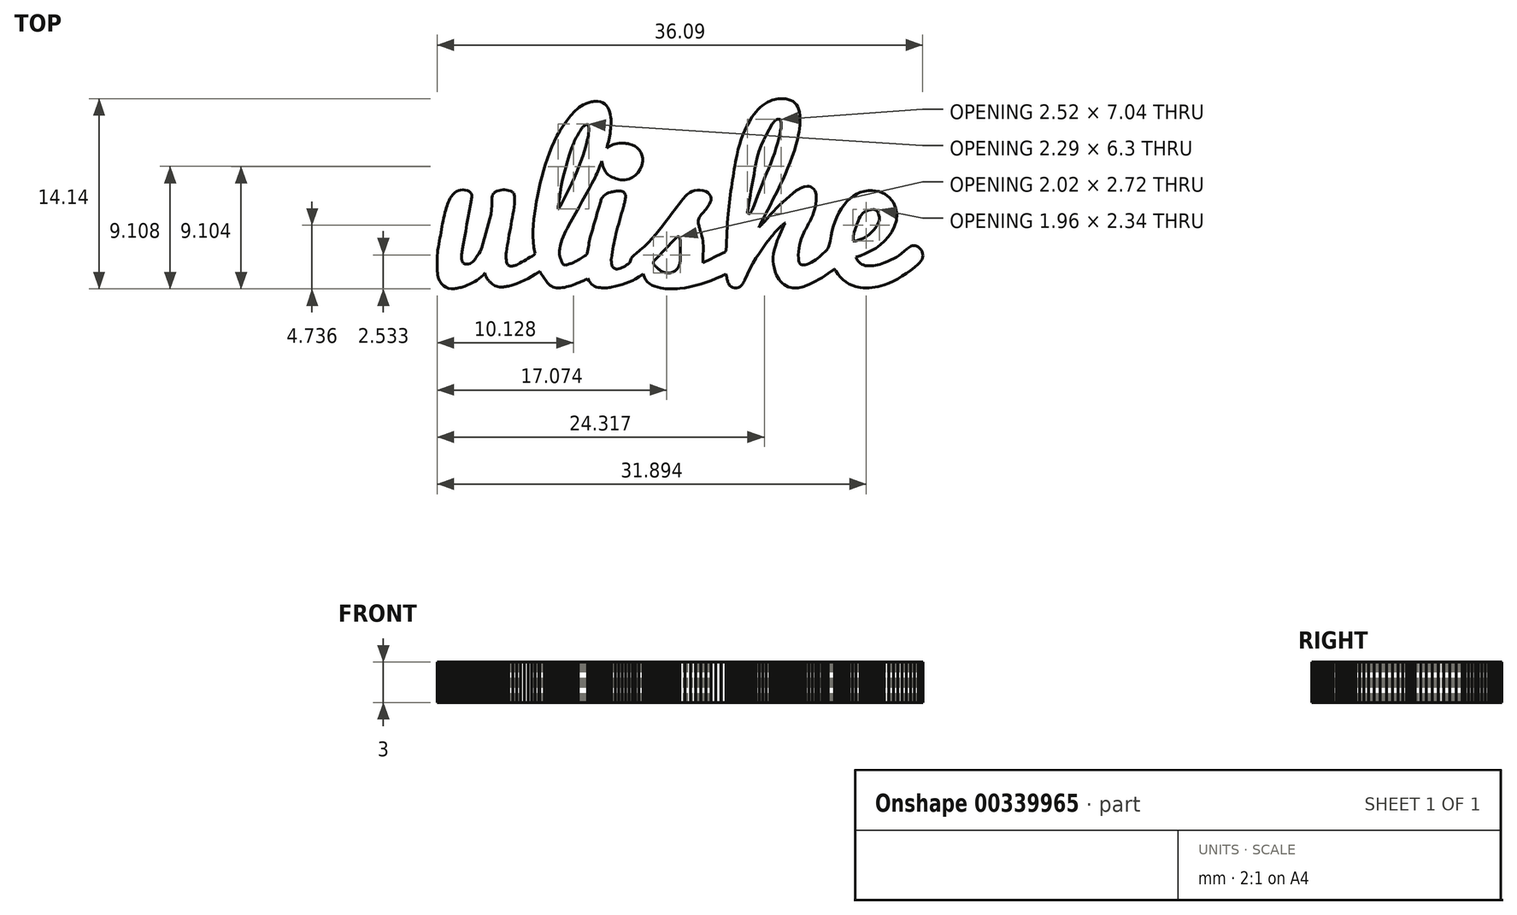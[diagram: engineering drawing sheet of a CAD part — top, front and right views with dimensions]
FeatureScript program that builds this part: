
annotation { "Feature Type Name" : "Feature", "Feature Type Description" : "" }
export const myFeature = defineFeature(function(context is Context, id is Id, definition is map)
    precondition{}
    {
        {
            var Q0;
            Q0=qCreatedBy(makeId("Top.planeOp"),FACE);
            var sketch = newSketch(context, id + "F0", { "sketchPlane" : qUnion([Q0])});
            skLineSegment(sketch, "E0", {"start": v(141.45, -110.72) * mm, "end": v(140.71, -110.13) * mm});
            skLineSegment(sketch, "E1", {"start": v(140.71, -110.13) * mm, "end": v(139.9, -109.7) * mm});
            skLineSegment(sketch, "E2", {"start": v(139.9, -109.7) * mm, "end": v(139.04, -109.45) * mm});
            skLineSegment(sketch, "E3", {"start": v(139.04, -109.45) * mm, "end": v(138.15, -109.35) * mm});
            skLineSegment(sketch, "E4", {"start": v(138.15, -109.35) * mm, "end": v(137.25, -109.42) * mm});
            skLineSegment(sketch, "E5", {"start": v(137.25, -109.42) * mm, "end": v(136.38, -109.65) * mm});
            skLineSegment(sketch, "E6", {"start": v(136.38, -109.65) * mm, "end": v(135.56, -110.05) * mm});
            skLineSegment(sketch, "E7", {"start": v(135.56, -110.05) * mm, "end": v(134.8, -110.61) * mm});
            skLineSegment(sketch, "E8", {"start": v(134.8, -110.61) * mm, "end": v(134.66, -110.74) * mm});
            skLineSegment(sketch, "E9", {"start": v(134.66, -110.74) * mm, "end": v(134.53, -110.85) * mm});
            skLineSegment(sketch, "E10", {"start": v(134.53, -110.85) * mm, "end": v(134.42, -110.95) * mm});
            skLineSegment(sketch, "E11", {"start": v(134.42, -110.95) * mm, "end": v(134.32, -111.05) * mm});
            skLineSegment(sketch, "E12", {"start": v(134.32, -111.05) * mm, "end": v(134.23, -111.12) * mm});
            skLineSegment(sketch, "E13", {"start": v(134.23, -111.12) * mm, "end": v(134.16, -111.19) * mm});
            skLineSegment(sketch, "E14", {"start": v(134.16, -111.19) * mm, "end": v(134.1, -111.23) * mm});
            skLineSegment(sketch, "E15", {"start": v(134.1, -111.23) * mm, "end": v(134.07, -111.26) * mm});
            skLineSegment(sketch, "E16", {"start": v(134.07, -111.26) * mm, "end": v(132.19, -112.88) * mm});
            skLineSegment(sketch, "E17", {"start": v(132.19, -112.88) * mm, "end": v(130.49, -114.23) * mm});
            skLineSegment(sketch, "E18", {"start": v(130.49, -114.23) * mm, "end": v(128.9, -115.38) * mm});
            skLineSegment(sketch, "E19", {"start": v(128.9, -115.38) * mm, "end": v(127.31, -116.38) * mm});
            skLineSegment(sketch, "E20", {"start": v(127.31, -116.38) * mm, "end": v(125.68, -117.3) * mm});
            skLineSegment(sketch, "E21", {"start": v(125.68, -117.3) * mm, "end": v(123.9, -118.17) * mm});
            skLineSegment(sketch, "E22", {"start": v(123.9, -118.17) * mm, "end": v(121.91, -119.06) * mm});
            skLineSegment(sketch, "E23", {"start": v(121.91, -119.06) * mm, "end": v(119.62, -120.04) * mm});
            skLineSegment(sketch, "E24", {"start": v(119.62, -120.04) * mm, "end": v(118.34, -120.53) * mm});
            skLineSegment(sketch, "E25", {"start": v(118.34, -120.53) * mm, "end": v(117.06, -120.94) * mm});
            skLineSegment(sketch, "E26", {"start": v(117.06, -120.94) * mm, "end": v(115.77, -121.28) * mm});
            skLineSegment(sketch, "E27", {"start": v(115.77, -121.28) * mm, "end": v(114.47, -121.53) * mm});
            skLineSegment(sketch, "E28", {"start": v(114.47, -121.53) * mm, "end": v(113.16, -121.72) * mm});
            skLineSegment(sketch, "E29", {"start": v(113.16, -121.72) * mm, "end": v(111.82, -121.83) * mm});
            skLineSegment(sketch, "E30", {"start": v(111.82, -121.83) * mm, "end": v(110.46, -121.86) * mm});
            skLineSegment(sketch, "E31", {"start": v(110.46, -121.86) * mm, "end": v(109.06, -121.83) * mm});
            skLineSegment(sketch, "E32", {"start": v(109.06, -121.83) * mm, "end": v(107.93, -121.69) * mm});
            skLineSegment(sketch, "E33", {"start": v(107.93, -121.69) * mm, "end": v(106.84, -121.37) * mm});
            skLineSegment(sketch, "E34", {"start": v(106.84, -121.37) * mm, "end": v(105.82, -120.88) * mm});
            skLineSegment(sketch, "E35", {"start": v(105.82, -120.88) * mm, "end": v(104.87, -120.26) * mm});
            skLineSegment(sketch, "E36", {"start": v(104.87, -120.26) * mm, "end": v(104.02, -119.5) * mm});
            skLineSegment(sketch, "E37", {"start": v(104.02, -119.5) * mm, "end": v(103.29, -118.62) * mm});
            skLineSegment(sketch, "E38", {"start": v(103.29, -118.62) * mm, "end": v(102.69, -117.64) * mm});
            skLineSegment(sketch, "E39", {"start": v(102.69, -117.64) * mm, "end": v(102.24, -116.57) * mm});
            skLineSegment(sketch, "E40", {"start": v(102.24, -116.57) * mm, "end": v(102.25, -116.55) * mm});
            skLineSegment(sketch, "E41", {"start": v(102.25, -116.55) * mm, "end": v(102.25, -116.54) * mm});
            skLineSegment(sketch, "E42", {"start": v(102.25, -116.54) * mm, "end": v(102.26, -116.52) * mm});
            skLineSegment(sketch, "E43", {"start": v(102.26, -116.52) * mm, "end": v(102.27, -116.5) * mm});
            skLineSegment(sketch, "E44", {"start": v(102.27, -116.5) * mm, "end": v(102.28, -116.5) * mm});
            skLineSegment(sketch, "E45", {"start": v(102.28, -116.5) * mm, "end": v(102.28, -116.48) * mm});
            skLineSegment(sketch, "E46", {"start": v(102.28, -116.48) * mm, "end": v(102.3, -116.46) * mm});
            skLineSegment(sketch, "E47", {"start": v(102.3, -116.46) * mm, "end": v(102.3, -116.45) * mm});
            skLineSegment(sketch, "E48", {"start": v(102.3, -116.45) * mm, "end": v(102.63, -116.34) * mm});
            skLineSegment(sketch, "E49", {"start": v(102.63, -116.34) * mm, "end": v(102.95, -116.23) * mm});
            skLineSegment(sketch, "E50", {"start": v(102.95, -116.23) * mm, "end": v(103.28, -116.13) * mm});
            skLineSegment(sketch, "E51", {"start": v(103.28, -116.13) * mm, "end": v(103.6, -116.02) * mm});
            skLineSegment(sketch, "E52", {"start": v(103.6, -116.02) * mm, "end": v(103.94, -115.92) * mm});
            skLineSegment(sketch, "E53", {"start": v(103.94, -115.92) * mm, "end": v(104.26, -115.8) * mm});
            skLineSegment(sketch, "E54", {"start": v(104.26, -115.8) * mm, "end": v(104.59, -115.7) * mm});
            skLineSegment(sketch, "E55", {"start": v(104.59, -115.7) * mm, "end": v(104.91, -115.59) * mm});
            skLineSegment(sketch, "E56", {"start": v(104.91, -115.59) * mm, "end": v(108.34, -114.23) * mm});
            skLineSegment(sketch, "E57", {"start": v(108.34, -114.23) * mm, "end": v(111.57, -112.65) * mm});
            skLineSegment(sketch, "E58", {"start": v(111.57, -112.65) * mm, "end": v(114.59, -110.83) * mm});
            skLineSegment(sketch, "E59", {"start": v(114.59, -110.83) * mm, "end": v(117.39, -108.74) * mm});
            skLineSegment(sketch, "E60", {"start": v(117.39, -108.74) * mm, "end": v(119.95, -106.38) * mm});
            skLineSegment(sketch, "E61", {"start": v(119.95, -106.38) * mm, "end": v(122.27, -103.74) * mm});
            skLineSegment(sketch, "E62", {"start": v(122.27, -103.74) * mm, "end": v(124.33, -100.8) * mm});
            skLineSegment(sketch, "E63", {"start": v(124.33, -100.8) * mm, "end": v(126.12, -97.53) * mm});
            skLineSegment(sketch, "E64", {"start": v(126.12, -97.53) * mm, "end": v(127.39, -93.69) * mm});
            skLineSegment(sketch, "E65", {"start": v(127.39, -93.69) * mm, "end": v(127.62, -89.82) * mm});
            skLineSegment(sketch, "E66", {"start": v(127.62, -89.82) * mm, "end": v(126.91, -86.1) * mm});
            skLineSegment(sketch, "E67", {"start": v(126.91, -86.1) * mm, "end": v(125.36, -82.67) * mm});
            skLineSegment(sketch, "E68", {"start": v(125.36, -82.67) * mm, "end": v(123.05, -79.71) * mm});
            skLineSegment(sketch, "E69", {"start": v(123.05, -79.71) * mm, "end": v(120.09, -77.37) * mm});
            skLineSegment(sketch, "E70", {"start": v(120.09, -77.37) * mm, "end": v(116.56, -75.81) * mm});
            skLineSegment(sketch, "E71", {"start": v(116.56, -75.81) * mm, "end": v(112.57, -75.2) * mm});
            skLineSegment(sketch, "E72", {"start": v(112.57, -75.2) * mm, "end": v(109.87, -75.3) * mm});
            skLineSegment(sketch, "E73", {"start": v(109.87, -75.3) * mm, "end": v(107.32, -75.7) * mm});
            skLineSegment(sketch, "E74", {"start": v(107.32, -75.7) * mm, "end": v(104.93, -76.4) * mm});
            skLineSegment(sketch, "E75", {"start": v(104.93, -76.4) * mm, "end": v(102.68, -77.37) * mm});
            skLineSegment(sketch, "E76", {"start": v(102.68, -77.37) * mm, "end": v(100.57, -78.61) * mm});
            skLineSegment(sketch, "E77", {"start": v(100.57, -78.61) * mm, "end": v(98.6, -80.12) * mm});
            skLineSegment(sketch, "E78", {"start": v(98.6, -80.12) * mm, "end": v(96.76, -81.88) * mm});
            skLineSegment(sketch, "E79", {"start": v(96.76, -81.88) * mm, "end": v(95.04, -83.87) * mm});
            skLineSegment(sketch, "E80", {"start": v(95.04, -83.87) * mm, "end": v(93.23, -86.4) * mm});
            skLineSegment(sketch, "E81", {"start": v(93.23, -86.4) * mm, "end": v(91.66, -89.03) * mm});
            skLineSegment(sketch, "E82", {"start": v(91.66, -89.03) * mm, "end": v(90.32, -91.76) * mm});
            skLineSegment(sketch, "E83", {"start": v(90.32, -91.76) * mm, "end": v(89.18, -94.57) * mm});
            skLineSegment(sketch, "E84", {"start": v(89.18, -94.57) * mm, "end": v(88.22, -97.45) * mm});
            skLineSegment(sketch, "E85", {"start": v(88.22, -97.45) * mm, "end": v(87.43, -100.39) * mm});
            skLineSegment(sketch, "E86", {"start": v(87.43, -100.39) * mm, "end": v(86.77, -103.37) * mm});
            skLineSegment(sketch, "E87", {"start": v(86.77, -103.37) * mm, "end": v(86.22, -106.4) * mm});
            skLineSegment(sketch, "E88", {"start": v(86.22, -106.4) * mm, "end": v(86.04, -107.43) * mm});
            skLineSegment(sketch, "E89", {"start": v(86.04, -107.43) * mm, "end": v(85.82, -108.43) * mm});
            skLineSegment(sketch, "E90", {"start": v(85.82, -108.43) * mm, "end": v(85.54, -109.37) * mm});
            skLineSegment(sketch, "E91", {"start": v(85.54, -109.37) * mm, "end": v(85.2, -110.26) * mm});
            skLineSegment(sketch, "E92", {"start": v(85.2, -110.26) * mm, "end": v(84.77, -111.1) * mm});
            skLineSegment(sketch, "E93", {"start": v(84.77, -111.1) * mm, "end": v(84.23, -111.9) * mm});
            skLineSegment(sketch, "E94", {"start": v(84.23, -111.9) * mm, "end": v(83.57, -112.62) * mm});
            skLineSegment(sketch, "E95", {"start": v(83.57, -112.62) * mm, "end": v(82.78, -113.3) * mm});
            skLineSegment(sketch, "E96", {"start": v(82.78, -113.3) * mm, "end": v(82.66, -113.4) * mm});
            skLineSegment(sketch, "E97", {"start": v(82.66, -113.4) * mm, "end": v(82.55, -113.5) * mm});
            skLineSegment(sketch, "E98", {"start": v(82.55, -113.5) * mm, "end": v(82.45, -113.6) * mm});
            skLineSegment(sketch, "E99", {"start": v(82.45, -113.6) * mm, "end": v(82.34, -113.7) * mm});
            skLineSegment(sketch, "E100", {"start": v(82.34, -113.7) * mm, "end": v(82.24, -113.82) * mm});
            skLineSegment(sketch, "E101", {"start": v(82.24, -113.82) * mm, "end": v(82.14, -113.93) * mm});
            skLineSegment(sketch, "E102", {"start": v(82.14, -113.93) * mm, "end": v(82.03, -114.04) * mm});
            skLineSegment(sketch, "E103", {"start": v(82.03, -114.04) * mm, "end": v(81.92, -114.14) * mm});
            skLineSegment(sketch, "E104", {"start": v(81.92, -114.14) * mm, "end": v(80.79, -115.2) * mm});
            skLineSegment(sketch, "E105", {"start": v(80.79, -115.2) * mm, "end": v(79.63, -116.22) * mm});
            skLineSegment(sketch, "E106", {"start": v(79.63, -116.22) * mm, "end": v(78.43, -117.2) * mm});
            skLineSegment(sketch, "E107", {"start": v(78.43, -117.2) * mm, "end": v(77.2, -118.1) * mm});
            skLineSegment(sketch, "E108", {"start": v(77.2, -118.1) * mm, "end": v(75.92, -118.95) * mm});
            skLineSegment(sketch, "E109", {"start": v(75.92, -118.95) * mm, "end": v(74.6, -119.7) * mm});
            skLineSegment(sketch, "E110", {"start": v(74.6, -119.7) * mm, "end": v(73.2, -120.37) * mm});
            skLineSegment(sketch, "E111", {"start": v(73.2, -120.37) * mm, "end": v(71.73, -120.93) * mm});
            skLineSegment(sketch, "E112", {"start": v(71.73, -120.93) * mm, "end": v(70.6, -121.24) * mm});
            skLineSegment(sketch, "E113", {"start": v(70.6, -121.24) * mm, "end": v(69.61, -121.35) * mm});
            skLineSegment(sketch, "E114", {"start": v(69.61, -121.35) * mm, "end": v(68.78, -121.26) * mm});
            skLineSegment(sketch, "E115", {"start": v(68.78, -121.26) * mm, "end": v(68.1, -120.95) * mm});
            skLineSegment(sketch, "E116", {"start": v(68.1, -120.95) * mm, "end": v(67.55, -120.43) * mm});
            skLineSegment(sketch, "E117", {"start": v(67.55, -120.43) * mm, "end": v(67.13, -119.7) * mm});
            skLineSegment(sketch, "E118", {"start": v(67.13, -119.7) * mm, "end": v(66.84, -118.75) * mm});
            skLineSegment(sketch, "E119", {"start": v(66.84, -118.75) * mm, "end": v(66.66, -117.57) * mm});
            skLineSegment(sketch, "E120", {"start": v(66.66, -117.57) * mm, "end": v(66.66, -117.52) * mm});
            skLineSegment(sketch, "E121", {"start": v(66.66, -117.52) * mm, "end": v(66.66, -117.48) * mm});
            skLineSegment(sketch, "E122", {"start": v(66.66, -117.48) * mm, "end": v(66.65, -117.43) * mm});
            skLineSegment(sketch, "E123", {"start": v(66.65, -117.43) * mm, "end": v(66.65, -117.39) * mm});
            skLineSegment(sketch, "E124", {"start": v(66.65, -117.39) * mm, "end": v(66.65, -117.34) * mm});
            skLineSegment(sketch, "E125", {"start": v(66.65, -117.34) * mm, "end": v(66.64, -117.3) * mm});
            skLineSegment(sketch, "E126", {"start": v(66.64, -117.3) * mm, "end": v(66.64, -117.26) * mm});
            skLineSegment(sketch, "E127", {"start": v(66.64, -117.26) * mm, "end": v(66.64, -117.21) * mm});
            skLineSegment(sketch, "E128", {"start": v(66.64, -117.21) * mm, "end": v(66.6, -115.13) * mm});
            skLineSegment(sketch, "E129", {"start": v(66.6, -115.13) * mm, "end": v(66.68, -113.07) * mm});
            skLineSegment(sketch, "E130", {"start": v(66.68, -113.07) * mm, "end": v(66.9, -111.05) * mm});
            skLineSegment(sketch, "E131", {"start": v(66.9, -111.05) * mm, "end": v(67.25, -109.05) * mm});
            skLineSegment(sketch, "E132", {"start": v(67.25, -109.05) * mm, "end": v(67.74, -107.08) * mm});
            skLineSegment(sketch, "E133", {"start": v(67.74, -107.08) * mm, "end": v(68.36, -105.14) * mm});
            skLineSegment(sketch, "E134", {"start": v(68.36, -105.14) * mm, "end": v(69.11, -103.22) * mm});
            skLineSegment(sketch, "E135", {"start": v(69.11, -103.22) * mm, "end": v(69.99, -101.34) * mm});
            skLineSegment(sketch, "E136", {"start": v(69.99, -101.34) * mm, "end": v(70.57, -100.2) * mm});
            skLineSegment(sketch, "E137", {"start": v(70.57, -100.2) * mm, "end": v(71.15, -99.07) * mm});
            skLineSegment(sketch, "E138", {"start": v(71.15, -99.07) * mm, "end": v(71.75, -97.95) * mm});
            skLineSegment(sketch, "E139", {"start": v(71.75, -97.95) * mm, "end": v(72.34, -96.82) * mm});
            skLineSegment(sketch, "E140", {"start": v(72.34, -96.82) * mm, "end": v(72.93, -95.7) * mm});
            skLineSegment(sketch, "E141", {"start": v(72.93, -95.7) * mm, "end": v(73.52, -94.56) * mm});
            skLineSegment(sketch, "E142", {"start": v(73.52, -94.56) * mm, "end": v(74.09, -93.43) * mm});
            skLineSegment(sketch, "E143", {"start": v(74.09, -93.43) * mm, "end": v(74.65, -92.29) * mm});
            skLineSegment(sketch, "E144", {"start": v(74.65, -92.29) * mm, "end": v(75.43, -90.56) * mm});
            skLineSegment(sketch, "E145", {"start": v(75.43, -90.56) * mm, "end": v(76.09, -88.8) * mm});
            skLineSegment(sketch, "E146", {"start": v(76.09, -88.8) * mm, "end": v(76.64, -87.02) * mm});
            skLineSegment(sketch, "E147", {"start": v(76.64, -87.02) * mm, "end": v(77.06, -85.22) * mm});
            skLineSegment(sketch, "E148", {"start": v(77.06, -85.22) * mm, "end": v(77.37, -83.4) * mm});
            skLineSegment(sketch, "E149", {"start": v(77.37, -83.4) * mm, "end": v(77.54, -81.54) * mm});
            skLineSegment(sketch, "E150", {"start": v(77.54, -81.54) * mm, "end": v(77.57, -79.66) * mm});
            skLineSegment(sketch, "E151", {"start": v(77.57, -79.66) * mm, "end": v(77.47, -77.76) * mm});
            skLineSegment(sketch, "E152", {"start": v(77.47, -77.76) * mm, "end": v(77.23, -76.42) * mm});
            skLineSegment(sketch, "E153", {"start": v(77.23, -76.42) * mm, "end": v(76.77, -75.26) * mm});
            skLineSegment(sketch, "E154", {"start": v(76.77, -75.26) * mm, "end": v(76.11, -74.28) * mm});
            skLineSegment(sketch, "E155", {"start": v(76.11, -74.28) * mm, "end": v(75.28, -73.5) * mm});
            skLineSegment(sketch, "E156", {"start": v(75.28, -73.5) * mm, "end": v(74.3, -72.95) * mm});
            skLineSegment(sketch, "E157", {"start": v(74.3, -72.95) * mm, "end": v(73.17, -72.63) * mm});
            skLineSegment(sketch, "E158", {"start": v(73.17, -72.63) * mm, "end": v(71.92, -72.55) * mm});
            skLineSegment(sketch, "E159", {"start": v(71.92, -72.55) * mm, "end": v(70.58, -72.74) * mm});
            skLineSegment(sketch, "E160", {"start": v(70.58, -72.74) * mm, "end": v(70.15, -72.84) * mm});
            skLineSegment(sketch, "E161", {"start": v(70.15, -72.84) * mm, "end": v(69.72, -72.97) * mm});
            skLineSegment(sketch, "E162", {"start": v(69.72, -72.97) * mm, "end": v(69.29, -73.1) * mm});
            skLineSegment(sketch, "E163", {"start": v(69.29, -73.1) * mm, "end": v(68.87, -73.26) * mm});
            skLineSegment(sketch, "E164", {"start": v(68.87, -73.26) * mm, "end": v(68.45, -73.44) * mm});
            skLineSegment(sketch, "E165", {"start": v(68.45, -73.44) * mm, "end": v(68.04, -73.62) * mm});
            skLineSegment(sketch, "E166", {"start": v(68.04, -73.62) * mm, "end": v(67.64, -73.82) * mm});
            skLineSegment(sketch, "E167", {"start": v(67.64, -73.82) * mm, "end": v(67.25, -74.04) * mm});
            skLineSegment(sketch, "E168", {"start": v(67.25, -74.04) * mm, "end": v(66.74, -74.34) * mm});
            skLineSegment(sketch, "E169", {"start": v(66.74, -74.34) * mm, "end": v(66.23, -74.66) * mm});
            skLineSegment(sketch, "E170", {"start": v(66.23, -74.66) * mm, "end": v(65.73, -74.98) * mm});
            skLineSegment(sketch, "E171", {"start": v(65.73, -74.98) * mm, "end": v(65.23, -75.32) * mm});
            skLineSegment(sketch, "E172", {"start": v(65.23, -75.32) * mm, "end": v(64.74, -75.67) * mm});
            skLineSegment(sketch, "E173", {"start": v(64.74, -75.67) * mm, "end": v(64.26, -76.03) * mm});
            skLineSegment(sketch, "E174", {"start": v(64.26, -76.03) * mm, "end": v(63.8, -76.4) * mm});
            skLineSegment(sketch, "E175", {"start": v(63.8, -76.4) * mm, "end": v(63.33, -76.78) * mm});
            skLineSegment(sketch, "E176", {"start": v(63.33, -76.78) * mm, "end": v(61.19, -78.58) * mm});
            skLineSegment(sketch, "E177", {"start": v(61.19, -78.58) * mm, "end": v(59.07, -80.4) * mm});
            skLineSegment(sketch, "E178", {"start": v(59.07, -80.4) * mm, "end": v(56.99, -82.25) * mm});
            skLineSegment(sketch, "E179", {"start": v(56.99, -82.25) * mm, "end": v(54.95, -84.14) * mm});
            skLineSegment(sketch, "E180", {"start": v(54.95, -84.14) * mm, "end": v(52.96, -86.08) * mm});
            skLineSegment(sketch, "E181", {"start": v(52.96, -86.08) * mm, "end": v(51.03, -88.09) * mm});
            skLineSegment(sketch, "E182", {"start": v(51.03, -88.09) * mm, "end": v(49.18, -90.17) * mm});
            skLineSegment(sketch, "E183", {"start": v(49.18, -90.17) * mm, "end": v(47.4, -92.33) * mm});
            skLineSegment(sketch, "E184", {"start": v(47.4, -92.33) * mm, "end": v(46.95, -92.91) * mm});
            skLineSegment(sketch, "E185", {"start": v(46.95, -92.91) * mm, "end": v(46.62, -93.35) * mm});
            skLineSegment(sketch, "E186", {"start": v(46.62, -93.35) * mm, "end": v(46.36, -93.67) * mm});
            skLineSegment(sketch, "E187", {"start": v(46.36, -93.67) * mm, "end": v(46.13, -93.95) * mm});
            skLineSegment(sketch, "E188", {"start": v(46.13, -93.95) * mm, "end": v(45.89, -94.23) * mm});
            skLineSegment(sketch, "E189", {"start": v(45.89, -94.23) * mm, "end": v(45.58, -94.55) * mm});
            skLineSegment(sketch, "E190", {"start": v(45.58, -94.55) * mm, "end": v(45.17, -94.98) * mm});
            skLineSegment(sketch, "E191", {"start": v(45.17, -94.98) * mm, "end": v(44.6, -95.56) * mm});
            skLineSegment(sketch, "E192", {"start": v(44.6, -95.56) * mm, "end": v(44.4, -95.77) * mm});
            skLineSegment(sketch, "E193", {"start": v(44.4, -95.77) * mm, "end": v(44.12, -96.05) * mm});
            skLineSegment(sketch, "E194", {"start": v(44.12, -96.05) * mm, "end": v(43.8, -96.36) * mm});
            skLineSegment(sketch, "E195", {"start": v(43.8, -96.36) * mm, "end": v(43.44, -96.7) * mm});
            skLineSegment(sketch, "E196", {"start": v(43.44, -96.7) * mm, "end": v(43.07, -97.05) * mm});
            skLineSegment(sketch, "E197", {"start": v(43.07, -97.05) * mm, "end": v(42.7, -97.38) * mm});
            skLineSegment(sketch, "E198", {"start": v(42.7, -97.38) * mm, "end": v(42.38, -97.69) * mm});
            skLineSegment(sketch, "E199", {"start": v(42.38, -97.69) * mm, "end": v(42.1, -97.95) * mm});
            skLineSegment(sketch, "E200", {"start": v(42.1, -97.95) * mm, "end": v(42.2, -97.76) * mm});
            skLineSegment(sketch, "E201", {"start": v(42.2, -97.76) * mm, "end": v(42.32, -97.53) * mm});
            skLineSegment(sketch, "E202", {"start": v(42.32, -97.53) * mm, "end": v(42.45, -97.28) * mm});
            skLineSegment(sketch, "E203", {"start": v(42.45, -97.28) * mm, "end": v(42.58, -97.02) * mm});
            skLineSegment(sketch, "E204", {"start": v(42.58, -97.02) * mm, "end": v(42.72, -96.76) * mm});
            skLineSegment(sketch, "E205", {"start": v(42.72, -96.76) * mm, "end": v(42.84, -96.53) * mm});
            skLineSegment(sketch, "E206", {"start": v(42.84, -96.53) * mm, "end": v(42.95, -96.32) * mm});
            skLineSegment(sketch, "E207", {"start": v(42.95, -96.32) * mm, "end": v(43.04, -96.15) * mm});
            skLineSegment(sketch, "E208", {"start": v(43.04, -96.15) * mm, "end": v(44.57, -93.14) * mm});
            skLineSegment(sketch, "E209", {"start": v(44.57, -93.14) * mm, "end": v(46.1, -90.15) * mm});
            skLineSegment(sketch, "E210", {"start": v(46.1, -90.15) * mm, "end": v(47.65, -87.15) * mm});
            skLineSegment(sketch, "E211", {"start": v(47.65, -87.15) * mm, "end": v(49.18, -84.15) * mm});
            skLineSegment(sketch, "E212", {"start": v(49.18, -84.15) * mm, "end": v(50.71, -81.15) * mm});
            skLineSegment(sketch, "E213", {"start": v(50.71, -81.15) * mm, "end": v(52.23, -78.14) * mm});
            skLineSegment(sketch, "E214", {"start": v(52.23, -78.14) * mm, "end": v(53.73, -75.12) * mm});
            skLineSegment(sketch, "E215", {"start": v(53.73, -75.12) * mm, "end": v(55.2, -72.1) * mm});
            skLineSegment(sketch, "E216", {"start": v(55.2, -72.1) * mm, "end": v(56.87, -68.57) * mm});
            skLineSegment(sketch, "E217", {"start": v(56.87, -68.57) * mm, "end": v(58.46, -65.02) * mm});
            skLineSegment(sketch, "E218", {"start": v(58.46, -65.02) * mm, "end": v(59.98, -61.44) * mm});
            skLineSegment(sketch, "E219", {"start": v(59.98, -61.44) * mm, "end": v(61.42, -57.83) * mm});
            skLineSegment(sketch, "E220", {"start": v(61.42, -57.83) * mm, "end": v(62.75, -54.18) * mm});
            skLineSegment(sketch, "E221", {"start": v(62.75, -54.18) * mm, "end": v(63.98, -50.49) * mm});
            skLineSegment(sketch, "E222", {"start": v(63.98, -50.49) * mm, "end": v(65.1, -46.75) * mm});
            skLineSegment(sketch, "E223", {"start": v(65.1, -46.75) * mm, "end": v(66.09, -42.98) * mm});
            skLineSegment(sketch, "E224", {"start": v(66.09, -42.98) * mm, "end": v(66.55, -40.95) * mm});
            skLineSegment(sketch, "E225", {"start": v(66.55, -40.95) * mm, "end": v(66.94, -38.92) * mm});
            skLineSegment(sketch, "E226", {"start": v(66.94, -38.92) * mm, "end": v(67.25, -36.88) * mm});
            skLineSegment(sketch, "E227", {"start": v(67.25, -36.88) * mm, "end": v(67.47, -34.84) * mm});
            skLineSegment(sketch, "E228", {"start": v(67.47, -34.84) * mm, "end": v(67.58, -32.79) * mm});
            skLineSegment(sketch, "E229", {"start": v(67.58, -32.79) * mm, "end": v(67.57, -30.73) * mm});
            skLineSegment(sketch, "E230", {"start": v(67.57, -30.73) * mm, "end": v(67.43, -28.66) * mm});
            skLineSegment(sketch, "E231", {"start": v(67.43, -28.66) * mm, "end": v(67.15, -26.58) * mm});
            skLineSegment(sketch, "E232", {"start": v(67.15, -26.58) * mm, "end": v(66.75, -24.91) * mm});
            skLineSegment(sketch, "E233", {"start": v(66.75, -24.91) * mm, "end": v(66.16, -23.4) * mm});
            skLineSegment(sketch, "E234", {"start": v(66.16, -23.4) * mm, "end": v(65.39, -22.09) * mm});
            skLineSegment(sketch, "E235", {"start": v(65.39, -22.09) * mm, "end": v(64.43, -20.95) * mm});
            skLineSegment(sketch, "E236", {"start": v(64.43, -20.95) * mm, "end": v(63.3, -20.02) * mm});
            skLineSegment(sketch, "E237", {"start": v(63.3, -20.02) * mm, "end": v(61.98, -19.28) * mm});
            skLineSegment(sketch, "E238", {"start": v(61.98, -19.28) * mm, "end": v(60.5, -18.75) * mm});
            skLineSegment(sketch, "E239", {"start": v(60.5, -18.75) * mm, "end": v(58.85, -18.44) * mm});
            skLineSegment(sketch, "E240", {"start": v(58.85, -18.44) * mm, "end": v(57.63, -18.33) * mm});
            skLineSegment(sketch, "E241", {"start": v(57.63, -18.33) * mm, "end": v(56.42, -18.3) * mm});
            skLineSegment(sketch, "E242", {"start": v(56.42, -18.3) * mm, "end": v(55.21, -18.32) * mm});
            skLineSegment(sketch, "E243", {"start": v(55.21, -18.32) * mm, "end": v(54.01, -18.43) * mm});
            skLineSegment(sketch, "E244", {"start": v(54.01, -18.43) * mm, "end": v(52.82, -18.6) * mm});
            skLineSegment(sketch, "E245", {"start": v(52.82, -18.6) * mm, "end": v(51.64, -18.87) * mm});
            skLineSegment(sketch, "E246", {"start": v(51.64, -18.87) * mm, "end": v(50.47, -19.21) * mm});
            skLineSegment(sketch, "E247", {"start": v(50.47, -19.21) * mm, "end": v(49.32, -19.64) * mm});
            skLineSegment(sketch, "E248", {"start": v(49.32, -19.64) * mm, "end": v(47.55, -20.47) * mm});
            skLineSegment(sketch, "E249", {"start": v(47.55, -20.47) * mm, "end": v(45.9, -21.44) * mm});
            skLineSegment(sketch, "E250", {"start": v(45.9, -21.44) * mm, "end": v(44.36, -22.53) * mm});
            skLineSegment(sketch, "E251", {"start": v(44.36, -22.53) * mm, "end": v(42.92, -23.74) * mm});
            skLineSegment(sketch, "E252", {"start": v(42.92, -23.74) * mm, "end": v(41.58, -25.05) * mm});
            skLineSegment(sketch, "E253", {"start": v(41.58, -25.05) * mm, "end": v(40.32, -26.46) * mm});
            skLineSegment(sketch, "E254", {"start": v(40.32, -26.46) * mm, "end": v(39.13, -27.95) * mm});
            skLineSegment(sketch, "E255", {"start": v(39.13, -27.95) * mm, "end": v(38.02, -29.52) * mm});
            skLineSegment(sketch, "E256", {"start": v(38.02, -29.52) * mm, "end": v(36.3, -32.23) * mm});
            skLineSegment(sketch, "E257", {"start": v(36.3, -32.23) * mm, "end": v(34.75, -35.01) * mm});
            skLineSegment(sketch, "E258", {"start": v(34.75, -35.01) * mm, "end": v(33.37, -37.86) * mm});
            skLineSegment(sketch, "E259", {"start": v(33.37, -37.86) * mm, "end": v(32.15, -40.77) * mm});
            skLineSegment(sketch, "E260", {"start": v(32.15, -40.77) * mm, "end": v(31.06, -43.74) * mm});
            skLineSegment(sketch, "E261", {"start": v(31.06, -43.74) * mm, "end": v(30.1, -46.76) * mm});
            skLineSegment(sketch, "E262", {"start": v(30.1, -46.76) * mm, "end": v(29.28, -49.83) * mm});
            skLineSegment(sketch, "E263", {"start": v(29.28, -49.83) * mm, "end": v(28.55, -52.93) * mm});
            skLineSegment(sketch, "E264", {"start": v(28.55, -52.93) * mm, "end": v(28.1, -55.16) * mm});
            skLineSegment(sketch, "E265", {"start": v(28.1, -55.16) * mm, "end": v(27.67, -57.4) * mm});
            skLineSegment(sketch, "E266", {"start": v(27.67, -57.4) * mm, "end": v(27.27, -59.63) * mm});
            skLineSegment(sketch, "E267", {"start": v(27.27, -59.63) * mm, "end": v(26.89, -61.88) * mm});
            skLineSegment(sketch, "E268", {"start": v(26.89, -61.88) * mm, "end": v(26.53, -64.12) * mm});
            skLineSegment(sketch, "E269", {"start": v(26.53, -64.12) * mm, "end": v(26.18, -66.38) * mm});
            skLineSegment(sketch, "E270", {"start": v(26.18, -66.38) * mm, "end": v(25.84, -68.63) * mm});
            skLineSegment(sketch, "E271", {"start": v(25.84, -68.63) * mm, "end": v(25.5, -70.88) * mm});
            skLineSegment(sketch, "E272", {"start": v(25.5, -70.88) * mm, "end": v(25.15, -73.22) * mm});
            skLineSegment(sketch, "E273", {"start": v(25.15, -73.22) * mm, "end": v(24.8, -75.56) * mm});
            skLineSegment(sketch, "E274", {"start": v(24.8, -75.56) * mm, "end": v(24.46, -77.9) * mm});
            skLineSegment(sketch, "E275", {"start": v(24.46, -77.9) * mm, "end": v(24.12, -80.25) * mm});
            skLineSegment(sketch, "E276", {"start": v(24.12, -80.25) * mm, "end": v(23.81, -82.6) * mm});
            skLineSegment(sketch, "E277", {"start": v(23.81, -82.6) * mm, "end": v(23.52, -84.95) * mm});
            skLineSegment(sketch, "E278", {"start": v(23.52, -84.95) * mm, "end": v(23.27, -87.3) * mm});
            skLineSegment(sketch, "E279", {"start": v(23.27, -87.3) * mm, "end": v(23.04, -89.65) * mm});
            skLineSegment(sketch, "E280", {"start": v(23.04, -89.65) * mm, "end": v(22.82, -92.46) * mm});
            skLineSegment(sketch, "E281", {"start": v(22.82, -92.46) * mm, "end": v(22.64, -95.27) * mm});
            skLineSegment(sketch, "E282", {"start": v(22.64, -95.27) * mm, "end": v(22.48, -98.08) * mm});
            skLineSegment(sketch, "E283", {"start": v(22.48, -98.08) * mm, "end": v(22.34, -100.9) * mm});
            skLineSegment(sketch, "E284", {"start": v(22.34, -100.9) * mm, "end": v(22.21, -103.7) * mm});
            skLineSegment(sketch, "E285", {"start": v(22.21, -103.7) * mm, "end": v(22.08, -106.52) * mm});
            skLineSegment(sketch, "E286", {"start": v(22.08, -106.52) * mm, "end": v(21.95, -109.34) * mm});
            skLineSegment(sketch, "E287", {"start": v(21.95, -109.34) * mm, "end": v(21.8, -112.15) * mm});
            skLineSegment(sketch, "E288", {"start": v(21.8, -112.15) * mm, "end": v(21.78, -112.3) * mm});
            skLineSegment(sketch, "E289", {"start": v(21.78, -112.3) * mm, "end": v(21.74, -112.45) * mm});
            skLineSegment(sketch, "E290", {"start": v(21.74, -112.45) * mm, "end": v(21.67, -112.61) * mm});
            skLineSegment(sketch, "E291", {"start": v(21.67, -112.61) * mm, "end": v(21.59, -112.77) * mm});
            skLineSegment(sketch, "E292", {"start": v(21.59, -112.77) * mm, "end": v(21.5, -112.91) * mm});
            skLineSegment(sketch, "E293", {"start": v(21.5, -112.91) * mm, "end": v(21.38, -113.04) * mm});
            skLineSegment(sketch, "E294", {"start": v(21.38, -113.04) * mm, "end": v(21.27, -113.15) * mm});
            skLineSegment(sketch, "E295", {"start": v(21.27, -113.15) * mm, "end": v(21.14, -113.22) * mm});
            skLineSegment(sketch, "E296", {"start": v(21.14, -113.22) * mm, "end": v(19.44, -114.08) * mm});
            skLineSegment(sketch, "E297", {"start": v(19.44, -114.08) * mm, "end": v(17.73, -114.93) * mm});
            skLineSegment(sketch, "E298", {"start": v(17.73, -114.93) * mm, "end": v(16.02, -115.78) * mm});
            skLineSegment(sketch, "E299", {"start": v(16.02, -115.78) * mm, "end": v(14.3, -116.63) * mm});
            skLineSegment(sketch, "E300", {"start": v(14.3, -116.63) * mm, "end": v(12.6, -117.47) * mm});
            skLineSegment(sketch, "E301", {"start": v(12.6, -117.47) * mm, "end": v(10.9, -118.3) * mm});
            skLineSegment(sketch, "E302", {"start": v(10.9, -118.3) * mm, "end": v(9.2, -119.14) * mm});
            skLineSegment(sketch, "E303", {"start": v(9.2, -119.14) * mm, "end": v(7.5, -119.98) * mm});
            skLineSegment(sketch, "E304", {"start": v(7.5, -119.98) * mm, "end": v(7.5, -119.27) * mm});
            skLineSegment(sketch, "E305", {"start": v(7.5, -119.27) * mm, "end": v(7.48, -118.57) * mm});
            skLineSegment(sketch, "E306", {"start": v(7.48, -118.57) * mm, "end": v(7.46, -117.85) * mm});
            skLineSegment(sketch, "E307", {"start": v(7.46, -117.85) * mm, "end": v(7.45, -117.14) * mm});
            skLineSegment(sketch, "E308", {"start": v(7.45, -117.14) * mm, "end": v(7.44, -116.43) * mm});
            skLineSegment(sketch, "E309", {"start": v(7.44, -116.43) * mm, "end": v(7.45, -115.71) * mm});
            skLineSegment(sketch, "E310", {"start": v(7.45, -115.71) * mm, "end": v(7.48, -115) * mm});
            skLineSegment(sketch, "E311", {"start": v(7.48, -115) * mm, "end": v(7.54, -114.29) * mm});
            skLineSegment(sketch, "E312", {"start": v(7.54, -114.29) * mm, "end": v(7.67, -112.67) * mm});
            skLineSegment(sketch, "E313", {"start": v(7.67, -112.67) * mm, "end": v(7.73, -111.07) * mm});
            skLineSegment(sketch, "E314", {"start": v(7.73, -111.07) * mm, "end": v(7.7, -109.47) * mm});
            skLineSegment(sketch, "E315", {"start": v(7.7, -109.47) * mm, "end": v(7.6, -107.89) * mm});
            skLineSegment(sketch, "E316", {"start": v(7.6, -107.89) * mm, "end": v(7.42, -106.31) * mm});
            skLineSegment(sketch, "E317", {"start": v(7.42, -106.31) * mm, "end": v(7.15, -104.74) * mm});
            skLineSegment(sketch, "E318", {"start": v(7.15, -104.74) * mm, "end": v(6.77, -103.18) * mm});
            skLineSegment(sketch, "E319", {"start": v(6.77, -103.18) * mm, "end": v(6.3, -101.63) * mm});
            skLineSegment(sketch, "E320", {"start": v(6.3, -101.63) * mm, "end": v(6.09, -101) * mm});
            skLineSegment(sketch, "E321", {"start": v(6.09, -101) * mm, "end": v(5.9, -100.35) * mm});
            skLineSegment(sketch, "E322", {"start": v(5.9, -100.35) * mm, "end": v(5.72, -99.7) * mm});
            skLineSegment(sketch, "E323", {"start": v(5.72, -99.7) * mm, "end": v(5.54, -99.05) * mm});
            skLineSegment(sketch, "E324", {"start": v(5.54, -99.05) * mm, "end": v(5.38, -98.4) * mm});
            skLineSegment(sketch, "E325", {"start": v(5.38, -98.4) * mm, "end": v(5.21, -97.74) * mm});
            skLineSegment(sketch, "E326", {"start": v(5.21, -97.74) * mm, "end": v(5.05, -97.09) * mm});
            skLineSegment(sketch, "E327", {"start": v(5.05, -97.09) * mm, "end": v(4.88, -96.44) * mm});
            skLineSegment(sketch, "E328", {"start": v(4.88, -96.44) * mm, "end": v(4.68, -95.54) * mm});
            skLineSegment(sketch, "E329", {"start": v(4.68, -95.54) * mm, "end": v(4.6, -94.67) * mm});
            skLineSegment(sketch, "E330", {"start": v(4.6, -94.67) * mm, "end": v(4.61, -93.84) * mm});
            skLineSegment(sketch, "E331", {"start": v(4.61, -93.84) * mm, "end": v(4.75, -93.03) * mm});
            skLineSegment(sketch, "E332", {"start": v(4.75, -93.03) * mm, "end": v(5, -92.25) * mm});
            skLineSegment(sketch, "E333", {"start": v(5, -92.25) * mm, "end": v(5.39, -91.5) * mm});
            skLineSegment(sketch, "E334", {"start": v(5.39, -91.5) * mm, "end": v(5.9, -90.75) * mm});
            skLineSegment(sketch, "E335", {"start": v(5.9, -90.75) * mm, "end": v(6.55, -90.03) * mm});
            skLineSegment(sketch, "E336", {"start": v(6.55, -90.03) * mm, "end": v(7.25, -89.3) * mm});
            skLineSegment(sketch, "E337", {"start": v(7.25, -89.3) * mm, "end": v(7.93, -88.54) * mm});
            skLineSegment(sketch, "E338", {"start": v(7.93, -88.54) * mm, "end": v(8.59, -87.76) * mm});
            skLineSegment(sketch, "E339", {"start": v(8.59, -87.76) * mm, "end": v(9.22, -86.96) * mm});
            skLineSegment(sketch, "E340", {"start": v(9.22, -86.96) * mm, "end": v(9.83, -86.14) * mm});
            skLineSegment(sketch, "E341", {"start": v(9.83, -86.14) * mm, "end": v(10.42, -85.3) * mm});
            skLineSegment(sketch, "E342", {"start": v(10.42, -85.3) * mm, "end": v(10.99, -84.46) * mm});
            skLineSegment(sketch, "E343", {"start": v(10.99, -84.46) * mm, "end": v(11.53, -83.6) * mm});
            skLineSegment(sketch, "E344", {"start": v(11.53, -83.6) * mm, "end": v(12.1, -82.44) * mm});
            skLineSegment(sketch, "E345", {"start": v(12.1, -82.44) * mm, "end": v(12.4, -81.18) * mm});
            skLineSegment(sketch, "E346", {"start": v(12.4, -81.18) * mm, "end": v(12.44, -79.9) * mm});
            skLineSegment(sketch, "E347", {"start": v(12.44, -79.9) * mm, "end": v(12.17, -78.65) * mm});
            skLineSegment(sketch, "E348", {"start": v(12.17, -78.65) * mm, "end": v(11.57, -77.5) * mm});
            skLineSegment(sketch, "E349", {"start": v(11.57, -77.5) * mm, "end": v(10.62, -76.5) * mm});
            skLineSegment(sketch, "E350", {"start": v(10.62, -76.5) * mm, "end": v(9.3, -75.73) * mm});
            skLineSegment(sketch, "E351", {"start": v(9.3, -75.73) * mm, "end": v(7.59, -75.23) * mm});
            skLineSegment(sketch, "E352", {"start": v(7.59, -75.23) * mm, "end": v(5.7, -75) * mm});
            skLineSegment(sketch, "E353", {"start": v(5.7, -75) * mm, "end": v(3.93, -75.03) * mm});
            skLineSegment(sketch, "E354", {"start": v(3.93, -75.03) * mm, "end": v(2.26, -75.3) * mm});
            skLineSegment(sketch, "E355", {"start": v(2.26, -75.3) * mm, "end": v(0.68, -75.8) * mm});
            skLineSegment(sketch, "E356", {"start": v(0.68, -75.8) * mm, "end": v(-0.8, -76.55) * mm});
            skLineSegment(sketch, "E357", {"start": v(-0.8, -76.55) * mm, "end": v(-2.18, -77.53) * mm});
            skLineSegment(sketch, "E358", {"start": v(-2.18, -77.53) * mm, "end": v(-3.47, -78.73) * mm});
            skLineSegment(sketch, "E359", {"start": v(-3.47, -78.73) * mm, "end": v(-4.68, -80.15) * mm});
            skLineSegment(sketch, "E360", {"start": v(-4.68, -80.15) * mm, "end": v(-6, -81.9) * mm});
            skLineSegment(sketch, "E361", {"start": v(-6, -81.9) * mm, "end": v(-7.34, -83.63) * mm});
            skLineSegment(sketch, "E362", {"start": v(-7.34, -83.63) * mm, "end": v(-8.68, -85.36) * mm});
            skLineSegment(sketch, "E363", {"start": v(-8.68, -85.36) * mm, "end": v(-10.01, -87.1) * mm});
            skLineSegment(sketch, "E364", {"start": v(-10.01, -87.1) * mm, "end": v(-11.34, -88.84) * mm});
            skLineSegment(sketch, "E365", {"start": v(-11.34, -88.84) * mm, "end": v(-12.66, -90.59) * mm});
            skLineSegment(sketch, "E366", {"start": v(-12.66, -90.59) * mm, "end": v(-13.96, -92.34) * mm});
            skLineSegment(sketch, "E367", {"start": v(-13.96, -92.34) * mm, "end": v(-15.25, -94.11) * mm});
            skLineSegment(sketch, "E368", {"start": v(-15.25, -94.11) * mm, "end": v(-17.32, -96.9) * mm});
            skLineSegment(sketch, "E369", {"start": v(-17.32, -96.9) * mm, "end": v(-19.44, -99.64) * mm});
            skLineSegment(sketch, "E370", {"start": v(-19.44, -99.64) * mm, "end": v(-21.64, -102.31) * mm});
            skLineSegment(sketch, "E371", {"start": v(-21.64, -102.31) * mm, "end": v(-23.92, -104.9) * mm});
            skLineSegment(sketch, "E372", {"start": v(-23.92, -104.9) * mm, "end": v(-26.3, -107.4) * mm});
            skLineSegment(sketch, "E373", {"start": v(-26.3, -107.4) * mm, "end": v(-28.78, -109.8) * mm});
            skLineSegment(sketch, "E374", {"start": v(-28.78, -109.8) * mm, "end": v(-31.38, -112.09) * mm});
            skLineSegment(sketch, "E375", {"start": v(-31.38, -112.09) * mm, "end": v(-34.1, -114.26) * mm});
            skLineSegment(sketch, "E376", {"start": v(-34.1, -114.26) * mm, "end": v(-34.76, -114.8) * mm});
            skLineSegment(sketch, "E377", {"start": v(-34.76, -114.8) * mm, "end": v(-35.38, -115.35) * mm});
            skLineSegment(sketch, "E378", {"start": v(-35.38, -115.35) * mm, "end": v(-35.94, -115.96) * mm});
            skLineSegment(sketch, "E379", {"start": v(-35.94, -115.96) * mm, "end": v(-36.46, -116.6) * mm});
            skLineSegment(sketch, "E380", {"start": v(-36.46, -116.6) * mm, "end": v(-36.9, -117.3) * mm});
            skLineSegment(sketch, "E381", {"start": v(-36.9, -117.3) * mm, "end": v(-37.28, -118.04) * mm});
            skLineSegment(sketch, "E382", {"start": v(-37.28, -118.04) * mm, "end": v(-37.56, -118.84) * mm});
            skLineSegment(sketch, "E383", {"start": v(-37.56, -118.84) * mm, "end": v(-37.76, -119.7) * mm});
            skLineSegment(sketch, "E384", {"start": v(-37.76, -119.7) * mm, "end": v(-37.78, -119.77) * mm});
            skLineSegment(sketch, "E385", {"start": v(-37.78, -119.77) * mm, "end": v(-37.8, -119.84) * mm});
            skLineSegment(sketch, "E386", {"start": v(-37.8, -119.84) * mm, "end": v(-37.83, -119.9) * mm});
            skLineSegment(sketch, "E387", {"start": v(-37.83, -119.9) * mm, "end": v(-37.87, -119.98) * mm});
            skLineSegment(sketch, "E388", {"start": v(-37.87, -119.98) * mm, "end": v(-37.92, -120.04) * mm});
            skLineSegment(sketch, "E389", {"start": v(-37.92, -120.04) * mm, "end": v(-37.96, -120.1) * mm});
            skLineSegment(sketch, "E390", {"start": v(-37.96, -120.1) * mm, "end": v(-38.02, -120.15) * mm});
            skLineSegment(sketch, "E391", {"start": v(-38.02, -120.15) * mm, "end": v(-38.07, -120.2) * mm});
            skLineSegment(sketch, "E392", {"start": v(-38.07, -120.2) * mm, "end": v(-38.95, -120.8) * mm});
            skLineSegment(sketch, "E393", {"start": v(-38.95, -120.8) * mm, "end": v(-39.83, -121.39) * mm});
            skLineSegment(sketch, "E394", {"start": v(-39.83, -121.39) * mm, "end": v(-40.73, -121.96) * mm});
            skLineSegment(sketch, "E395", {"start": v(-40.73, -121.96) * mm, "end": v(-41.65, -122.49) * mm});
            skLineSegment(sketch, "E396", {"start": v(-41.65, -122.49) * mm, "end": v(-42.6, -122.95) * mm});
            skLineSegment(sketch, "E397", {"start": v(-42.6, -122.95) * mm, "end": v(-43.57, -123.34) * mm});
            skLineSegment(sketch, "E398", {"start": v(-43.57, -123.34) * mm, "end": v(-44.6, -123.63) * mm});
            skLineSegment(sketch, "E399", {"start": v(-44.6, -123.63) * mm, "end": v(-45.69, -123.8) * mm});
            skLineSegment(sketch, "E400", {"start": v(-45.69, -123.8) * mm, "end": v(-46.26, -123.8) * mm});
            skLineSegment(sketch, "E401", {"start": v(-46.26, -123.8) * mm, "end": v(-46.8, -123.7) * mm});
            skLineSegment(sketch, "E402", {"start": v(-46.8, -123.7) * mm, "end": v(-47.32, -123.48) * mm});
            skLineSegment(sketch, "E403", {"start": v(-47.32, -123.48) * mm, "end": v(-47.78, -123.18) * mm});
            skLineSegment(sketch, "E404", {"start": v(-47.78, -123.18) * mm, "end": v(-48.19, -122.8) * mm});
            skLineSegment(sketch, "E405", {"start": v(-48.19, -122.8) * mm, "end": v(-48.52, -122.35) * mm});
            skLineSegment(sketch, "E406", {"start": v(-48.52, -122.35) * mm, "end": v(-48.78, -121.84) * mm});
            skLineSegment(sketch, "E407", {"start": v(-48.78, -121.84) * mm, "end": v(-48.94, -121.29) * mm});
            skLineSegment(sketch, "E408", {"start": v(-48.94, -121.29) * mm, "end": v(-49.03, -120.77) * mm});
            skLineSegment(sketch, "E409", {"start": v(-49.03, -120.77) * mm, "end": v(-49.12, -120.25) * mm});
            skLineSegment(sketch, "E410", {"start": v(-49.12, -120.25) * mm, "end": v(-49.2, -119.73) * mm});
            skLineSegment(sketch, "E411", {"start": v(-49.2, -119.73) * mm, "end": v(-49.26, -119.21) * mm});
            skLineSegment(sketch, "E412", {"start": v(-49.26, -119.21) * mm, "end": v(-49.3, -118.69) * mm});
            skLineSegment(sketch, "E413", {"start": v(-49.3, -118.69) * mm, "end": v(-49.3, -118.17) * mm});
            skLineSegment(sketch, "E414", {"start": v(-49.3, -118.17) * mm, "end": v(-49.28, -117.66) * mm});
            skLineSegment(sketch, "E415", {"start": v(-49.28, -117.66) * mm, "end": v(-49.23, -117.16) * mm});
            skLineSegment(sketch, "E416", {"start": v(-49.23, -117.16) * mm, "end": v(-48.92, -115.28) * mm});
            skLineSegment(sketch, "E417", {"start": v(-48.92, -115.28) * mm, "end": v(-48.62, -113.4) * mm});
            skLineSegment(sketch, "E418", {"start": v(-48.62, -113.4) * mm, "end": v(-48.3, -111.53) * mm});
            skLineSegment(sketch, "E419", {"start": v(-48.3, -111.53) * mm, "end": v(-47.97, -109.66) * mm});
            skLineSegment(sketch, "E420", {"start": v(-47.97, -109.66) * mm, "end": v(-47.62, -107.8) * mm});
            skLineSegment(sketch, "E421", {"start": v(-47.62, -107.8) * mm, "end": v(-47.25, -105.93) * mm});
            skLineSegment(sketch, "E422", {"start": v(-47.25, -105.93) * mm, "end": v(-46.85, -104.07) * mm});
            skLineSegment(sketch, "E423", {"start": v(-46.85, -104.07) * mm, "end": v(-46.43, -102.22) * mm});
            skLineSegment(sketch, "E424", {"start": v(-46.43, -102.22) * mm, "end": v(-45.9, -100.1) * mm});
            skLineSegment(sketch, "E425", {"start": v(-45.9, -100.1) * mm, "end": v(-45.34, -98) * mm});
            skLineSegment(sketch, "E426", {"start": v(-45.34, -98) * mm, "end": v(-44.75, -95.89) * mm});
            skLineSegment(sketch, "E427", {"start": v(-44.75, -95.89) * mm, "end": v(-44.15, -93.78) * mm});
            skLineSegment(sketch, "E428", {"start": v(-44.15, -93.78) * mm, "end": v(-43.55, -91.68) * mm});
            skLineSegment(sketch, "E429", {"start": v(-43.55, -91.68) * mm, "end": v(-42.94, -89.58) * mm});
            skLineSegment(sketch, "E430", {"start": v(-42.94, -89.58) * mm, "end": v(-42.33, -87.48) * mm});
            skLineSegment(sketch, "E431", {"start": v(-42.33, -87.48) * mm, "end": v(-41.74, -85.38) * mm});
            skLineSegment(sketch, "E432", {"start": v(-41.74, -85.38) * mm, "end": v(-41.55, -84.66) * mm});
            skLineSegment(sketch, "E433", {"start": v(-41.55, -84.66) * mm, "end": v(-41.37, -83.94) * mm});
            skLineSegment(sketch, "E434", {"start": v(-41.37, -83.94) * mm, "end": v(-41.2, -83.22) * mm});
            skLineSegment(sketch, "E435", {"start": v(-41.2, -83.22) * mm, "end": v(-41.03, -82.5) * mm});
            skLineSegment(sketch, "E436", {"start": v(-41.03, -82.5) * mm, "end": v(-40.87, -81.77) * mm});
            skLineSegment(sketch, "E437", {"start": v(-40.87, -81.77) * mm, "end": v(-40.72, -81.05) * mm});
            skLineSegment(sketch, "E438", {"start": v(-40.72, -81.05) * mm, "end": v(-40.59, -80.32) * mm});
            skLineSegment(sketch, "E439", {"start": v(-40.59, -80.32) * mm, "end": v(-40.46, -79.59) * mm});
            skLineSegment(sketch, "E440", {"start": v(-40.46, -79.59) * mm, "end": v(-40.42, -78.75) * mm});
            skLineSegment(sketch, "E441", {"start": v(-40.42, -78.75) * mm, "end": v(-40.54, -77.97) * mm});
            skLineSegment(sketch, "E442", {"start": v(-40.54, -77.97) * mm, "end": v(-40.81, -77.26) * mm});
            skLineSegment(sketch, "E443", {"start": v(-40.81, -77.26) * mm, "end": v(-41.23, -76.65) * mm});
            skLineSegment(sketch, "E444", {"start": v(-41.23, -76.65) * mm, "end": v(-41.77, -76.15) * mm});
            skLineSegment(sketch, "E445", {"start": v(-41.77, -76.15) * mm, "end": v(-42.43, -75.77) * mm});
            skLineSegment(sketch, "E446", {"start": v(-42.43, -75.77) * mm, "end": v(-43.19, -75.53) * mm});
            skLineSegment(sketch, "E447", {"start": v(-43.19, -75.53) * mm, "end": v(-44.03, -75.44) * mm});
            skLineSegment(sketch, "E448", {"start": v(-44.03, -75.44) * mm, "end": v(-44.75, -75.46) * mm});
            skLineSegment(sketch, "E449", {"start": v(-44.75, -75.46) * mm, "end": v(-45.48, -75.5) * mm});
            skLineSegment(sketch, "E450", {"start": v(-45.48, -75.5) * mm, "end": v(-46.2, -75.56) * mm});
            skLineSegment(sketch, "E451", {"start": v(-46.2, -75.56) * mm, "end": v(-46.93, -75.65) * mm});
            skLineSegment(sketch, "E452", {"start": v(-46.93, -75.65) * mm, "end": v(-47.66, -75.76) * mm});
            skLineSegment(sketch, "E453", {"start": v(-47.66, -75.76) * mm, "end": v(-48.38, -75.9) * mm});
            skLineSegment(sketch, "E454", {"start": v(-48.38, -75.9) * mm, "end": v(-49.09, -76.07) * mm});
            skLineSegment(sketch, "E455", {"start": v(-49.09, -76.07) * mm, "end": v(-49.79, -76.26) * mm});
            skLineSegment(sketch, "E456", {"start": v(-49.79, -76.26) * mm, "end": v(-50.98, -76.66) * mm});
            skLineSegment(sketch, "E457", {"start": v(-50.98, -76.66) * mm, "end": v(-52.09, -77.16) * mm});
            skLineSegment(sketch, "E458", {"start": v(-52.09, -77.16) * mm, "end": v(-53.1, -77.77) * mm});
            skLineSegment(sketch, "E459", {"start": v(-53.1, -77.77) * mm, "end": v(-53.99, -78.5) * mm});
            skLineSegment(sketch, "E460", {"start": v(-53.99, -78.5) * mm, "end": v(-54.75, -79.36) * mm});
            skLineSegment(sketch, "E461", {"start": v(-54.75, -79.36) * mm, "end": v(-55.37, -80.36) * mm});
            skLineSegment(sketch, "E462", {"start": v(-55.37, -80.36) * mm, "end": v(-55.84, -81.51) * mm});
            skLineSegment(sketch, "E463", {"start": v(-55.84, -81.51) * mm, "end": v(-56.13, -82.82) * mm});
            skLineSegment(sketch, "E464", {"start": v(-56.13, -82.82) * mm, "end": v(-56.16, -83.03) * mm});
            skLineSegment(sketch, "E465", {"start": v(-56.16, -83.03) * mm, "end": v(-56.21, -83.23) * mm});
            skLineSegment(sketch, "E466", {"start": v(-56.21, -83.23) * mm, "end": v(-56.27, -83.43) * mm});
            skLineSegment(sketch, "E467", {"start": v(-56.27, -83.43) * mm, "end": v(-56.33, -83.63) * mm});
            skLineSegment(sketch, "E468", {"start": v(-56.33, -83.63) * mm, "end": v(-56.4, -83.83) * mm});
            skLineSegment(sketch, "E469", {"start": v(-56.4, -83.83) * mm, "end": v(-56.46, -84.03) * mm});
            skLineSegment(sketch, "E470", {"start": v(-56.46, -84.03) * mm, "end": v(-56.52, -84.23) * mm});
            skLineSegment(sketch, "E471", {"start": v(-56.52, -84.23) * mm, "end": v(-56.58, -84.43) * mm});
            skLineSegment(sketch, "E472", {"start": v(-56.58, -84.43) * mm, "end": v(-57.3, -86.9) * mm});
            skLineSegment(sketch, "E473", {"start": v(-57.3, -86.9) * mm, "end": v(-58.03, -89.34) * mm});
            skLineSegment(sketch, "E474", {"start": v(-58.03, -89.34) * mm, "end": v(-58.76, -91.8) * mm});
            skLineSegment(sketch, "E475", {"start": v(-58.76, -91.8) * mm, "end": v(-59.48, -94.25) * mm});
            skLineSegment(sketch, "E476", {"start": v(-59.48, -94.25) * mm, "end": v(-60.2, -96.71) * mm});
            skLineSegment(sketch, "E477", {"start": v(-60.2, -96.71) * mm, "end": v(-60.9, -99.17) * mm});
            skLineSegment(sketch, "E478", {"start": v(-60.9, -99.17) * mm, "end": v(-61.6, -101.63) * mm});
            skLineSegment(sketch, "E479", {"start": v(-61.6, -101.63) * mm, "end": v(-62.26, -104.1) * mm});
            skLineSegment(sketch, "E480", {"start": v(-62.26, -104.1) * mm, "end": v(-62.56, -105.32) * mm});
            skLineSegment(sketch, "E481", {"start": v(-62.56, -105.32) * mm, "end": v(-62.82, -106.55) * mm});
            skLineSegment(sketch, "E482", {"start": v(-62.82, -106.55) * mm, "end": v(-63.06, -107.78) * mm});
            skLineSegment(sketch, "E483", {"start": v(-63.06, -107.78) * mm, "end": v(-63.27, -109.03) * mm});
            skLineSegment(sketch, "E484", {"start": v(-63.27, -109.03) * mm, "end": v(-63.47, -110.27) * mm});
            skLineSegment(sketch, "E485", {"start": v(-63.47, -110.27) * mm, "end": v(-63.67, -111.51) * mm});
            skLineSegment(sketch, "E486", {"start": v(-63.67, -111.51) * mm, "end": v(-63.88, -112.76) * mm});
            skLineSegment(sketch, "E487", {"start": v(-63.88, -112.76) * mm, "end": v(-64.1, -114) * mm});
            skLineSegment(sketch, "E488", {"start": v(-64.1, -114) * mm, "end": v(-64.15, -114.16) * mm});
            skLineSegment(sketch, "E489", {"start": v(-64.15, -114.16) * mm, "end": v(-64.2, -114.34) * mm});
            skLineSegment(sketch, "E490", {"start": v(-64.2, -114.34) * mm, "end": v(-64.29, -114.5) * mm});
            skLineSegment(sketch, "E491", {"start": v(-64.29, -114.5) * mm, "end": v(-64.38, -114.67) * mm});
            skLineSegment(sketch, "E492", {"start": v(-64.38, -114.67) * mm, "end": v(-64.5, -114.83) * mm});
            skLineSegment(sketch, "E493", {"start": v(-64.5, -114.83) * mm, "end": v(-64.61, -114.97) * mm});
            skLineSegment(sketch, "E494", {"start": v(-64.61, -114.97) * mm, "end": v(-64.74, -115.1) * mm});
            skLineSegment(sketch, "E495", {"start": v(-64.74, -115.1) * mm, "end": v(-64.88, -115.2) * mm});
            skLineSegment(sketch, "E496", {"start": v(-64.88, -115.2) * mm, "end": v(-65.72, -115.72) * mm});
            skLineSegment(sketch, "E497", {"start": v(-65.72, -115.72) * mm, "end": v(-66.55, -116.25) * mm});
            skLineSegment(sketch, "E498", {"start": v(-66.55, -116.25) * mm, "end": v(-67.4, -116.77) * mm});
            skLineSegment(sketch, "E499", {"start": v(-67.4, -116.77) * mm, "end": v(-68.24, -117.29) * mm});
            skLineSegment(sketch, "E500", {"start": v(-68.24, -117.29) * mm, "end": v(-69.08, -117.8) * mm});
            skLineSegment(sketch, "E501", {"start": v(-69.08, -117.8) * mm, "end": v(-69.94, -118.3) * mm});
            skLineSegment(sketch, "E502", {"start": v(-69.94, -118.3) * mm, "end": v(-70.8, -118.77) * mm});
            skLineSegment(sketch, "E503", {"start": v(-70.8, -118.77) * mm, "end": v(-71.67, -119.23) * mm});
            skLineSegment(sketch, "E504", {"start": v(-71.67, -119.23) * mm, "end": v(-72.3, -119.54) * mm});
            skLineSegment(sketch, "E505", {"start": v(-72.3, -119.54) * mm, "end": v(-72.94, -119.83) * mm});
            skLineSegment(sketch, "E506", {"start": v(-72.94, -119.83) * mm, "end": v(-73.59, -120.09) * mm});
            skLineSegment(sketch, "E507", {"start": v(-73.59, -120.09) * mm, "end": v(-74.25, -120.34) * mm});
            skLineSegment(sketch, "E508", {"start": v(-74.25, -120.34) * mm, "end": v(-74.9, -120.57) * mm});
            skLineSegment(sketch, "E509", {"start": v(-74.9, -120.57) * mm, "end": v(-75.57, -120.8) * mm});
            skLineSegment(sketch, "E510", {"start": v(-75.57, -120.8) * mm, "end": v(-76.24, -121.02) * mm});
            skLineSegment(sketch, "E511", {"start": v(-76.24, -121.02) * mm, "end": v(-76.9, -121.24) * mm});
            skLineSegment(sketch, "E512", {"start": v(-76.9, -121.24) * mm, "end": v(-77.28, -121.35) * mm});
            skLineSegment(sketch, "E513", {"start": v(-77.28, -121.35) * mm, "end": v(-77.65, -121.4) * mm});
            skLineSegment(sketch, "E514", {"start": v(-77.65, -121.4) * mm, "end": v(-78, -121.4) * mm});
            skLineSegment(sketch, "E515", {"start": v(-78, -121.4) * mm, "end": v(-78.34, -121.33) * mm});
            skLineSegment(sketch, "E516", {"start": v(-78.34, -121.33) * mm, "end": v(-78.66, -121.2) * mm});
            skLineSegment(sketch, "E517", {"start": v(-78.66, -121.2) * mm, "end": v(-78.96, -120.99) * mm});
            skLineSegment(sketch, "E518", {"start": v(-78.96, -120.99) * mm, "end": v(-79.23, -120.7) * mm});
            skLineSegment(sketch, "E519", {"start": v(-79.23, -120.7) * mm, "end": v(-79.47, -120.33) * mm});
            skLineSegment(sketch, "E520", {"start": v(-79.47, -120.33) * mm, "end": v(-80, -119.27) * mm});
            skLineSegment(sketch, "E521", {"start": v(-80, -119.27) * mm, "end": v(-80.47, -118.19) * mm});
            skLineSegment(sketch, "E522", {"start": v(-80.47, -118.19) * mm, "end": v(-80.84, -117.1) * mm});
            skLineSegment(sketch, "E523", {"start": v(-80.84, -117.1) * mm, "end": v(-81.12, -115.98) * mm});
            skLineSegment(sketch, "E524", {"start": v(-81.12, -115.98) * mm, "end": v(-81.3, -114.85) * mm});
            skLineSegment(sketch, "E525", {"start": v(-81.3, -114.85) * mm, "end": v(-81.4, -113.7) * mm});
            skLineSegment(sketch, "E526", {"start": v(-81.4, -113.7) * mm, "end": v(-81.4, -112.53) * mm});
            skLineSegment(sketch, "E527", {"start": v(-81.4, -112.53) * mm, "end": v(-81.28, -111.34) * mm});
            skLineSegment(sketch, "E528", {"start": v(-81.28, -111.34) * mm, "end": v(-80.92, -109.37) * mm});
            skLineSegment(sketch, "E529", {"start": v(-80.92, -109.37) * mm, "end": v(-80.42, -107.46) * mm});
            skLineSegment(sketch, "E530", {"start": v(-80.42, -107.46) * mm, "end": v(-79.8, -105.6) * mm});
            skLineSegment(sketch, "E531", {"start": v(-79.8, -105.6) * mm, "end": v(-79.06, -103.77) * mm});
            skLineSegment(sketch, "E532", {"start": v(-79.06, -103.77) * mm, "end": v(-78.24, -101.98) * mm});
            skLineSegment(sketch, "E533", {"start": v(-78.24, -101.98) * mm, "end": v(-77.36, -100.22) * mm});
            skLineSegment(sketch, "E534", {"start": v(-77.36, -100.22) * mm, "end": v(-76.43, -98.47) * mm});
            skLineSegment(sketch, "E535", {"start": v(-76.43, -98.47) * mm, "end": v(-75.48, -96.74) * mm});
            skLineSegment(sketch, "E536", {"start": v(-75.48, -96.74) * mm, "end": v(-73.43, -93.03) * mm});
            skLineSegment(sketch, "E537", {"start": v(-73.43, -93.03) * mm, "end": v(-71.38, -89.32) * mm});
            skLineSegment(sketch, "E538", {"start": v(-71.38, -89.32) * mm, "end": v(-69.33, -85.6) * mm});
            skLineSegment(sketch, "E539", {"start": v(-69.33, -85.6) * mm, "end": v(-67.29, -81.9) * mm});
            skLineSegment(sketch, "E540", {"start": v(-67.29, -81.9) * mm, "end": v(-65.26, -78.17) * mm});
            skLineSegment(sketch, "E541", {"start": v(-65.26, -78.17) * mm, "end": v(-63.24, -74.44) * mm});
            skLineSegment(sketch, "E542", {"start": v(-63.24, -74.44) * mm, "end": v(-61.26, -70.7) * mm});
            skLineSegment(sketch, "E543", {"start": v(-61.26, -70.7) * mm, "end": v(-59.3, -66.94) * mm});
            skLineSegment(sketch, "E544", {"start": v(-59.3, -66.94) * mm, "end": v(-58.8, -65.9) * mm});
            skLineSegment(sketch, "E545", {"start": v(-58.8, -65.9) * mm, "end": v(-58.26, -64.68) * mm});
            skLineSegment(sketch, "E546", {"start": v(-58.26, -64.68) * mm, "end": v(-57.7, -63.34) * mm});
            skLineSegment(sketch, "E547", {"start": v(-57.7, -63.34) * mm, "end": v(-57.14, -61.92) * mm});
            skLineSegment(sketch, "E548", {"start": v(-57.14, -61.92) * mm, "end": v(-56.6, -60.5) * mm});
            skLineSegment(sketch, "E549", {"start": v(-56.6, -60.5) * mm, "end": v(-56.06, -59.15) * mm});
            skLineSegment(sketch, "E550", {"start": v(-56.06, -59.15) * mm, "end": v(-55.57, -57.91) * mm});
            skLineSegment(sketch, "E551", {"start": v(-55.57, -57.91) * mm, "end": v(-55.13, -56.85) * mm});
            skLineSegment(sketch, "E552", {"start": v(-55.13, -56.85) * mm, "end": v(-54.92, -58.06) * mm});
            skLineSegment(sketch, "E553", {"start": v(-54.92, -58.06) * mm, "end": v(-54.65, -59.24) * mm});
            skLineSegment(sketch, "E554", {"start": v(-54.65, -59.24) * mm, "end": v(-54.32, -60.38) * mm});
            skLineSegment(sketch, "E555", {"start": v(-54.32, -60.38) * mm, "end": v(-53.9, -61.5) * mm});
            skLineSegment(sketch, "E556", {"start": v(-53.9, -61.5) * mm, "end": v(-53.4, -62.55) * mm});
            skLineSegment(sketch, "E557", {"start": v(-53.4, -62.55) * mm, "end": v(-52.8, -63.56) * mm});
            skLineSegment(sketch, "E558", {"start": v(-52.8, -63.56) * mm, "end": v(-52.1, -64.52) * mm});
            skLineSegment(sketch, "E559", {"start": v(-52.1, -64.52) * mm, "end": v(-51.26, -65.41) * mm});
            skLineSegment(sketch, "E560", {"start": v(-51.26, -65.41) * mm, "end": v(-50.57, -65.96) * mm});
            skLineSegment(sketch, "E561", {"start": v(-50.57, -65.96) * mm, "end": v(-49.7, -66.48) * mm});
            skLineSegment(sketch, "E562", {"start": v(-49.7, -66.48) * mm, "end": v(-48.7, -66.96) * mm});
            skLineSegment(sketch, "E563", {"start": v(-48.7, -66.96) * mm, "end": v(-47.64, -67.4) * mm});
            skLineSegment(sketch, "E564", {"start": v(-47.64, -67.4) * mm, "end": v(-46.55, -67.8) * mm});
            skLineSegment(sketch, "E565", {"start": v(-46.55, -67.8) * mm, "end": v(-45.5, -68.12) * mm});
            skLineSegment(sketch, "E566", {"start": v(-45.5, -68.12) * mm, "end": v(-44.53, -68.4) * mm});
            skLineSegment(sketch, "E567", {"start": v(-44.53, -68.4) * mm, "end": v(-43.7, -68.6) * mm});
            skLineSegment(sketch, "E568", {"start": v(-43.7, -68.6) * mm, "end": v(-40.9, -68.59) * mm});
            skLineSegment(sketch, "E569", {"start": v(-40.9, -68.59) * mm, "end": v(-38.38, -68.08) * mm});
            skLineSegment(sketch, "E570", {"start": v(-38.38, -68.08) * mm, "end": v(-36.15, -67.1) * mm});
            skLineSegment(sketch, "E571", {"start": v(-36.15, -67.1) * mm, "end": v(-34.22, -65.73) * mm});
            skLineSegment(sketch, "E572", {"start": v(-34.22, -65.73) * mm, "end": v(-32.63, -63.99) * mm});
            skLineSegment(sketch, "E573", {"start": v(-32.63, -63.99) * mm, "end": v(-31.37, -61.93) * mm});
            skLineSegment(sketch, "E574", {"start": v(-31.37, -61.93) * mm, "end": v(-30.47, -59.6) * mm});
            skLineSegment(sketch, "E575", {"start": v(-30.47, -59.6) * mm, "end": v(-29.95, -57.04) * mm});
            skLineSegment(sketch, "E576", {"start": v(-29.95, -57.04) * mm, "end": v(-29.9, -55.09) * mm});
            skLineSegment(sketch, "E577", {"start": v(-29.9, -55.09) * mm, "end": v(-30.23, -53.26) * mm});
            skLineSegment(sketch, "E578", {"start": v(-30.23, -53.26) * mm, "end": v(-30.92, -51.58) * mm});
            skLineSegment(sketch, "E579", {"start": v(-30.92, -51.58) * mm, "end": v(-31.91, -50.08) * mm});
            skLineSegment(sketch, "E580", {"start": v(-31.91, -50.08) * mm, "end": v(-33.19, -48.77) * mm});
            skLineSegment(sketch, "E581", {"start": v(-33.19, -48.77) * mm, "end": v(-34.7, -47.69) * mm});
            skLineSegment(sketch, "E582", {"start": v(-34.7, -47.69) * mm, "end": v(-36.43, -46.86) * mm});
            skLineSegment(sketch, "E583", {"start": v(-36.43, -46.86) * mm, "end": v(-38.32, -46.3) * mm});
            skLineSegment(sketch, "E584", {"start": v(-38.32, -46.3) * mm, "end": v(-38.91, -46.2) * mm});
            skLineSegment(sketch, "E585", {"start": v(-38.91, -46.2) * mm, "end": v(-39.5, -46.09) * mm});
            skLineSegment(sketch, "E586", {"start": v(-39.5, -46.09) * mm, "end": v(-40.1, -46) * mm});
            skLineSegment(sketch, "E587", {"start": v(-40.1, -46) * mm, "end": v(-40.7, -45.93) * mm});
            skLineSegment(sketch, "E588", {"start": v(-40.7, -45.93) * mm, "end": v(-41.3, -45.88) * mm});
            skLineSegment(sketch, "E589", {"start": v(-41.3, -45.88) * mm, "end": v(-41.9, -45.85) * mm});
            skLineSegment(sketch, "E590", {"start": v(-41.9, -45.85) * mm, "end": v(-42.5, -45.83) * mm});
            skLineSegment(sketch, "E591", {"start": v(-42.5, -45.83) * mm, "end": v(-43.1, -45.84) * mm});
            skLineSegment(sketch, "E592", {"start": v(-43.1, -45.84) * mm, "end": v(-44.41, -45.91) * mm});
            skLineSegment(sketch, "E593", {"start": v(-44.41, -45.91) * mm, "end": v(-45.67, -46.07) * mm});
            skLineSegment(sketch, "E594", {"start": v(-45.67, -46.07) * mm, "end": v(-46.88, -46.32) * mm});
            skLineSegment(sketch, "E595", {"start": v(-46.88, -46.32) * mm, "end": v(-48.04, -46.67) * mm});
            skLineSegment(sketch, "E596", {"start": v(-48.04, -46.67) * mm, "end": v(-49.14, -47.11) * mm});
            skLineSegment(sketch, "E597", {"start": v(-49.14, -47.11) * mm, "end": v(-50.19, -47.66) * mm});
            skLineSegment(sketch, "E598", {"start": v(-50.19, -47.66) * mm, "end": v(-51.16, -48.3) * mm});
            skLineSegment(sketch, "E599", {"start": v(-51.16, -48.3) * mm, "end": v(-52.08, -49.07) * mm});
            skLineSegment(sketch, "E600", {"start": v(-52.08, -49.07) * mm, "end": v(-51.71, -47.75) * mm});
            skLineSegment(sketch, "E601", {"start": v(-51.71, -47.75) * mm, "end": v(-51.38, -46.42) * mm});
            skLineSegment(sketch, "E602", {"start": v(-51.38, -46.42) * mm, "end": v(-51.06, -45.09) * mm});
            skLineSegment(sketch, "E603", {"start": v(-51.06, -45.09) * mm, "end": v(-50.77, -43.75) * mm});
            skLineSegment(sketch, "E604", {"start": v(-50.77, -43.75) * mm, "end": v(-50.5, -42.4) * mm});
            skLineSegment(sketch, "E605", {"start": v(-50.5, -42.4) * mm, "end": v(-50.26, -41.04) * mm});
            skLineSegment(sketch, "E606", {"start": v(-50.26, -41.04) * mm, "end": v(-50.05, -39.68) * mm});
            skLineSegment(sketch, "E607", {"start": v(-50.05, -39.68) * mm, "end": v(-49.86, -38.3) * mm});
            skLineSegment(sketch, "E608", {"start": v(-49.86, -38.3) * mm, "end": v(-49.7, -36.85) * mm});
            skLineSegment(sketch, "E609", {"start": v(-49.7, -36.85) * mm, "end": v(-49.57, -35.4) * mm});
            skLineSegment(sketch, "E610", {"start": v(-49.57, -35.4) * mm, "end": v(-49.49, -33.96) * mm});
            skLineSegment(sketch, "E611", {"start": v(-49.49, -33.96) * mm, "end": v(-49.46, -32.51) * mm});
            skLineSegment(sketch, "E612", {"start": v(-49.46, -32.51) * mm, "end": v(-49.51, -31.07) * mm});
            skLineSegment(sketch, "E613", {"start": v(-49.51, -31.07) * mm, "end": v(-49.64, -29.62) * mm});
            skLineSegment(sketch, "E614", {"start": v(-49.64, -29.62) * mm, "end": v(-49.86, -28.18) * mm});
            skLineSegment(sketch, "E615", {"start": v(-49.86, -28.18) * mm, "end": v(-50.19, -26.75) * mm});
            skLineSegment(sketch, "E616", {"start": v(-50.19, -26.75) * mm, "end": v(-50.73, -25.12) * mm});
            skLineSegment(sketch, "E617", {"start": v(-50.73, -25.12) * mm, "end": v(-51.45, -23.7) * mm});
            skLineSegment(sketch, "E618", {"start": v(-51.45, -23.7) * mm, "end": v(-52.34, -22.49) * mm});
            skLineSegment(sketch, "E619", {"start": v(-52.34, -22.49) * mm, "end": v(-53.4, -21.5) * mm});
            skLineSegment(sketch, "E620", {"start": v(-53.4, -21.5) * mm, "end": v(-54.63, -20.75) * mm});
            skLineSegment(sketch, "E621", {"start": v(-54.63, -20.75) * mm, "end": v(-56.02, -20.23) * mm});
            skLineSegment(sketch, "E622", {"start": v(-56.02, -20.23) * mm, "end": v(-57.56, -19.95) * mm});
            skLineSegment(sketch, "E623", {"start": v(-57.56, -19.95) * mm, "end": v(-59.27, -19.92) * mm});
            skLineSegment(sketch, "E624", {"start": v(-59.27, -19.92) * mm, "end": v(-60.05, -19.99) * mm});
            skLineSegment(sketch, "E625", {"start": v(-60.05, -19.99) * mm, "end": v(-60.83, -20.1) * mm});
            skLineSegment(sketch, "E626", {"start": v(-60.83, -20.1) * mm, "end": v(-61.6, -20.24) * mm});
            skLineSegment(sketch, "E627", {"start": v(-61.6, -20.24) * mm, "end": v(-62.38, -20.42) * mm});
            skLineSegment(sketch, "E628", {"start": v(-62.38, -20.42) * mm, "end": v(-63.14, -20.64) * mm});
            skLineSegment(sketch, "E629", {"start": v(-63.14, -20.64) * mm, "end": v(-63.9, -20.88) * mm});
            skLineSegment(sketch, "E630", {"start": v(-63.9, -20.88) * mm, "end": v(-64.64, -21.16) * mm});
            skLineSegment(sketch, "E631", {"start": v(-64.64, -21.16) * mm, "end": v(-65.36, -21.46) * mm});
            skLineSegment(sketch, "E632", {"start": v(-65.36, -21.46) * mm, "end": v(-66.72, -22.12) * mm});
            skLineSegment(sketch, "E633", {"start": v(-66.72, -22.12) * mm, "end": v(-68, -22.89) * mm});
            skLineSegment(sketch, "E634", {"start": v(-68, -22.89) * mm, "end": v(-69.23, -23.74) * mm});
            skLineSegment(sketch, "E635", {"start": v(-69.23, -23.74) * mm, "end": v(-70.39, -24.68) * mm});
            skLineSegment(sketch, "E636", {"start": v(-70.39, -24.68) * mm, "end": v(-71.5, -25.68) * mm});
            skLineSegment(sketch, "E637", {"start": v(-71.5, -25.68) * mm, "end": v(-72.56, -26.74) * mm});
            skLineSegment(sketch, "E638", {"start": v(-72.56, -26.74) * mm, "end": v(-73.57, -27.85) * mm});
            skLineSegment(sketch, "E639", {"start": v(-73.57, -27.85) * mm, "end": v(-74.55, -29) * mm});
            skLineSegment(sketch, "E640", {"start": v(-74.55, -29) * mm, "end": v(-76.89, -31.98) * mm});
            skLineSegment(sketch, "E641", {"start": v(-76.89, -31.98) * mm, "end": v(-79.05, -35.06) * mm});
            skLineSegment(sketch, "E642", {"start": v(-79.05, -35.06) * mm, "end": v(-81.06, -38.23) * mm});
            skLineSegment(sketch, "E643", {"start": v(-81.06, -38.23) * mm, "end": v(-82.9, -41.49) * mm});
            skLineSegment(sketch, "E644", {"start": v(-82.9, -41.49) * mm, "end": v(-84.6, -44.82) * mm});
            skLineSegment(sketch, "E645", {"start": v(-84.6, -44.82) * mm, "end": v(-86.15, -48.24) * mm});
            skLineSegment(sketch, "E646", {"start": v(-86.15, -48.24) * mm, "end": v(-87.56, -51.73) * mm});
            skLineSegment(sketch, "E647", {"start": v(-87.56, -51.73) * mm, "end": v(-88.83, -55.28) * mm});
            skLineSegment(sketch, "E648", {"start": v(-88.83, -55.28) * mm, "end": v(-90.05, -59.06) * mm});
            skLineSegment(sketch, "E649", {"start": v(-90.05, -59.06) * mm, "end": v(-91.19, -62.86) * mm});
            skLineSegment(sketch, "E650", {"start": v(-91.19, -62.86) * mm, "end": v(-92.24, -66.69) * mm});
            skLineSegment(sketch, "E651", {"start": v(-92.24, -66.69) * mm, "end": v(-93.21, -70.53) * mm});
            skLineSegment(sketch, "E652", {"start": v(-93.21, -70.53) * mm, "end": v(-94.1, -74.4) * mm});
            skLineSegment(sketch, "E653", {"start": v(-94.1, -74.4) * mm, "end": v(-94.92, -78.27) * mm});
            skLineSegment(sketch, "E654", {"start": v(-94.92, -78.27) * mm, "end": v(-95.66, -82.18) * mm});
            skLineSegment(sketch, "E655", {"start": v(-95.66, -82.18) * mm, "end": v(-96.33, -86.1) * mm});
            skLineSegment(sketch, "E656", {"start": v(-96.33, -86.1) * mm, "end": v(-96.85, -89.58) * mm});
            skLineSegment(sketch, "E657", {"start": v(-96.85, -89.58) * mm, "end": v(-97.26, -93.07) * mm});
            skLineSegment(sketch, "E658", {"start": v(-97.26, -93.07) * mm, "end": v(-97.56, -96.56) * mm});
            skLineSegment(sketch, "E659", {"start": v(-97.56, -96.56) * mm, "end": v(-97.71, -100.04) * mm});
            skLineSegment(sketch, "E660", {"start": v(-97.71, -100.04) * mm, "end": v(-97.72, -103.52) * mm});
            skLineSegment(sketch, "E661", {"start": v(-97.72, -103.52) * mm, "end": v(-97.55, -107.01) * mm});
            skLineSegment(sketch, "E662", {"start": v(-97.55, -107.01) * mm, "end": v(-97.19, -110.5) * mm});
            skLineSegment(sketch, "E663", {"start": v(-97.19, -110.5) * mm, "end": v(-96.63, -114) * mm});
            skLineSegment(sketch, "E664", {"start": v(-96.63, -114) * mm, "end": v(-96.62, -114.13) * mm});
            skLineSegment(sketch, "E665", {"start": v(-96.62, -114.13) * mm, "end": v(-96.64, -114.29) * mm});
            skLineSegment(sketch, "E666", {"start": v(-96.64, -114.29) * mm, "end": v(-96.69, -114.45) * mm});
            skLineSegment(sketch, "E667", {"start": v(-96.69, -114.45) * mm, "end": v(-96.76, -114.62) * mm});
            skLineSegment(sketch, "E668", {"start": v(-96.76, -114.62) * mm, "end": v(-96.84, -114.77) * mm});
            skLineSegment(sketch, "E669", {"start": v(-96.84, -114.77) * mm, "end": v(-96.94, -114.92) * mm});
            skLineSegment(sketch, "E670", {"start": v(-96.94, -114.92) * mm, "end": v(-97.05, -115.03) * mm});
            skLineSegment(sketch, "E671", {"start": v(-97.05, -115.03) * mm, "end": v(-97.16, -115.12) * mm});
            skLineSegment(sketch, "E672", {"start": v(-97.16, -115.12) * mm, "end": v(-98.41, -115.86) * mm});
            skLineSegment(sketch, "E673", {"start": v(-98.41, -115.86) * mm, "end": v(-99.66, -116.6) * mm});
            skLineSegment(sketch, "E674", {"start": v(-99.66, -116.6) * mm, "end": v(-100.9, -117.34) * mm});
            skLineSegment(sketch, "E675", {"start": v(-100.9, -117.34) * mm, "end": v(-102.16, -118.07) * mm});
            skLineSegment(sketch, "E676", {"start": v(-102.16, -118.07) * mm, "end": v(-103.42, -118.79) * mm});
            skLineSegment(sketch, "E677", {"start": v(-103.42, -118.79) * mm, "end": v(-104.68, -119.5) * mm});
            skLineSegment(sketch, "E678", {"start": v(-104.68, -119.5) * mm, "end": v(-105.94, -120.22) * mm});
            skLineSegment(sketch, "E679", {"start": v(-105.94, -120.22) * mm, "end": v(-107.2, -120.92) * mm});
            skLineSegment(sketch, "E680", {"start": v(-107.2, -120.92) * mm, "end": v(-107.6, -121.11) * mm});
            skLineSegment(sketch, "E681", {"start": v(-107.6, -121.11) * mm, "end": v(-108, -121.28) * mm});
            skLineSegment(sketch, "E682", {"start": v(-108, -121.28) * mm, "end": v(-108.4, -121.44) * mm});
            skLineSegment(sketch, "E683", {"start": v(-108.4, -121.44) * mm, "end": v(-108.83, -121.57) * mm});
            skLineSegment(sketch, "E684", {"start": v(-108.83, -121.57) * mm, "end": v(-109.26, -121.7) * mm});
            skLineSegment(sketch, "E685", {"start": v(-109.26, -121.7) * mm, "end": v(-109.69, -121.8) * mm});
            skLineSegment(sketch, "E686", {"start": v(-109.69, -121.8) * mm, "end": v(-110.12, -121.9) * mm});
            skLineSegment(sketch, "E687", {"start": v(-110.12, -121.9) * mm, "end": v(-110.55, -122) * mm});
            skLineSegment(sketch, "E688", {"start": v(-110.55, -122) * mm, "end": v(-111.18, -122.06) * mm});
            skLineSegment(sketch, "E689", {"start": v(-111.18, -122.06) * mm, "end": v(-111.79, -122) * mm});
            skLineSegment(sketch, "E690", {"start": v(-111.79, -122) * mm, "end": v(-112.36, -121.83) * mm});
            skLineSegment(sketch, "E691", {"start": v(-112.36, -121.83) * mm, "end": v(-112.87, -121.54) * mm});
            skLineSegment(sketch, "E692", {"start": v(-112.87, -121.54) * mm, "end": v(-113.32, -121.16) * mm});
            skLineSegment(sketch, "E693", {"start": v(-113.32, -121.16) * mm, "end": v(-113.68, -120.7) * mm});
            skLineSegment(sketch, "E694", {"start": v(-113.68, -120.7) * mm, "end": v(-113.95, -120.15) * mm});
            skLineSegment(sketch, "E695", {"start": v(-113.95, -120.15) * mm, "end": v(-114.1, -119.54) * mm});
            skLineSegment(sketch, "E696", {"start": v(-114.1, -119.54) * mm, "end": v(-114.21, -118.76) * mm});
            skLineSegment(sketch, "E697", {"start": v(-114.21, -118.76) * mm, "end": v(-114.31, -117.98) * mm});
            skLineSegment(sketch, "E698", {"start": v(-114.31, -117.98) * mm, "end": v(-114.39, -117.2) * mm});
            skLineSegment(sketch, "E699", {"start": v(-114.39, -117.2) * mm, "end": v(-114.45, -116.41) * mm});
            skLineSegment(sketch, "E700", {"start": v(-114.45, -116.41) * mm, "end": v(-114.47, -115.63) * mm});
            skLineSegment(sketch, "E701", {"start": v(-114.47, -115.63) * mm, "end": v(-114.47, -114.85) * mm});
            skLineSegment(sketch, "E702", {"start": v(-114.47, -114.85) * mm, "end": v(-114.42, -114.08) * mm});
            skLineSegment(sketch, "E703", {"start": v(-114.42, -114.08) * mm, "end": v(-114.33, -113.31) * mm});
            skLineSegment(sketch, "E704", {"start": v(-114.33, -113.31) * mm, "end": v(-114, -111.17) * mm});
            skLineSegment(sketch, "E705", {"start": v(-114, -111.17) * mm, "end": v(-113.65, -109.03) * mm});
            skLineSegment(sketch, "E706", {"start": v(-113.65, -109.03) * mm, "end": v(-113.28, -106.89) * mm});
            skLineSegment(sketch, "E707", {"start": v(-113.28, -106.89) * mm, "end": v(-112.9, -104.75) * mm});
            skLineSegment(sketch, "E708", {"start": v(-112.9, -104.75) * mm, "end": v(-112.5, -102.62) * mm});
            skLineSegment(sketch, "E709", {"start": v(-112.5, -102.62) * mm, "end": v(-112.1, -100.48) * mm});
            skLineSegment(sketch, "E710", {"start": v(-112.1, -100.48) * mm, "end": v(-111.7, -98.35) * mm});
            skLineSegment(sketch, "E711", {"start": v(-111.7, -98.35) * mm, "end": v(-111.3, -96.21) * mm});
            skLineSegment(sketch, "E712", {"start": v(-111.3, -96.21) * mm, "end": v(-110.9, -94.1) * mm});
            skLineSegment(sketch, "E713", {"start": v(-110.9, -94.1) * mm, "end": v(-110.52, -92) * mm});
            skLineSegment(sketch, "E714", {"start": v(-110.52, -92) * mm, "end": v(-110.15, -89.9) * mm});
            skLineSegment(sketch, "E715", {"start": v(-110.15, -89.9) * mm, "end": v(-109.8, -87.78) * mm});
            skLineSegment(sketch, "E716", {"start": v(-109.8, -87.78) * mm, "end": v(-109.53, -85.66) * mm});
            skLineSegment(sketch, "E717", {"start": v(-109.53, -85.66) * mm, "end": v(-109.32, -83.53) * mm});
            skLineSegment(sketch, "E718", {"start": v(-109.32, -83.53) * mm, "end": v(-109.2, -81.4) * mm});
            skLineSegment(sketch, "E719", {"start": v(-109.2, -81.4) * mm, "end": v(-109.18, -79.24) * mm});
            skLineSegment(sketch, "E720", {"start": v(-109.18, -79.24) * mm, "end": v(-109.23, -78.56) * mm});
            skLineSegment(sketch, "E721", {"start": v(-109.23, -78.56) * mm, "end": v(-109.35, -77.95) * mm});
            skLineSegment(sketch, "E722", {"start": v(-109.35, -77.95) * mm, "end": v(-109.54, -77.4) * mm});
            skLineSegment(sketch, "E723", {"start": v(-109.54, -77.4) * mm, "end": v(-109.8, -76.91) * mm});
            skLineSegment(sketch, "E724", {"start": v(-109.8, -76.91) * mm, "end": v(-110.15, -76.48) * mm});
            skLineSegment(sketch, "E725", {"start": v(-110.15, -76.48) * mm, "end": v(-110.56, -76.11) * mm});
            skLineSegment(sketch, "E726", {"start": v(-110.56, -76.11) * mm, "end": v(-111.06, -75.8) * mm});
            skLineSegment(sketch, "E727", {"start": v(-111.06, -75.8) * mm, "end": v(-111.63, -75.53) * mm});
            skLineSegment(sketch, "E728", {"start": v(-111.63, -75.53) * mm, "end": v(-112.84, -75.13) * mm});
            skLineSegment(sketch, "E729", {"start": v(-112.84, -75.13) * mm, "end": v(-114.04, -74.86) * mm});
            skLineSegment(sketch, "E730", {"start": v(-114.04, -74.86) * mm, "end": v(-115.24, -74.73) * mm});
            skLineSegment(sketch, "E731", {"start": v(-115.24, -74.73) * mm, "end": v(-116.43, -74.73) * mm});
            skLineSegment(sketch, "E732", {"start": v(-116.43, -74.73) * mm, "end": v(-117.62, -74.87) * mm});
            skLineSegment(sketch, "E733", {"start": v(-117.62, -74.87) * mm, "end": v(-118.8, -75.14) * mm});
            skLineSegment(sketch, "E734", {"start": v(-118.8, -75.14) * mm, "end": v(-119.97, -75.55) * mm});
            skLineSegment(sketch, "E735", {"start": v(-119.97, -75.55) * mm, "end": v(-121.12, -76.1) * mm});
            skLineSegment(sketch, "E736", {"start": v(-121.12, -76.1) * mm, "end": v(-121.7, -76.47) * mm});
            skLineSegment(sketch, "E737", {"start": v(-121.7, -76.47) * mm, "end": v(-122.18, -76.92) * mm});
            skLineSegment(sketch, "E738", {"start": v(-122.18, -76.92) * mm, "end": v(-122.55, -77.45) * mm});
            skLineSegment(sketch, "E739", {"start": v(-122.55, -77.45) * mm, "end": v(-122.84, -78.05) * mm});
            skLineSegment(sketch, "E740", {"start": v(-122.84, -78.05) * mm, "end": v(-123.03, -78.73) * mm});
            skLineSegment(sketch, "E741", {"start": v(-123.03, -78.73) * mm, "end": v(-123.15, -79.5) * mm});
            skLineSegment(sketch, "E742", {"start": v(-123.15, -79.5) * mm, "end": v(-123.19, -80.33) * mm});
            skLineSegment(sketch, "E743", {"start": v(-123.19, -80.33) * mm, "end": v(-123.16, -81.25) * mm});
            skLineSegment(sketch, "E744", {"start": v(-123.16, -81.25) * mm, "end": v(-123.13, -84.2) * mm});
            skLineSegment(sketch, "E745", {"start": v(-123.13, -84.2) * mm, "end": v(-123.37, -87.08) * mm});
            skLineSegment(sketch, "E746", {"start": v(-123.37, -87.08) * mm, "end": v(-123.83, -89.93) * mm});
            skLineSegment(sketch, "E747", {"start": v(-123.83, -89.93) * mm, "end": v(-124.46, -92.76) * mm});
            skLineSegment(sketch, "E748", {"start": v(-124.46, -92.76) * mm, "end": v(-125.22, -95.6) * mm});
            skLineSegment(sketch, "E749", {"start": v(-125.22, -95.6) * mm, "end": v(-126.06, -98.44) * mm});
            skLineSegment(sketch, "E750", {"start": v(-126.06, -98.44) * mm, "end": v(-126.93, -101.33) * mm});
            skLineSegment(sketch, "E751", {"start": v(-126.93, -101.33) * mm, "end": v(-127.79, -104.27) * mm});
            skLineSegment(sketch, "E752", {"start": v(-127.79, -104.27) * mm, "end": v(-128.22, -105.87) * mm});
            skLineSegment(sketch, "E753", {"start": v(-128.22, -105.87) * mm, "end": v(-128.6, -107.35) * mm});
            skLineSegment(sketch, "E754", {"start": v(-128.6, -107.35) * mm, "end": v(-128.98, -108.76) * mm});
            skLineSegment(sketch, "E755", {"start": v(-128.98, -108.76) * mm, "end": v(-129.39, -110.1) * mm});
            skLineSegment(sketch, "E756", {"start": v(-129.39, -110.1) * mm, "end": v(-129.87, -111.43) * mm});
            skLineSegment(sketch, "E757", {"start": v(-129.87, -111.43) * mm, "end": v(-130.45, -112.76) * mm});
            skLineSegment(sketch, "E758", {"start": v(-130.45, -112.76) * mm, "end": v(-131.19, -114.13) * mm});
            skLineSegment(sketch, "E759", {"start": v(-131.19, -114.13) * mm, "end": v(-132.11, -115.56) * mm});
            skLineSegment(sketch, "E760", {"start": v(-132.11, -115.56) * mm, "end": v(-132.66, -116.35) * mm});
            skLineSegment(sketch, "E761", {"start": v(-132.66, -116.35) * mm, "end": v(-133.22, -117.16) * mm});
            skLineSegment(sketch, "E762", {"start": v(-133.22, -117.16) * mm, "end": v(-133.81, -117.95) * mm});
            skLineSegment(sketch, "E763", {"start": v(-133.81, -117.95) * mm, "end": v(-134.45, -118.7) * mm});
            skLineSegment(sketch, "E764", {"start": v(-134.45, -118.7) * mm, "end": v(-135.13, -119.4) * mm});
            skLineSegment(sketch, "E765", {"start": v(-135.13, -119.4) * mm, "end": v(-135.89, -119.98) * mm});
            skLineSegment(sketch, "E766", {"start": v(-135.89, -119.98) * mm, "end": v(-136.72, -120.43) * mm});
            skLineSegment(sketch, "E767", {"start": v(-136.72, -120.43) * mm, "end": v(-137.66, -120.72) * mm});
            skLineSegment(sketch, "E768", {"start": v(-137.66, -120.72) * mm, "end": v(-138.3, -120.82) * mm});
            skLineSegment(sketch, "E769", {"start": v(-138.3, -120.82) * mm, "end": v(-138.9, -120.85) * mm});
            skLineSegment(sketch, "E770", {"start": v(-138.9, -120.85) * mm, "end": v(-139.47, -120.8) * mm});
            skLineSegment(sketch, "E771", {"start": v(-139.47, -120.8) * mm, "end": v(-140, -120.66) * mm});
            skLineSegment(sketch, "E772", {"start": v(-140, -120.66) * mm, "end": v(-140.48, -120.42) * mm});
            skLineSegment(sketch, "E773", {"start": v(-140.48, -120.42) * mm, "end": v(-140.91, -120.1) * mm});
            skLineSegment(sketch, "E774", {"start": v(-140.91, -120.1) * mm, "end": v(-141.3, -119.65) * mm});
            skLineSegment(sketch, "E775", {"start": v(-141.3, -119.65) * mm, "end": v(-141.61, -119.1) * mm});
            skLineSegment(sketch, "E776", {"start": v(-141.61, -119.1) * mm, "end": v(-141.85, -118.45) * mm});
            skLineSegment(sketch, "E777", {"start": v(-141.85, -118.45) * mm, "end": v(-142, -117.73) * mm});
            skLineSegment(sketch, "E778", {"start": v(-142, -117.73) * mm, "end": v(-142.06, -116.95) * mm});
            skLineSegment(sketch, "E779", {"start": v(-142.06, -116.95) * mm, "end": v(-142.07, -116.14) * mm});
            skLineSegment(sketch, "E780", {"start": v(-142.07, -116.14) * mm, "end": v(-142.02, -115.32) * mm});
            skLineSegment(sketch, "E781", {"start": v(-142.02, -115.32) * mm, "end": v(-141.93, -114.52) * mm});
            skLineSegment(sketch, "E782", {"start": v(-141.93, -114.52) * mm, "end": v(-141.83, -113.76) * mm});
            skLineSegment(sketch, "E783", {"start": v(-141.83, -113.76) * mm, "end": v(-141.71, -113.07) * mm});
            skLineSegment(sketch, "E784", {"start": v(-141.71, -113.07) * mm, "end": v(-140.93, -108.68) * mm});
            skLineSegment(sketch, "E785", {"start": v(-140.93, -108.68) * mm, "end": v(-140.18, -104.43) * mm});
            skLineSegment(sketch, "E786", {"start": v(-140.18, -104.43) * mm, "end": v(-139.45, -100.28) * mm});
            skLineSegment(sketch, "E787", {"start": v(-139.45, -100.28) * mm, "end": v(-138.72, -96.16) * mm});
            skLineSegment(sketch, "E788", {"start": v(-138.72, -96.16) * mm, "end": v(-138, -92.05) * mm});
            skLineSegment(sketch, "E789", {"start": v(-138, -92.05) * mm, "end": v(-137.27, -87.9) * mm});
            skLineSegment(sketch, "E790", {"start": v(-137.27, -87.9) * mm, "end": v(-136.52, -83.64) * mm});
            skLineSegment(sketch, "E791", {"start": v(-136.52, -83.64) * mm, "end": v(-135.75, -79.25) * mm});
            skLineSegment(sketch, "E792", {"start": v(-135.75, -79.25) * mm, "end": v(-135.7, -78.6) * mm});
            skLineSegment(sketch, "E793", {"start": v(-135.7, -78.6) * mm, "end": v(-135.77, -77.95) * mm});
            skLineSegment(sketch, "E794", {"start": v(-135.77, -77.95) * mm, "end": v(-135.96, -77.34) * mm});
            skLineSegment(sketch, "E795", {"start": v(-135.96, -77.34) * mm, "end": v(-136.25, -76.77) * mm});
            skLineSegment(sketch, "E796", {"start": v(-136.25, -76.77) * mm, "end": v(-136.63, -76.27) * mm});
            skLineSegment(sketch, "E797", {"start": v(-136.63, -76.27) * mm, "end": v(-137.1, -75.84) * mm});
            skLineSegment(sketch, "E798", {"start": v(-137.1, -75.84) * mm, "end": v(-137.66, -75.5) * mm});
            skLineSegment(sketch, "E799", {"start": v(-137.66, -75.5) * mm, "end": v(-138.28, -75.25) * mm});
            skLineSegment(sketch, "E800", {"start": v(-138.28, -75.25) * mm, "end": v(-139.84, -74.9) * mm});
            skLineSegment(sketch, "E801", {"start": v(-139.84, -74.9) * mm, "end": v(-141.3, -74.77) * mm});
            skLineSegment(sketch, "E802", {"start": v(-141.3, -74.77) * mm, "end": v(-142.68, -74.87) * mm});
            skLineSegment(sketch, "E803", {"start": v(-142.68, -74.87) * mm, "end": v(-143.98, -75.2) * mm});
            skLineSegment(sketch, "E804", {"start": v(-143.98, -75.2) * mm, "end": v(-145.19, -75.77) * mm});
            skLineSegment(sketch, "E805", {"start": v(-145.19, -75.77) * mm, "end": v(-146.32, -76.58) * mm});
            skLineSegment(sketch, "E806", {"start": v(-146.32, -76.58) * mm, "end": v(-147.37, -77.62) * mm});
            skLineSegment(sketch, "E807", {"start": v(-147.37, -77.62) * mm, "end": v(-148.36, -78.9) * mm});
            skLineSegment(sketch, "E808", {"start": v(-148.36, -78.9) * mm, "end": v(-149.05, -80.03) * mm});
            skLineSegment(sketch, "E809", {"start": v(-149.05, -80.03) * mm, "end": v(-149.66, -81.2) * mm});
            skLineSegment(sketch, "E810", {"start": v(-149.66, -81.2) * mm, "end": v(-150.2, -82.4) * mm});
            skLineSegment(sketch, "E811", {"start": v(-150.2, -82.4) * mm, "end": v(-150.66, -83.61) * mm});
            skLineSegment(sketch, "E812", {"start": v(-150.66, -83.61) * mm, "end": v(-151.08, -84.85) * mm});
            skLineSegment(sketch, "E813", {"start": v(-151.08, -84.85) * mm, "end": v(-151.47, -86.1) * mm});
            skLineSegment(sketch, "E814", {"start": v(-151.47, -86.1) * mm, "end": v(-151.83, -87.38) * mm});
            skLineSegment(sketch, "E815", {"start": v(-151.83, -87.38) * mm, "end": v(-152.19, -88.65) * mm});
            skLineSegment(sketch, "E816", {"start": v(-152.19, -88.65) * mm, "end": v(-152.67, -90.48) * mm});
            skLineSegment(sketch, "E817", {"start": v(-152.67, -90.48) * mm, "end": v(-153.1, -92.26) * mm});
            skLineSegment(sketch, "E818", {"start": v(-153.1, -92.26) * mm, "end": v(-153.48, -94.02) * mm});
            skLineSegment(sketch, "E819", {"start": v(-153.48, -94.02) * mm, "end": v(-153.82, -95.76) * mm});
            skLineSegment(sketch, "E820", {"start": v(-153.82, -95.76) * mm, "end": v(-154.14, -97.5) * mm});
            skLineSegment(sketch, "E821", {"start": v(-154.14, -97.5) * mm, "end": v(-154.44, -99.27) * mm});
            skLineSegment(sketch, "E822", {"start": v(-154.44, -99.27) * mm, "end": v(-154.75, -101.07) * mm});
            skLineSegment(sketch, "E823", {"start": v(-154.75, -101.07) * mm, "end": v(-155.07, -102.91) * mm});
            skLineSegment(sketch, "E824", {"start": v(-155.07, -102.91) * mm, "end": v(-155.4, -104.64) * mm});
            skLineSegment(sketch, "E825", {"start": v(-155.4, -104.64) * mm, "end": v(-155.73, -106.42) * mm});
            skLineSegment(sketch, "E826", {"start": v(-155.73, -106.42) * mm, "end": v(-156.08, -108.23) * mm});
            skLineSegment(sketch, "E827", {"start": v(-156.08, -108.23) * mm, "end": v(-156.4, -110.06) * mm});
            skLineSegment(sketch, "E828", {"start": v(-156.4, -110.06) * mm, "end": v(-156.7, -111.9) * mm});
            skLineSegment(sketch, "E829", {"start": v(-156.7, -111.9) * mm, "end": v(-156.93, -113.73) * mm});
            skLineSegment(sketch, "E830", {"start": v(-156.93, -113.73) * mm, "end": v(-157.08, -115.54) * mm});
            skLineSegment(sketch, "E831", {"start": v(-157.08, -115.54) * mm, "end": v(-157.12, -117.31) * mm});
            skLineSegment(sketch, "E832", {"start": v(-157.12, -117.31) * mm, "end": v(-157.12, -118.62) * mm});
            skLineSegment(sketch, "E833", {"start": v(-157.12, -118.62) * mm, "end": v(-157.13, -119.92) * mm});
            skLineSegment(sketch, "E834", {"start": v(-157.13, -119.92) * mm, "end": v(-157.13, -121.23) * mm});
            skLineSegment(sketch, "E835", {"start": v(-157.13, -121.23) * mm, "end": v(-157.1, -122.53) * mm});
            skLineSegment(sketch, "E836", {"start": v(-157.1, -122.53) * mm, "end": v(-157.06, -123.83) * mm});
            skLineSegment(sketch, "E837", {"start": v(-157.06, -123.83) * mm, "end": v(-156.99, -125.13) * mm});
            skLineSegment(sketch, "E838", {"start": v(-156.99, -125.13) * mm, "end": v(-156.86, -126.41) * mm});
            skLineSegment(sketch, "E839", {"start": v(-156.86, -126.41) * mm, "end": v(-156.68, -127.7) * mm});
            skLineSegment(sketch, "E840", {"start": v(-156.68, -127.7) * mm, "end": v(-156.19, -129.68) * mm});
            skLineSegment(sketch, "E841", {"start": v(-156.19, -129.68) * mm, "end": v(-155.44, -131.44) * mm});
            skLineSegment(sketch, "E842", {"start": v(-155.44, -131.44) * mm, "end": v(-154.44, -132.94) * mm});
            skLineSegment(sketch, "E843", {"start": v(-154.44, -132.94) * mm, "end": v(-153.22, -134.17) * mm});
            skLineSegment(sketch, "E844", {"start": v(-153.22, -134.17) * mm, "end": v(-151.79, -135.1) * mm});
            skLineSegment(sketch, "E845", {"start": v(-151.79, -135.1) * mm, "end": v(-150.17, -135.73) * mm});
            skLineSegment(sketch, "E846", {"start": v(-150.17, -135.73) * mm, "end": v(-148.38, -136.03) * mm});
            skLineSegment(sketch, "E847", {"start": v(-148.38, -136.03) * mm, "end": v(-146.45, -135.97) * mm});
            skLineSegment(sketch, "E848", {"start": v(-146.45, -135.97) * mm, "end": v(-145.7, -135.87) * mm});
            skLineSegment(sketch, "E849", {"start": v(-145.7, -135.87) * mm, "end": v(-144.87, -135.75) * mm});
            skLineSegment(sketch, "E850", {"start": v(-144.87, -135.75) * mm, "end": v(-144, -135.6) * mm});
            skLineSegment(sketch, "E851", {"start": v(-144, -135.6) * mm, "end": v(-143.12, -135.4) * mm});
            skLineSegment(sketch, "E852", {"start": v(-143.12, -135.4) * mm, "end": v(-142.25, -135.2) * mm});
            skLineSegment(sketch, "E853", {"start": v(-142.25, -135.2) * mm, "end": v(-141.4, -134.96) * mm});
            skLineSegment(sketch, "E854", {"start": v(-141.4, -134.96) * mm, "end": v(-140.62, -134.7) * mm});
            skLineSegment(sketch, "E855", {"start": v(-140.62, -134.7) * mm, "end": v(-139.9, -134.43) * mm});
            skLineSegment(sketch, "E856", {"start": v(-139.9, -134.43) * mm, "end": v(-138.4, -133.77) * mm});
            skLineSegment(sketch, "E857", {"start": v(-138.4, -133.77) * mm, "end": v(-136.88, -133.08) * mm});
            skLineSegment(sketch, "E858", {"start": v(-136.88, -133.08) * mm, "end": v(-135.36, -132.34) * mm});
            skLineSegment(sketch, "E859", {"start": v(-135.36, -132.34) * mm, "end": v(-133.86, -131.54) * mm});
            skLineSegment(sketch, "E860", {"start": v(-133.86, -131.54) * mm, "end": v(-132.41, -130.67) * mm});
            skLineSegment(sketch, "E861", {"start": v(-132.41, -130.67) * mm, "end": v(-131.04, -129.72) * mm});
            skLineSegment(sketch, "E862", {"start": v(-131.04, -129.72) * mm, "end": v(-129.75, -128.66) * mm});
            skLineSegment(sketch, "E863", {"start": v(-129.75, -128.66) * mm, "end": v(-128.58, -127.5) * mm});
            skLineSegment(sketch, "E864", {"start": v(-128.58, -127.5) * mm, "end": v(-128.47, -127.37) * mm});
            skLineSegment(sketch, "E865", {"start": v(-128.47, -127.37) * mm, "end": v(-128.35, -127.24) * mm});
            skLineSegment(sketch, "E866", {"start": v(-128.35, -127.24) * mm, "end": v(-128.24, -127.1) * mm});
            skLineSegment(sketch, "E867", {"start": v(-128.24, -127.1) * mm, "end": v(-128.12, -126.96) * mm});
            skLineSegment(sketch, "E868", {"start": v(-128.12, -126.96) * mm, "end": v(-128, -126.81) * mm});
            skLineSegment(sketch, "E869", {"start": v(-128, -126.81) * mm, "end": v(-127.86, -126.65) * mm});
            skLineSegment(sketch, "E870", {"start": v(-127.86, -126.65) * mm, "end": v(-127.72, -126.49) * mm});
            skLineSegment(sketch, "E871", {"start": v(-127.72, -126.49) * mm, "end": v(-127.57, -126.3) * mm});
            skLineSegment(sketch, "E872", {"start": v(-127.57, -126.3) * mm, "end": v(-127.5, -126.57) * mm});
            skLineSegment(sketch, "E873", {"start": v(-127.5, -126.57) * mm, "end": v(-127.45, -126.8) * mm});
            skLineSegment(sketch, "E874", {"start": v(-127.45, -126.8) * mm, "end": v(-127.4, -127.04) * mm});
            skLineSegment(sketch, "E875", {"start": v(-127.4, -127.04) * mm, "end": v(-127.34, -127.25) * mm});
            skLineSegment(sketch, "E876", {"start": v(-127.34, -127.25) * mm, "end": v(-127.29, -127.45) * mm});
            skLineSegment(sketch, "E877", {"start": v(-127.29, -127.45) * mm, "end": v(-127.24, -127.64) * mm});
            skLineSegment(sketch, "E878", {"start": v(-127.24, -127.64) * mm, "end": v(-127.18, -127.83) * mm});
            skLineSegment(sketch, "E879", {"start": v(-127.18, -127.83) * mm, "end": v(-127.11, -128) * mm});
            skLineSegment(sketch, "E880", {"start": v(-127.11, -128) * mm, "end": v(-126.78, -128.78) * mm});
            skLineSegment(sketch, "E881", {"start": v(-126.78, -128.78) * mm, "end": v(-126.43, -129.44) * mm});
            skLineSegment(sketch, "E882", {"start": v(-126.43, -129.44) * mm, "end": v(-126.08, -130.01) * mm});
            skLineSegment(sketch, "E883", {"start": v(-126.08, -130.01) * mm, "end": v(-125.7, -130.51) * mm});
            skLineSegment(sketch, "E884", {"start": v(-125.7, -130.51) * mm, "end": v(-125.32, -130.96) * mm});
            skLineSegment(sketch, "E885", {"start": v(-125.32, -130.96) * mm, "end": v(-124.93, -131.36) * mm});
            skLineSegment(sketch, "E886", {"start": v(-124.93, -131.36) * mm, "end": v(-124.53, -131.75) * mm});
            skLineSegment(sketch, "E887", {"start": v(-124.53, -131.75) * mm, "end": v(-124.11, -132.14) * mm});
            skLineSegment(sketch, "E888", {"start": v(-124.11, -132.14) * mm, "end": v(-123.5, -132.68) * mm});
            skLineSegment(sketch, "E889", {"start": v(-123.5, -132.68) * mm, "end": v(-122.84, -133.22) * mm});
            skLineSegment(sketch, "E890", {"start": v(-122.84, -133.22) * mm, "end": v(-122.1, -133.72) * mm});
            skLineSegment(sketch, "E891", {"start": v(-122.1, -133.72) * mm, "end": v(-121.28, -134.17) * mm});
            skLineSegment(sketch, "E892", {"start": v(-121.28, -134.17) * mm, "end": v(-120.39, -134.54) * mm});
            skLineSegment(sketch, "E893", {"start": v(-120.39, -134.54) * mm, "end": v(-119.41, -134.82) * mm});
            skLineSegment(sketch, "E894", {"start": v(-119.41, -134.82) * mm, "end": v(-118.35, -134.97) * mm});
            skLineSegment(sketch, "E895", {"start": v(-118.35, -134.97) * mm, "end": v(-117.2, -134.99) * mm});
            skLineSegment(sketch, "E896", {"start": v(-117.2, -134.99) * mm, "end": v(-116.65, -134.95) * mm});
            skLineSegment(sketch, "E897", {"start": v(-116.65, -134.95) * mm, "end": v(-116.1, -134.9) * mm});
            skLineSegment(sketch, "E898", {"start": v(-116.1, -134.9) * mm, "end": v(-115.55, -134.84) * mm});
            skLineSegment(sketch, "E899", {"start": v(-115.55, -134.84) * mm, "end": v(-115, -134.77) * mm});
            skLineSegment(sketch, "E900", {"start": v(-115, -134.77) * mm, "end": v(-114.45, -134.69) * mm});
            skLineSegment(sketch, "E901", {"start": v(-114.45, -134.69) * mm, "end": v(-113.9, -134.59) * mm});
            skLineSegment(sketch, "E902", {"start": v(-113.9, -134.59) * mm, "end": v(-113.36, -134.48) * mm});
            skLineSegment(sketch, "E903", {"start": v(-113.36, -134.48) * mm, "end": v(-112.82, -134.36) * mm});
            skLineSegment(sketch, "E904", {"start": v(-112.82, -134.36) * mm, "end": v(-110.31, -133.68) * mm});
            skLineSegment(sketch, "E905", {"start": v(-110.31, -133.68) * mm, "end": v(-107.87, -132.87) * mm});
            skLineSegment(sketch, "E906", {"start": v(-107.87, -132.87) * mm, "end": v(-105.48, -131.93) * mm});
            skLineSegment(sketch, "E907", {"start": v(-105.48, -131.93) * mm, "end": v(-103.14, -130.88) * mm});
            skLineSegment(sketch, "E908", {"start": v(-103.14, -130.88) * mm, "end": v(-100.86, -129.72) * mm});
            skLineSegment(sketch, "E909", {"start": v(-100.86, -129.72) * mm, "end": v(-98.62, -128.46) * mm});
            skLineSegment(sketch, "E910", {"start": v(-98.62, -128.46) * mm, "end": v(-96.41, -127.12) * mm});
            skLineSegment(sketch, "E911", {"start": v(-96.41, -127.12) * mm, "end": v(-94.25, -125.7) * mm});
            skLineSegment(sketch, "E912", {"start": v(-94.25, -125.7) * mm, "end": v(-94.14, -125.63) * mm});
            skLineSegment(sketch, "E913", {"start": v(-94.14, -125.63) * mm, "end": v(-94.04, -125.57) * mm});
            skLineSegment(sketch, "E914", {"start": v(-94.04, -125.57) * mm, "end": v(-93.94, -125.5) * mm});
            skLineSegment(sketch, "E915", {"start": v(-93.94, -125.5) * mm, "end": v(-93.85, -125.45) * mm});
            skLineSegment(sketch, "E916", {"start": v(-93.85, -125.45) * mm, "end": v(-93.77, -125.4) * mm});
            skLineSegment(sketch, "E917", {"start": v(-93.77, -125.4) * mm, "end": v(-93.7, -125.37) * mm});
            skLineSegment(sketch, "E918", {"start": v(-93.7, -125.37) * mm, "end": v(-93.66, -125.34) * mm});
            skLineSegment(sketch, "E919", {"start": v(-93.66, -125.34) * mm, "end": v(-93.63, -125.33) * mm});
            skLineSegment(sketch, "E920", {"start": v(-93.63, -125.33) * mm, "end": v(-93, -126.24) * mm});
            skLineSegment(sketch, "E921", {"start": v(-93, -126.24) * mm, "end": v(-92.4, -127.15) * mm});
            skLineSegment(sketch, "E922", {"start": v(-92.4, -127.15) * mm, "end": v(-91.8, -128.05) * mm});
            skLineSegment(sketch, "E923", {"start": v(-91.8, -128.05) * mm, "end": v(-91.2, -128.95) * mm});
            skLineSegment(sketch, "E924", {"start": v(-91.2, -128.95) * mm, "end": v(-90.6, -129.83) * mm});
            skLineSegment(sketch, "E925", {"start": v(-90.6, -129.83) * mm, "end": v(-90, -130.7) * mm});
            skLineSegment(sketch, "E926", {"start": v(-90, -130.7) * mm, "end": v(-89.37, -131.55) * mm});
            skLineSegment(sketch, "E927", {"start": v(-89.37, -131.55) * mm, "end": v(-88.72, -132.38) * mm});
            skLineSegment(sketch, "E928", {"start": v(-88.72, -132.38) * mm, "end": v(-87.96, -133.22) * mm});
            skLineSegment(sketch, "E929", {"start": v(-87.96, -133.22) * mm, "end": v(-87.14, -133.94) * mm});
            skLineSegment(sketch, "E930", {"start": v(-87.14, -133.94) * mm, "end": v(-86.25, -134.52) * mm});
            skLineSegment(sketch, "E931", {"start": v(-86.25, -134.52) * mm, "end": v(-85.31, -134.99) * mm});
            skLineSegment(sketch, "E932", {"start": v(-85.31, -134.99) * mm, "end": v(-84.31, -135.32) * mm});
            skLineSegment(sketch, "E933", {"start": v(-84.31, -135.32) * mm, "end": v(-83.25, -135.53) * mm});
            skLineSegment(sketch, "E934", {"start": v(-83.25, -135.53) * mm, "end": v(-82.14, -135.6) * mm});
            skLineSegment(sketch, "E935", {"start": v(-82.14, -135.6) * mm, "end": v(-80.97, -135.55) * mm});
            skLineSegment(sketch, "E936", {"start": v(-80.97, -135.55) * mm, "end": v(-79.6, -135.39) * mm});
            skLineSegment(sketch, "E937", {"start": v(-79.6, -135.39) * mm, "end": v(-78.26, -135.15) * mm});
            skLineSegment(sketch, "E938", {"start": v(-78.26, -135.15) * mm, "end": v(-76.93, -134.86) * mm});
            skLineSegment(sketch, "E939", {"start": v(-76.93, -134.86) * mm, "end": v(-75.61, -134.52) * mm});
            skLineSegment(sketch, "E940", {"start": v(-75.61, -134.52) * mm, "end": v(-74.31, -134.13) * mm});
            skLineSegment(sketch, "E941", {"start": v(-74.31, -134.13) * mm, "end": v(-73.03, -133.7) * mm});
            skLineSegment(sketch, "E942", {"start": v(-73.03, -133.7) * mm, "end": v(-71.75, -133.23) * mm});
            skLineSegment(sketch, "E943", {"start": v(-71.75, -133.23) * mm, "end": v(-70.48, -132.72) * mm});
            skLineSegment(sketch, "E944", {"start": v(-70.48, -132.72) * mm, "end": v(-69.66, -132.38) * mm});
            skLineSegment(sketch, "E945", {"start": v(-69.66, -132.38) * mm, "end": v(-68.85, -132.03) * mm});
            skLineSegment(sketch, "E946", {"start": v(-68.85, -132.03) * mm, "end": v(-68.03, -131.67) * mm});
            skLineSegment(sketch, "E947", {"start": v(-68.03, -131.67) * mm, "end": v(-67.22, -131.3) * mm});
            skLineSegment(sketch, "E948", {"start": v(-67.22, -131.3) * mm, "end": v(-66.41, -130.93) * mm});
            skLineSegment(sketch, "E949", {"start": v(-66.41, -130.93) * mm, "end": v(-65.6, -130.56) * mm});
            skLineSegment(sketch, "E950", {"start": v(-65.6, -130.56) * mm, "end": v(-64.8, -130.19) * mm});
            skLineSegment(sketch, "E951", {"start": v(-64.8, -130.19) * mm, "end": v(-64, -129.82) * mm});
            skLineSegment(sketch, "E952", {"start": v(-64, -129.82) * mm, "end": v(-63.2, -131.1) * mm});
            skLineSegment(sketch, "E953", {"start": v(-63.2, -131.1) * mm, "end": v(-62.38, -132.2) * mm});
            skLineSegment(sketch, "E954", {"start": v(-62.38, -132.2) * mm, "end": v(-61.53, -133.13) * mm});
            skLineSegment(sketch, "E955", {"start": v(-61.53, -133.13) * mm, "end": v(-60.62, -133.89) * mm});
            skLineSegment(sketch, "E956", {"start": v(-60.62, -133.89) * mm, "end": v(-59.65, -134.5) * mm});
            skLineSegment(sketch, "E957", {"start": v(-59.65, -134.5) * mm, "end": v(-58.58, -134.94) * mm});
            skLineSegment(sketch, "E958", {"start": v(-58.58, -134.94) * mm, "end": v(-57.41, -135.24) * mm});
            skLineSegment(sketch, "E959", {"start": v(-57.41, -135.24) * mm, "end": v(-56.12, -135.4) * mm});
            skLineSegment(sketch, "E960", {"start": v(-56.12, -135.4) * mm, "end": v(-55.24, -135.46) * mm});
            skLineSegment(sketch, "E961", {"start": v(-55.24, -135.46) * mm, "end": v(-54.36, -135.5) * mm});
            skLineSegment(sketch, "E962", {"start": v(-54.36, -135.5) * mm, "end": v(-53.47, -135.5) * mm});
            skLineSegment(sketch, "E963", {"start": v(-53.47, -135.5) * mm, "end": v(-52.59, -135.47) * mm});
            skLineSegment(sketch, "E964", {"start": v(-52.59, -135.47) * mm, "end": v(-51.7, -135.42) * mm});
            skLineSegment(sketch, "E965", {"start": v(-51.7, -135.42) * mm, "end": v(-50.83, -135.33) * mm});
            skLineSegment(sketch, "E966", {"start": v(-50.83, -135.33) * mm, "end": v(-49.96, -135.21) * mm});
            skLineSegment(sketch, "E967", {"start": v(-49.96, -135.21) * mm, "end": v(-49.1, -135.06) * mm});
            skLineSegment(sketch, "E968", {"start": v(-49.1, -135.06) * mm, "end": v(-46.87, -134.57) * mm});
            skLineSegment(sketch, "E969", {"start": v(-46.87, -134.57) * mm, "end": v(-44.67, -134.02) * mm});
            skLineSegment(sketch, "E970", {"start": v(-44.67, -134.02) * mm, "end": v(-42.5, -133.4) * mm});
            skLineSegment(sketch, "E971", {"start": v(-42.5, -133.4) * mm, "end": v(-40.38, -132.67) * mm});
            skLineSegment(sketch, "E972", {"start": v(-40.38, -132.67) * mm, "end": v(-38.3, -131.85) * mm});
            skLineSegment(sketch, "E973", {"start": v(-38.3, -131.85) * mm, "end": v(-36.25, -130.93) * mm});
            skLineSegment(sketch, "E974", {"start": v(-36.25, -130.93) * mm, "end": v(-34.26, -129.9) * mm});
            skLineSegment(sketch, "E975", {"start": v(-34.26, -129.9) * mm, "end": v(-32.32, -128.72) * mm});
            skLineSegment(sketch, "E976", {"start": v(-32.32, -128.72) * mm, "end": v(-31.96, -128.5) * mm});
            skLineSegment(sketch, "E977", {"start": v(-31.96, -128.5) * mm, "end": v(-31.61, -128.26) * mm});
            skLineSegment(sketch, "E978", {"start": v(-31.61, -128.26) * mm, "end": v(-31.27, -128.03) * mm});
            skLineSegment(sketch, "E979", {"start": v(-31.27, -128.03) * mm, "end": v(-30.92, -127.8) * mm});
            skLineSegment(sketch, "E980", {"start": v(-30.92, -127.8) * mm, "end": v(-30.57, -127.57) * mm});
            skLineSegment(sketch, "E981", {"start": v(-30.57, -127.57) * mm, "end": v(-30.21, -127.32) * mm});
            skLineSegment(sketch, "E982", {"start": v(-30.21, -127.32) * mm, "end": v(-29.85, -127.08) * mm});
            skLineSegment(sketch, "E983", {"start": v(-29.85, -127.08) * mm, "end": v(-29.47, -126.82) * mm});
            skLineSegment(sketch, "E984", {"start": v(-29.47, -126.82) * mm, "end": v(-28.83, -128.87) * mm});
            skLineSegment(sketch, "E985", {"start": v(-28.83, -128.87) * mm, "end": v(-27.97, -130.54) * mm});
            skLineSegment(sketch, "E986", {"start": v(-27.97, -130.54) * mm, "end": v(-26.88, -131.9) * mm});
            skLineSegment(sketch, "E987", {"start": v(-26.88, -131.9) * mm, "end": v(-25.6, -132.99) * mm});
            skLineSegment(sketch, "E988", {"start": v(-25.6, -132.99) * mm, "end": v(-24.12, -133.84) * mm});
            skLineSegment(sketch, "E989", {"start": v(-24.12, -133.84) * mm, "end": v(-22.47, -134.52) * mm});
            skLineSegment(sketch, "E990", {"start": v(-22.47, -134.52) * mm, "end": v(-20.65, -135.06) * mm});
            skLineSegment(sketch, "E991", {"start": v(-20.65, -135.06) * mm, "end": v(-18.68, -135.52) * mm});
            skLineSegment(sketch, "E992", {"start": v(-18.68, -135.52) * mm, "end": v(-17.2, -135.78) * mm});
            skLineSegment(sketch, "E993", {"start": v(-17.2, -135.78) * mm, "end": v(-15.73, -135.98) * mm});
            skLineSegment(sketch, "E994", {"start": v(-15.73, -135.98) * mm, "end": v(-14.26, -136.1) * mm});
            skLineSegment(sketch, "E995", {"start": v(-14.26, -136.1) * mm, "end": v(-12.78, -136.16) * mm});
            skLineSegment(sketch, "E996", {"start": v(-12.78, -136.16) * mm, "end": v(-11.3, -136.16) * mm});
            skLineSegment(sketch, "E997", {"start": v(-11.3, -136.16) * mm, "end": v(-9.82, -136.1) * mm});
            skLineSegment(sketch, "E998", {"start": v(-9.82, -136.1) * mm, "end": v(-8.34, -136) * mm});
            skLineSegment(sketch, "E999", {"start": v(-8.34, -136) * mm, "end": v(-6.86, -135.86) * mm});
            skLineSegment(sketch, "E1000", {"start": v(-6.86, -135.86) * mm, "end": v(-3.55, -135.42) * mm});
            skLineSegment(sketch, "E1001", {"start": v(-3.55, -135.42) * mm, "end": v(-0.27, -134.82) * mm});
            skLineSegment(sketch, "E1002", {"start": v(-0.27, -134.82) * mm, "end": v(2.96, -134.07) * mm});
            skLineSegment(sketch, "E1003", {"start": v(2.96, -134.07) * mm, "end": v(6.15, -133.2) * mm});
            skLineSegment(sketch, "E1004", {"start": v(6.15, -133.2) * mm, "end": v(9.3, -132.19) * mm});
            skLineSegment(sketch, "E1005", {"start": v(9.3, -132.19) * mm, "end": v(12.42, -131.06) * mm});
            skLineSegment(sketch, "E1006", {"start": v(12.42, -131.06) * mm, "end": v(15.5, -129.81) * mm});
            skLineSegment(sketch, "E1007", {"start": v(15.5, -129.81) * mm, "end": v(18.56, -128.46) * mm});
            skLineSegment(sketch, "E1008", {"start": v(18.56, -128.46) * mm, "end": v(18.96, -128.27) * mm});
            skLineSegment(sketch, "E1009", {"start": v(18.96, -128.27) * mm, "end": v(19.36, -128.08) * mm});
            skLineSegment(sketch, "E1010", {"start": v(19.36, -128.08) * mm, "end": v(19.76, -127.88) * mm});
            skLineSegment(sketch, "E1011", {"start": v(19.76, -127.88) * mm, "end": v(20.16, -127.68) * mm});
            skLineSegment(sketch, "E1012", {"start": v(20.16, -127.68) * mm, "end": v(20.57, -127.48) * mm});
            skLineSegment(sketch, "E1013", {"start": v(20.57, -127.48) * mm, "end": v(20.98, -127.27) * mm});
            skLineSegment(sketch, "E1014", {"start": v(20.98, -127.27) * mm, "end": v(21.4, -127.06) * mm});
            skLineSegment(sketch, "E1015", {"start": v(21.4, -127.06) * mm, "end": v(21.84, -126.84) * mm});
            skLineSegment(sketch, "E1016", {"start": v(21.84, -126.84) * mm, "end": v(21.87, -127.08) * mm});
            skLineSegment(sketch, "E1017", {"start": v(21.87, -127.08) * mm, "end": v(21.89, -127.3) * mm});
            skLineSegment(sketch, "E1018", {"start": v(21.89, -127.3) * mm, "end": v(21.9, -127.5) * mm});
            skLineSegment(sketch, "E1019", {"start": v(21.9, -127.5) * mm, "end": v(21.92, -127.7) * mm});
            skLineSegment(sketch, "E1020", {"start": v(21.92, -127.7) * mm, "end": v(21.94, -127.9) * mm});
            skLineSegment(sketch, "E1021", {"start": v(21.94, -127.9) * mm, "end": v(21.97, -128.08) * mm});
            skLineSegment(sketch, "E1022", {"start": v(21.97, -128.08) * mm, "end": v(22, -128.26) * mm});
            skLineSegment(sketch, "E1023", {"start": v(22, -128.26) * mm, "end": v(22.04, -128.43) * mm});
            skLineSegment(sketch, "E1024", {"start": v(22.04, -128.43) * mm, "end": v(22.17, -128.98) * mm});
            skLineSegment(sketch, "E1025", {"start": v(22.17, -128.98) * mm, "end": v(22.3, -129.53) * mm});
            skLineSegment(sketch, "E1026", {"start": v(22.3, -129.53) * mm, "end": v(22.43, -130.08) * mm});
            skLineSegment(sketch, "E1027", {"start": v(22.43, -130.08) * mm, "end": v(22.56, -130.64) * mm});
            skLineSegment(sketch, "E1028", {"start": v(22.56, -130.64) * mm, "end": v(22.7, -131.18) * mm});
            skLineSegment(sketch, "E1029", {"start": v(22.7, -131.18) * mm, "end": v(22.86, -131.72) * mm});
            skLineSegment(sketch, "E1030", {"start": v(22.86, -131.72) * mm, "end": v(23.05, -132.25) * mm});
            skLineSegment(sketch, "E1031", {"start": v(23.05, -132.25) * mm, "end": v(23.26, -132.76) * mm});
            skLineSegment(sketch, "E1032", {"start": v(23.26, -132.76) * mm, "end": v(23.96, -133.86) * mm});
            skLineSegment(sketch, "E1033", {"start": v(23.96, -133.86) * mm, "end": v(24.88, -134.7) * mm});
            skLineSegment(sketch, "E1034", {"start": v(24.88, -134.7) * mm, "end": v(25.96, -135.26) * mm});
            skLineSegment(sketch, "E1035", {"start": v(25.96, -135.26) * mm, "end": v(27.13, -135.54) * mm});
            skLineSegment(sketch, "E1036", {"start": v(27.13, -135.54) * mm, "end": v(28.34, -135.53) * mm});
            skLineSegment(sketch, "E1037", {"start": v(28.34, -135.53) * mm, "end": v(29.51, -135.23) * mm});
            skLineSegment(sketch, "E1038", {"start": v(29.51, -135.23) * mm, "end": v(30.6, -134.63) * mm});
            skLineSegment(sketch, "E1039", {"start": v(30.6, -134.63) * mm, "end": v(31.55, -133.72) * mm});
            skLineSegment(sketch, "E1040", {"start": v(31.55, -133.72) * mm, "end": v(31.82, -133.35) * mm});
            skLineSegment(sketch, "E1041", {"start": v(31.82, -133.35) * mm, "end": v(32.09, -132.97) * mm});
            skLineSegment(sketch, "E1042", {"start": v(32.09, -132.97) * mm, "end": v(32.34, -132.58) * mm});
            skLineSegment(sketch, "E1043", {"start": v(32.34, -132.58) * mm, "end": v(32.58, -132.19) * mm});
            skLineSegment(sketch, "E1044", {"start": v(32.58, -132.19) * mm, "end": v(32.8, -131.78) * mm});
            skLineSegment(sketch, "E1045", {"start": v(32.8, -131.78) * mm, "end": v(33.01, -131.37) * mm});
            skLineSegment(sketch, "E1046", {"start": v(33.01, -131.37) * mm, "end": v(33.21, -130.95) * mm});
            skLineSegment(sketch, "E1047", {"start": v(33.21, -130.95) * mm, "end": v(33.4, -130.53) * mm});
            skLineSegment(sketch, "E1048", {"start": v(33.4, -130.53) * mm, "end": v(35, -126.97) * mm});
            skLineSegment(sketch, "E1049", {"start": v(35, -126.97) * mm, "end": v(36.69, -123.57) * mm});
            skLineSegment(sketch, "E1050", {"start": v(36.69, -123.57) * mm, "end": v(38.47, -120.3) * mm});
            skLineSegment(sketch, "E1051", {"start": v(38.47, -120.3) * mm, "end": v(40.37, -117.13) * mm});
            skLineSegment(sketch, "E1052", {"start": v(40.37, -117.13) * mm, "end": v(42.37, -114.03) * mm});
            skLineSegment(sketch, "E1053", {"start": v(42.37, -114.03) * mm, "end": v(44.49, -110.96) * mm});
            skLineSegment(sketch, "E1054", {"start": v(44.49, -110.96) * mm, "end": v(46.73, -107.9) * mm});
            skLineSegment(sketch, "E1055", {"start": v(46.73, -107.9) * mm, "end": v(49.1, -104.8) * mm});
            skLineSegment(sketch, "E1056", {"start": v(49.1, -104.8) * mm, "end": v(49.88, -103.8) * mm});
            skLineSegment(sketch, "E1057", {"start": v(49.88, -103.8) * mm, "end": v(50.62, -102.88) * mm});
            skLineSegment(sketch, "E1058", {"start": v(50.62, -102.88) * mm, "end": v(51.34, -102) * mm});
            skLineSegment(sketch, "E1059", {"start": v(51.34, -102) * mm, "end": v(52.05, -101.16) * mm});
            skLineSegment(sketch, "E1060", {"start": v(52.05, -101.16) * mm, "end": v(52.8, -100.32) * mm});
            skLineSegment(sketch, "E1061", {"start": v(52.8, -100.32) * mm, "end": v(53.6, -99.47) * mm});
            skLineSegment(sketch, "E1062", {"start": v(53.6, -99.47) * mm, "end": v(54.48, -98.59) * mm});
            skLineSegment(sketch, "E1063", {"start": v(54.48, -98.59) * mm, "end": v(55.47, -97.64) * mm});
            skLineSegment(sketch, "E1064", {"start": v(55.47, -97.64) * mm, "end": v(55.72, -97.4) * mm});
            skLineSegment(sketch, "E1065", {"start": v(55.72, -97.4) * mm, "end": v(56.05, -97.11) * mm});
            skLineSegment(sketch, "E1066", {"start": v(56.05, -97.11) * mm, "end": v(56.44, -96.77) * mm});
            skLineSegment(sketch, "E1067", {"start": v(56.44, -96.77) * mm, "end": v(56.87, -96.4) * mm});
            skLineSegment(sketch, "E1068", {"start": v(56.87, -96.4) * mm, "end": v(57.31, -96.05) * mm});
            skLineSegment(sketch, "E1069", {"start": v(57.31, -96.05) * mm, "end": v(57.74, -95.73) * mm});
            skLineSegment(sketch, "E1070", {"start": v(57.74, -95.73) * mm, "end": v(58.13, -95.46) * mm});
            skLineSegment(sketch, "E1071", {"start": v(58.13, -95.46) * mm, "end": v(58.47, -95.28) * mm});
            skLineSegment(sketch, "E1072", {"start": v(58.47, -95.28) * mm, "end": v(57.57, -97.03) * mm});
            skLineSegment(sketch, "E1073", {"start": v(57.57, -97.03) * mm, "end": v(56.7, -98.8) * mm});
            skLineSegment(sketch, "E1074", {"start": v(56.7, -98.8) * mm, "end": v(55.88, -100.58) * mm});
            skLineSegment(sketch, "E1075", {"start": v(55.88, -100.58) * mm, "end": v(55.1, -102.38) * mm});
            skLineSegment(sketch, "E1076", {"start": v(55.1, -102.38) * mm, "end": v(54.35, -104.2) * mm});
            skLineSegment(sketch, "E1077", {"start": v(54.35, -104.2) * mm, "end": v(53.64, -106.02) * mm});
            skLineSegment(sketch, "E1078", {"start": v(53.64, -106.02) * mm, "end": v(52.98, -107.87) * mm});
            skLineSegment(sketch, "E1079", {"start": v(52.98, -107.87) * mm, "end": v(52.35, -109.73) * mm});
            skLineSegment(sketch, "E1080", {"start": v(52.35, -109.73) * mm, "end": v(51.7, -112) * mm});
            skLineSegment(sketch, "E1081", {"start": v(51.7, -112) * mm, "end": v(51.25, -114.27) * mm});
            skLineSegment(sketch, "E1082", {"start": v(51.25, -114.27) * mm, "end": v(51, -116.52) * mm});
            skLineSegment(sketch, "E1083", {"start": v(51, -116.52) * mm, "end": v(50.96, -118.75) * mm});
            skLineSegment(sketch, "E1084", {"start": v(50.96, -118.75) * mm, "end": v(51.14, -120.98) * mm});
            skLineSegment(sketch, "E1085", {"start": v(51.14, -120.98) * mm, "end": v(51.56, -123.2) * mm});
            skLineSegment(sketch, "E1086", {"start": v(51.56, -123.2) * mm, "end": v(52.21, -125.4) * mm});
            skLineSegment(sketch, "E1087", {"start": v(52.21, -125.4) * mm, "end": v(53.11, -127.6) * mm});
            skLineSegment(sketch, "E1088", {"start": v(53.11, -127.6) * mm, "end": v(53.84, -129) * mm});
            skLineSegment(sketch, "E1089", {"start": v(53.84, -129) * mm, "end": v(54.64, -130.3) * mm});
            skLineSegment(sketch, "E1090", {"start": v(54.64, -130.3) * mm, "end": v(55.55, -131.5) * mm});
            skLineSegment(sketch, "E1091", {"start": v(55.55, -131.5) * mm, "end": v(56.57, -132.58) * mm});
            skLineSegment(sketch, "E1092", {"start": v(56.57, -132.58) * mm, "end": v(57.7, -133.52) * mm});
            skLineSegment(sketch, "E1093", {"start": v(57.7, -133.52) * mm, "end": v(58.97, -134.31) * mm});
            skLineSegment(sketch, "E1094", {"start": v(58.97, -134.31) * mm, "end": v(60.38, -134.94) * mm});
            skLineSegment(sketch, "E1095", {"start": v(60.38, -134.94) * mm, "end": v(61.94, -135.38) * mm});
            skLineSegment(sketch, "E1096", {"start": v(61.94, -135.38) * mm, "end": v(63.1, -135.56) * mm});
            skLineSegment(sketch, "E1097", {"start": v(63.1, -135.56) * mm, "end": v(64.26, -135.63) * mm});
            skLineSegment(sketch, "E1098", {"start": v(64.26, -135.63) * mm, "end": v(65.4, -135.59) * mm});
            skLineSegment(sketch, "E1099", {"start": v(65.4, -135.59) * mm, "end": v(66.54, -135.46) * mm});
            skLineSegment(sketch, "E1100", {"start": v(66.54, -135.46) * mm, "end": v(67.66, -135.25) * mm});
            skLineSegment(sketch, "E1101", {"start": v(67.66, -135.25) * mm, "end": v(68.78, -134.97) * mm});
            skLineSegment(sketch, "E1102", {"start": v(68.78, -134.97) * mm, "end": v(69.89, -134.63) * mm});
            skLineSegment(sketch, "E1103", {"start": v(69.89, -134.63) * mm, "end": v(71, -134.26) * mm});
            skLineSegment(sketch, "E1104", {"start": v(71, -134.26) * mm, "end": v(73.14, -133.42) * mm});
            skLineSegment(sketch, "E1105", {"start": v(73.14, -133.42) * mm, "end": v(75.23, -132.47) * mm});
            skLineSegment(sketch, "E1106", {"start": v(75.23, -132.47) * mm, "end": v(77.27, -131.43) * mm});
            skLineSegment(sketch, "E1107", {"start": v(77.27, -131.43) * mm, "end": v(79.26, -130.31) * mm});
            skLineSegment(sketch, "E1108", {"start": v(79.26, -130.31) * mm, "end": v(81.21, -129.13) * mm});
            skLineSegment(sketch, "E1109", {"start": v(81.21, -129.13) * mm, "end": v(83.13, -127.88) * mm});
            skLineSegment(sketch, "E1110", {"start": v(83.13, -127.88) * mm, "end": v(85.03, -126.6) * mm});
            skLineSegment(sketch, "E1111", {"start": v(85.03, -126.6) * mm, "end": v(86.91, -125.28) * mm});
            skLineSegment(sketch, "E1112", {"start": v(86.91, -125.28) * mm, "end": v(87.16, -125.1) * mm});
            skLineSegment(sketch, "E1113", {"start": v(87.16, -125.1) * mm, "end": v(87.41, -124.93) * mm});
            skLineSegment(sketch, "E1114", {"start": v(87.41, -124.93) * mm, "end": v(87.66, -124.75) * mm});
            skLineSegment(sketch, "E1115", {"start": v(87.66, -124.75) * mm, "end": v(87.92, -124.57) * mm});
            skLineSegment(sketch, "E1116", {"start": v(87.92, -124.57) * mm, "end": v(88.17, -124.39) * mm});
            skLineSegment(sketch, "E1117", {"start": v(88.17, -124.39) * mm, "end": v(88.43, -124.2) * mm});
            skLineSegment(sketch, "E1118", {"start": v(88.43, -124.2) * mm, "end": v(88.69, -124.02) * mm});
            skLineSegment(sketch, "E1119", {"start": v(88.69, -124.02) * mm, "end": v(88.95, -123.83) * mm});
            skLineSegment(sketch, "E1120", {"start": v(88.95, -123.83) * mm, "end": v(89.06, -124.02) * mm});
            skLineSegment(sketch, "E1121", {"start": v(89.06, -124.02) * mm, "end": v(89.16, -124.2) * mm});
            skLineSegment(sketch, "E1122", {"start": v(89.16, -124.2) * mm, "end": v(89.26, -124.36) * mm});
            skLineSegment(sketch, "E1123", {"start": v(89.26, -124.36) * mm, "end": v(89.36, -124.51) * mm});
            skLineSegment(sketch, "E1124", {"start": v(89.36, -124.51) * mm, "end": v(89.45, -124.66) * mm});
            skLineSegment(sketch, "E1125", {"start": v(89.45, -124.66) * mm, "end": v(89.53, -124.8) * mm});
            skLineSegment(sketch, "E1126", {"start": v(89.53, -124.8) * mm, "end": v(89.62, -124.95) * mm});
            skLineSegment(sketch, "E1127", {"start": v(89.62, -124.95) * mm, "end": v(89.7, -125.1) * mm});
            skLineSegment(sketch, "E1128", {"start": v(89.7, -125.1) * mm, "end": v(91.07, -127.13) * mm});
            skLineSegment(sketch, "E1129", {"start": v(91.07, -127.13) * mm, "end": v(92.57, -128.95) * mm});
            skLineSegment(sketch, "E1130", {"start": v(92.57, -128.95) * mm, "end": v(94.22, -130.57) * mm});
            skLineSegment(sketch, "E1131", {"start": v(94.22, -130.57) * mm, "end": v(96.02, -131.96) * mm});
            skLineSegment(sketch, "E1132", {"start": v(96.02, -131.96) * mm, "end": v(97.97, -133.14) * mm});
            skLineSegment(sketch, "E1133", {"start": v(97.97, -133.14) * mm, "end": v(100.07, -134.1) * mm});
            skLineSegment(sketch, "E1134", {"start": v(100.07, -134.1) * mm, "end": v(102.32, -134.82) * mm});
            skLineSegment(sketch, "E1135", {"start": v(102.32, -134.82) * mm, "end": v(104.73, -135.3) * mm});
            skLineSegment(sketch, "E1136", {"start": v(104.73, -135.3) * mm, "end": v(106.63, -135.53) * mm});
            skLineSegment(sketch, "E1137", {"start": v(106.63, -135.53) * mm, "end": v(108.52, -135.61) * mm});
            skLineSegment(sketch, "E1138", {"start": v(108.52, -135.61) * mm, "end": v(110.4, -135.57) * mm});
            skLineSegment(sketch, "E1139", {"start": v(110.4, -135.57) * mm, "end": v(112.27, -135.41) * mm});
            skLineSegment(sketch, "E1140", {"start": v(112.27, -135.41) * mm, "end": v(114.12, -135.14) * mm});
            skLineSegment(sketch, "E1141", {"start": v(114.12, -135.14) * mm, "end": v(115.96, -134.76) * mm});
            skLineSegment(sketch, "E1142", {"start": v(115.96, -134.76) * mm, "end": v(117.79, -134.29) * mm});
            skLineSegment(sketch, "E1143", {"start": v(117.79, -134.29) * mm, "end": v(119.6, -133.71) * mm});
            skLineSegment(sketch, "E1144", {"start": v(119.6, -133.71) * mm, "end": v(122.57, -132.6) * mm});
            skLineSegment(sketch, "E1145", {"start": v(122.57, -132.6) * mm, "end": v(125.43, -131.31) * mm});
            skLineSegment(sketch, "E1146", {"start": v(125.43, -131.31) * mm, "end": v(128.19, -129.86) * mm});
            skLineSegment(sketch, "E1147", {"start": v(128.19, -129.86) * mm, "end": v(130.86, -128.27) * mm});
            skLineSegment(sketch, "E1148", {"start": v(130.86, -128.27) * mm, "end": v(133.45, -126.54) * mm});
            skLineSegment(sketch, "E1149", {"start": v(133.45, -126.54) * mm, "end": v(135.97, -124.7) * mm});
            skLineSegment(sketch, "E1150", {"start": v(135.97, -124.7) * mm, "end": v(138.42, -122.75) * mm});
            skLineSegment(sketch, "E1151", {"start": v(138.42, -122.75) * mm, "end": v(140.81, -120.7) * mm});
            skLineSegment(sketch, "E1152", {"start": v(140.81, -120.7) * mm, "end": v(140.92, -120.61) * mm});
            skLineSegment(sketch, "E1153", {"start": v(140.92, -120.61) * mm, "end": v(141.02, -120.52) * mm});
            skLineSegment(sketch, "E1154", {"start": v(141.02, -120.52) * mm, "end": v(141.12, -120.43) * mm});
            skLineSegment(sketch, "E1155", {"start": v(141.12, -120.43) * mm, "end": v(141.22, -120.34) * mm});
            skLineSegment(sketch, "E1156", {"start": v(141.22, -120.34) * mm, "end": v(141.32, -120.25) * mm});
            skLineSegment(sketch, "E1157", {"start": v(141.32, -120.25) * mm, "end": v(141.42, -120.16) * mm});
            skLineSegment(sketch, "E1158", {"start": v(141.42, -120.16) * mm, "end": v(141.52, -120.07) * mm});
            skLineSegment(sketch, "E1159", {"start": v(141.52, -120.07) * mm, "end": v(141.62, -119.97) * mm});
            skLineSegment(sketch, "E1160", {"start": v(141.62, -119.97) * mm, "end": v(142.48, -119) * mm});
            skLineSegment(sketch, "E1161", {"start": v(142.48, -119) * mm, "end": v(143.1, -117.9) * mm});
            skLineSegment(sketch, "E1162", {"start": v(143.1, -117.9) * mm, "end": v(143.48, -116.74) * mm});
            skLineSegment(sketch, "E1163", {"start": v(143.48, -116.74) * mm, "end": v(143.62, -115.52) * mm});
            skLineSegment(sketch, "E1164", {"start": v(143.62, -115.52) * mm, "end": v(143.52, -114.3) * mm});
            skLineSegment(sketch, "E1165", {"start": v(143.52, -114.3) * mm, "end": v(143.17, -113.11) * mm});
            skLineSegment(sketch, "E1166", {"start": v(143.17, -113.11) * mm, "end": v(142.58, -112) * mm});
            skLineSegment(sketch, "E1167", {"start": v(142.58, -112) * mm, "end": v(141.75, -111.01) * mm});
            skLineSegment(sketch, "E1168", {"start": v(141.75, -111.01) * mm, "end": v(141.71, -110.98) * mm});
            skLineSegment(sketch, "E1169", {"start": v(141.71, -110.98) * mm, "end": v(141.68, -110.94) * mm});
            skLineSegment(sketch, "E1170", {"start": v(141.68, -110.94) * mm, "end": v(141.64, -110.9) * mm});
            skLineSegment(sketch, "E1171", {"start": v(141.64, -110.9) * mm, "end": v(141.6, -110.87) * mm});
            skLineSegment(sketch, "E1172", {"start": v(141.6, -110.87) * mm, "end": v(141.56, -110.83) * mm});
            skLineSegment(sketch, "E1173", {"start": v(141.56, -110.83) * mm, "end": v(141.53, -110.8) * mm});
            skLineSegment(sketch, "E1174", {"start": v(141.53, -110.8) * mm, "end": v(141.49, -110.76) * mm});
            skLineSegment(sketch, "E1175", {"start": v(141.49, -110.76) * mm, "end": v(141.45, -110.72) * mm});
            skLineSegment(sketch, "E1176", {"start": v(34.96, -89.25) * mm, "end": v(35.08, -88.4) * mm});
            skLineSegment(sketch, "E1177", {"start": v(35.08, -88.4) * mm, "end": v(35.2, -87.67) * mm});
            skLineSegment(sketch, "E1178", {"start": v(35.2, -87.67) * mm, "end": v(35.3, -87.04) * mm});
            skLineSegment(sketch, "E1179", {"start": v(35.3, -87.04) * mm, "end": v(35.41, -86.45) * mm});
            skLineSegment(sketch, "E1180", {"start": v(35.41, -86.45) * mm, "end": v(35.52, -85.87) * mm});
            skLineSegment(sketch, "E1181", {"start": v(35.52, -85.87) * mm, "end": v(35.64, -85.24) * mm});
            skLineSegment(sketch, "E1182", {"start": v(35.64, -85.24) * mm, "end": v(35.76, -84.52) * mm});
            skLineSegment(sketch, "E1183", {"start": v(35.76, -84.52) * mm, "end": v(35.9, -83.66) * mm});
            skLineSegment(sketch, "E1184", {"start": v(35.9, -83.66) * mm, "end": v(36.32, -80.95) * mm});
            skLineSegment(sketch, "E1185", {"start": v(36.32, -80.95) * mm, "end": v(36.76, -78.25) * mm});
            skLineSegment(sketch, "E1186", {"start": v(36.76, -78.25) * mm, "end": v(37.23, -75.56) * mm});
            skLineSegment(sketch, "E1187", {"start": v(37.23, -75.56) * mm, "end": v(37.7, -72.86) * mm});
            skLineSegment(sketch, "E1188", {"start": v(37.7, -72.86) * mm, "end": v(38.17, -70.17) * mm});
            skLineSegment(sketch, "E1189", {"start": v(38.17, -70.17) * mm, "end": v(38.64, -67.47) * mm});
            skLineSegment(sketch, "E1190", {"start": v(38.64, -67.47) * mm, "end": v(39.1, -64.77) * mm});
            skLineSegment(sketch, "E1191", {"start": v(39.1, -64.77) * mm, "end": v(39.55, -62.07) * mm});
            skLineSegment(sketch, "E1192", {"start": v(39.55, -62.07) * mm, "end": v(40.27, -58.2) * mm});
            skLineSegment(sketch, "E1193", {"start": v(40.27, -58.2) * mm, "end": v(41.16, -54.49) * mm});
            skLineSegment(sketch, "E1194", {"start": v(41.16, -54.49) * mm, "end": v(42.24, -50.92) * mm});
            skLineSegment(sketch, "E1195", {"start": v(42.24, -50.92) * mm, "end": v(43.5, -47.46) * mm});
            skLineSegment(sketch, "E1196", {"start": v(43.5, -47.46) * mm, "end": v(44.94, -44.07) * mm});
            skLineSegment(sketch, "E1197", {"start": v(44.94, -44.07) * mm, "end": v(46.58, -40.73) * mm});
            skLineSegment(sketch, "E1198", {"start": v(46.58, -40.73) * mm, "end": v(48.41, -37.4) * mm});
            skLineSegment(sketch, "E1199", {"start": v(48.41, -37.4) * mm, "end": v(50.45, -34.06) * mm});
            skLineSegment(sketch, "E1200", {"start": v(50.45, -34.06) * mm, "end": v(50.66, -33.74) * mm});
            skLineSegment(sketch, "E1201", {"start": v(50.66, -33.74) * mm, "end": v(50.9, -33.4) * mm});
            skLineSegment(sketch, "E1202", {"start": v(50.9, -33.4) * mm, "end": v(51.15, -33.07) * mm});
            skLineSegment(sketch, "E1203", {"start": v(51.15, -33.07) * mm, "end": v(51.42, -32.73) * mm});
            skLineSegment(sketch, "E1204", {"start": v(51.42, -32.73) * mm, "end": v(51.7, -32.4) * mm});
            skLineSegment(sketch, "E1205", {"start": v(51.7, -32.4) * mm, "end": v(51.98, -32.09) * mm});
            skLineSegment(sketch, "E1206", {"start": v(51.98, -32.09) * mm, "end": v(52.26, -31.8) * mm});
            skLineSegment(sketch, "E1207", {"start": v(52.26, -31.8) * mm, "end": v(52.54, -31.52) * mm});
            skLineSegment(sketch, "E1208", {"start": v(52.54, -31.52) * mm, "end": v(52.97, -31.2) * mm});
            skLineSegment(sketch, "E1209", {"start": v(52.97, -31.2) * mm, "end": v(53.45, -31.01) * mm});
            skLineSegment(sketch, "E1210", {"start": v(53.45, -31.01) * mm, "end": v(53.94, -30.94) * mm});
            skLineSegment(sketch, "E1211", {"start": v(53.94, -30.94) * mm, "end": v(54.42, -31) * mm});
            skLineSegment(sketch, "E1212", {"start": v(54.42, -31) * mm, "end": v(54.87, -31.16) * mm});
            skLineSegment(sketch, "E1213", {"start": v(54.87, -31.16) * mm, "end": v(55.26, -31.43) * mm});
            skLineSegment(sketch, "E1214", {"start": v(55.26, -31.43) * mm, "end": v(55.56, -31.82) * mm});
            skLineSegment(sketch, "E1215", {"start": v(55.56, -31.82) * mm, "end": v(55.75, -32.3) * mm});
            skLineSegment(sketch, "E1216", {"start": v(55.75, -32.3) * mm, "end": v(55.91, -33.24) * mm});
            skLineSegment(sketch, "E1217", {"start": v(55.91, -33.24) * mm, "end": v(55.98, -34.1) * mm});
            skLineSegment(sketch, "E1218", {"start": v(55.98, -34.1) * mm, "end": v(55.98, -34.91) * mm});
            skLineSegment(sketch, "E1219", {"start": v(55.98, -34.91) * mm, "end": v(55.9, -35.7) * mm});
            skLineSegment(sketch, "E1220", {"start": v(55.9, -35.7) * mm, "end": v(55.78, -36.5) * mm});
            skLineSegment(sketch, "E1221", {"start": v(55.78, -36.5) * mm, "end": v(55.62, -37.31) * mm});
            skLineSegment(sketch, "E1222", {"start": v(55.62, -37.31) * mm, "end": v(55.44, -38.17) * mm});
            skLineSegment(sketch, "E1223", {"start": v(55.44, -38.17) * mm, "end": v(55.26, -39.09) * mm});
            skLineSegment(sketch, "E1224", {"start": v(55.26, -39.09) * mm, "end": v(54.56, -42.37) * mm});
            skLineSegment(sketch, "E1225", {"start": v(54.56, -42.37) * mm, "end": v(53.75, -45.6) * mm});
            skLineSegment(sketch, "E1226", {"start": v(53.75, -45.6) * mm, "end": v(52.82, -48.8) * mm});
            skLineSegment(sketch, "E1227", {"start": v(52.82, -48.8) * mm, "end": v(51.8, -51.98) * mm});
            skLineSegment(sketch, "E1228", {"start": v(51.8, -51.98) * mm, "end": v(50.7, -55.13) * mm});
            skLineSegment(sketch, "E1229", {"start": v(50.7, -55.13) * mm, "end": v(49.53, -58.25) * mm});
            skLineSegment(sketch, "E1230", {"start": v(49.53, -58.25) * mm, "end": v(48.3, -61.35) * mm});
            skLineSegment(sketch, "E1231", {"start": v(48.3, -61.35) * mm, "end": v(47, -64.43) * mm});
            skLineSegment(sketch, "E1232", {"start": v(47, -64.43) * mm, "end": v(45.7, -67.55) * mm});
            skLineSegment(sketch, "E1233", {"start": v(45.7, -67.55) * mm, "end": v(44.55, -70.44) * mm});
            skLineSegment(sketch, "E1234", {"start": v(44.55, -70.44) * mm, "end": v(43.48, -73.19) * mm});
            skLineSegment(sketch, "E1235", {"start": v(43.48, -73.19) * mm, "end": v(42.45, -75.85) * mm});
            skLineSegment(sketch, "E1236", {"start": v(42.45, -75.85) * mm, "end": v(41.42, -78.52) * mm});
            skLineSegment(sketch, "E1237", {"start": v(41.42, -78.52) * mm, "end": v(40.35, -81.27) * mm});
            skLineSegment(sketch, "E1238", {"start": v(40.35, -81.27) * mm, "end": v(39.18, -84.15) * mm});
            skLineSegment(sketch, "E1239", {"start": v(39.18, -84.15) * mm, "end": v(37.87, -87.26) * mm});
            skLineSegment(sketch, "E1240", {"start": v(37.87, -87.26) * mm, "end": v(37.78, -87.44) * mm});
            skLineSegment(sketch, "E1241", {"start": v(37.78, -87.44) * mm, "end": v(37.62, -87.72) * mm});
            skLineSegment(sketch, "E1242", {"start": v(37.62, -87.72) * mm, "end": v(37.43, -88.06) * mm});
            skLineSegment(sketch, "E1243", {"start": v(37.43, -88.06) * mm, "end": v(37.22, -88.43) * mm});
            skLineSegment(sketch, "E1244", {"start": v(37.22, -88.43) * mm, "end": v(37, -88.8) * mm});
            skLineSegment(sketch, "E1245", {"start": v(37, -88.8) * mm, "end": v(36.8, -89.15) * mm});
            skLineSegment(sketch, "E1246", {"start": v(36.8, -89.15) * mm, "end": v(36.65, -89.42) * mm});
            skLineSegment(sketch, "E1247", {"start": v(36.65, -89.42) * mm, "end": v(36.55, -89.6) * mm});
            skLineSegment(sketch, "E1248", {"start": v(36.55, -89.6) * mm, "end": v(36.47, -89.58) * mm});
            skLineSegment(sketch, "E1249", {"start": v(36.47, -89.58) * mm, "end": v(36.29, -89.54) * mm});
            skLineSegment(sketch, "E1250", {"start": v(36.29, -89.54) * mm, "end": v(36.04, -89.49) * mm});
            skLineSegment(sketch, "E1251", {"start": v(36.04, -89.49) * mm, "end": v(35.76, -89.43) * mm});
            skLineSegment(sketch, "E1252", {"start": v(35.76, -89.43) * mm, "end": v(35.48, -89.37) * mm});
            skLineSegment(sketch, "E1253", {"start": v(35.48, -89.37) * mm, "end": v(35.23, -89.31) * mm});
            skLineSegment(sketch, "E1254", {"start": v(35.23, -89.31) * mm, "end": v(35.04, -89.27) * mm});
            skLineSegment(sketch, "E1255", {"start": v(35.04, -89.27) * mm, "end": v(34.96, -89.25) * mm});
            skLineSegment(sketch, "E1256", {"start": v(-82.29, -86.45) * mm, "end": v(-82.12, -85.2) * mm});
            skLineSegment(sketch, "E1257", {"start": v(-82.12, -85.2) * mm, "end": v(-81.96, -83.97) * mm});
            skLineSegment(sketch, "E1258", {"start": v(-81.96, -83.97) * mm, "end": v(-81.8, -82.72) * mm});
            skLineSegment(sketch, "E1259", {"start": v(-81.8, -82.72) * mm, "end": v(-81.62, -81.48) * mm});
            skLineSegment(sketch, "E1260", {"start": v(-81.62, -81.48) * mm, "end": v(-81.46, -80.24) * mm});
            skLineSegment(sketch, "E1261", {"start": v(-81.46, -80.24) * mm, "end": v(-81.28, -79) * mm});
            skLineSegment(sketch, "E1262", {"start": v(-81.28, -79) * mm, "end": v(-81.1, -77.75) * mm});
            skLineSegment(sketch, "E1263", {"start": v(-81.1, -77.75) * mm, "end": v(-80.92, -76.52) * mm});
            skLineSegment(sketch, "E1264", {"start": v(-80.92, -76.52) * mm, "end": v(-80.25, -72.55) * mm});
            skLineSegment(sketch, "E1265", {"start": v(-80.25, -72.55) * mm, "end": v(-79.46, -68.62) * mm});
            skLineSegment(sketch, "E1266", {"start": v(-79.46, -68.62) * mm, "end": v(-78.56, -64.71) * mm});
            skLineSegment(sketch, "E1267", {"start": v(-78.56, -64.71) * mm, "end": v(-77.56, -60.84) * mm});
            skLineSegment(sketch, "E1268", {"start": v(-77.56, -60.84) * mm, "end": v(-76.44, -57) * mm});
            skLineSegment(sketch, "E1269", {"start": v(-76.44, -57) * mm, "end": v(-75.23, -53.18) * mm});
            skLineSegment(sketch, "E1270", {"start": v(-75.23, -53.18) * mm, "end": v(-73.92, -49.4) * mm});
            skLineSegment(sketch, "E1271", {"start": v(-73.92, -49.4) * mm, "end": v(-72.5, -45.63) * mm});
            skLineSegment(sketch, "E1272", {"start": v(-72.5, -45.63) * mm, "end": v(-72.04, -44.51) * mm});
            skLineSegment(sketch, "E1273", {"start": v(-72.04, -44.51) * mm, "end": v(-71.53, -43.4) * mm});
            skLineSegment(sketch, "E1274", {"start": v(-71.53, -43.4) * mm, "end": v(-70.97, -42.32) * mm});
            skLineSegment(sketch, "E1275", {"start": v(-70.97, -42.32) * mm, "end": v(-70.38, -41.25) * mm});
            skLineSegment(sketch, "E1276", {"start": v(-70.38, -41.25) * mm, "end": v(-69.77, -40.18) * mm});
            skLineSegment(sketch, "E1277", {"start": v(-69.77, -40.18) * mm, "end": v(-69.14, -39.13) * mm});
            skLineSegment(sketch, "E1278", {"start": v(-69.14, -39.13) * mm, "end": v(-68.5, -38.08) * mm});
            skLineSegment(sketch, "E1279", {"start": v(-68.5, -38.08) * mm, "end": v(-67.86, -37.03) * mm});
            skLineSegment(sketch, "E1280", {"start": v(-67.86, -37.03) * mm, "end": v(-67.6, -36.65) * mm});
            skLineSegment(sketch, "E1281", {"start": v(-67.6, -36.65) * mm, "end": v(-67.3, -36.29) * mm});
            skLineSegment(sketch, "E1282", {"start": v(-67.3, -36.29) * mm, "end": v(-66.98, -35.94) * mm});
            skLineSegment(sketch, "E1283", {"start": v(-66.98, -35.94) * mm, "end": v(-66.63, -35.61) * mm});
            skLineSegment(sketch, "E1284", {"start": v(-66.63, -35.61) * mm, "end": v(-66.26, -35.3) * mm});
            skLineSegment(sketch, "E1285", {"start": v(-66.26, -35.3) * mm, "end": v(-65.88, -35) * mm});
            skLineSegment(sketch, "E1286", {"start": v(-65.88, -35) * mm, "end": v(-65.49, -34.72) * mm});
            skLineSegment(sketch, "E1287", {"start": v(-65.49, -34.72) * mm, "end": v(-65.1, -34.46) * mm});
            skLineSegment(sketch, "E1288", {"start": v(-65.1, -34.46) * mm, "end": v(-64.7, -34.22) * mm});
            skLineSegment(sketch, "E1289", {"start": v(-64.7, -34.22) * mm, "end": v(-64.36, -34.09) * mm});
            skLineSegment(sketch, "E1290", {"start": v(-64.36, -34.09) * mm, "end": v(-64.07, -34.06) * mm});
            skLineSegment(sketch, "E1291", {"start": v(-64.07, -34.06) * mm, "end": v(-63.84, -34.12) * mm});
            skLineSegment(sketch, "E1292", {"start": v(-63.84, -34.12) * mm, "end": v(-63.66, -34.3) * mm});
            skLineSegment(sketch, "E1293", {"start": v(-63.66, -34.3) * mm, "end": v(-63.52, -34.56) * mm});
            skLineSegment(sketch, "E1294", {"start": v(-63.52, -34.56) * mm, "end": v(-63.41, -34.92) * mm});
            skLineSegment(sketch, "E1295", {"start": v(-63.41, -34.92) * mm, "end": v(-63.34, -35.39) * mm});
            skLineSegment(sketch, "E1296", {"start": v(-63.34, -35.39) * mm, "end": v(-63.24, -36.84) * mm});
            skLineSegment(sketch, "E1297", {"start": v(-63.24, -36.84) * mm, "end": v(-63.25, -38.28) * mm});
            skLineSegment(sketch, "E1298", {"start": v(-63.25, -38.28) * mm, "end": v(-63.36, -39.7) * mm});
            skLineSegment(sketch, "E1299", {"start": v(-63.36, -39.7) * mm, "end": v(-63.54, -41.13) * mm});
            skLineSegment(sketch, "E1300", {"start": v(-63.54, -41.13) * mm, "end": v(-63.8, -42.54) * mm});
            skLineSegment(sketch, "E1301", {"start": v(-63.8, -42.54) * mm, "end": v(-64.1, -43.94) * mm});
            skLineSegment(sketch, "E1302", {"start": v(-64.1, -43.94) * mm, "end": v(-64.43, -45.33) * mm});
            skLineSegment(sketch, "E1303", {"start": v(-64.43, -45.33) * mm, "end": v(-64.78, -46.72) * mm});
            skLineSegment(sketch, "E1304", {"start": v(-64.78, -46.72) * mm, "end": v(-65.77, -50.26) * mm});
            skLineSegment(sketch, "E1305", {"start": v(-65.77, -50.26) * mm, "end": v(-66.88, -53.76) * mm});
            skLineSegment(sketch, "E1306", {"start": v(-66.88, -53.76) * mm, "end": v(-68.1, -57.2) * mm});
            skLineSegment(sketch, "E1307", {"start": v(-68.1, -57.2) * mm, "end": v(-69.4, -60.62) * mm});
            skLineSegment(sketch, "E1308", {"start": v(-69.4, -60.62) * mm, "end": v(-70.8, -64) * mm});
            skLineSegment(sketch, "E1309", {"start": v(-70.8, -64) * mm, "end": v(-72.27, -67.36) * mm});
            skLineSegment(sketch, "E1310", {"start": v(-72.27, -67.36) * mm, "end": v(-73.81, -70.69) * mm});
            skLineSegment(sketch, "E1311", {"start": v(-73.81, -70.69) * mm, "end": v(-75.4, -74) * mm});
            skLineSegment(sketch, "E1312", {"start": v(-75.4, -74) * mm, "end": v(-76.18, -75.57) * mm});
            skLineSegment(sketch, "E1313", {"start": v(-76.18, -75.57) * mm, "end": v(-76.98, -77.15) * mm});
            skLineSegment(sketch, "E1314", {"start": v(-76.98, -77.15) * mm, "end": v(-77.78, -78.72) * mm});
            skLineSegment(sketch, "E1315", {"start": v(-77.78, -78.72) * mm, "end": v(-78.58, -80.29) * mm});
            skLineSegment(sketch, "E1316", {"start": v(-78.58, -80.29) * mm, "end": v(-79.4, -81.85) * mm});
            skLineSegment(sketch, "E1317", {"start": v(-79.4, -81.85) * mm, "end": v(-80.2, -83.42) * mm});
            skLineSegment(sketch, "E1318", {"start": v(-80.2, -83.42) * mm, "end": v(-81.02, -84.98) * mm});
            skLineSegment(sketch, "E1319", {"start": v(-81.02, -84.98) * mm, "end": v(-81.82, -86.55) * mm});
            skLineSegment(sketch, "E1320", {"start": v(-81.82, -86.55) * mm, "end": v(-81.88, -86.54) * mm});
            skLineSegment(sketch, "E1321", {"start": v(-81.88, -86.54) * mm, "end": v(-81.94, -86.52) * mm});
            skLineSegment(sketch, "E1322", {"start": v(-81.94, -86.52) * mm, "end": v(-82, -86.51) * mm});
            skLineSegment(sketch, "E1323", {"start": v(-82, -86.51) * mm, "end": v(-82.06, -86.5) * mm});
            skLineSegment(sketch, "E1324", {"start": v(-82.06, -86.5) * mm, "end": v(-82.11, -86.49) * mm});
            skLineSegment(sketch, "E1325", {"start": v(-82.11, -86.49) * mm, "end": v(-82.17, -86.47) * mm});
            skLineSegment(sketch, "E1326", {"start": v(-82.17, -86.47) * mm, "end": v(-82.23, -86.46) * mm});
            skLineSegment(sketch, "E1327", {"start": v(-82.23, -86.46) * mm, "end": v(-82.29, -86.45) * mm});
            skLineSegment(sketch, "E1328", {"start": v(-22.85, -118.96) * mm, "end": v(-21.1, -117.13) * mm});
            skLineSegment(sketch, "E1329", {"start": v(-21.1, -117.13) * mm, "end": v(-19.36, -115.29) * mm});
            skLineSegment(sketch, "E1330", {"start": v(-19.36, -115.29) * mm, "end": v(-17.6, -113.44) * mm});
            skLineSegment(sketch, "E1331", {"start": v(-17.6, -113.44) * mm, "end": v(-15.84, -111.6) * mm});
            skLineSegment(sketch, "E1332", {"start": v(-15.84, -111.6) * mm, "end": v(-14.06, -109.73) * mm});
            skLineSegment(sketch, "E1333", {"start": v(-14.06, -109.73) * mm, "end": v(-12.27, -107.85) * mm});
            skLineSegment(sketch, "E1334", {"start": v(-12.27, -107.85) * mm, "end": v(-10.47, -105.96) * mm});
            skLineSegment(sketch, "E1335", {"start": v(-10.47, -105.96) * mm, "end": v(-8.65, -104.05) * mm});
            skLineSegment(sketch, "E1336", {"start": v(-8.65, -104.05) * mm, "end": v(-8.42, -103.86) * mm});
            skLineSegment(sketch, "E1337", {"start": v(-8.42, -103.86) * mm, "end": v(-8.16, -103.76) * mm});
            skLineSegment(sketch, "E1338", {"start": v(-8.16, -103.76) * mm, "end": v(-7.9, -103.72) * mm});
            skLineSegment(sketch, "E1339", {"start": v(-7.9, -103.72) * mm, "end": v(-7.63, -103.76) * mm});
            skLineSegment(sketch, "E1340", {"start": v(-7.63, -103.76) * mm, "end": v(-7.38, -103.87) * mm});
            skLineSegment(sketch, "E1341", {"start": v(-7.38, -103.87) * mm, "end": v(-7.16, -104.03) * mm});
            skLineSegment(sketch, "E1342", {"start": v(-7.16, -104.03) * mm, "end": v(-7, -104.25) * mm});
            skLineSegment(sketch, "E1343", {"start": v(-7, -104.25) * mm, "end": v(-6.9, -104.53) * mm});
            skLineSegment(sketch, "E1344", {"start": v(-6.9, -104.53) * mm, "end": v(-6.83, -104.85) * mm});
            skLineSegment(sketch, "E1345", {"start": v(-6.83, -104.85) * mm, "end": v(-6.76, -105.17) * mm});
            skLineSegment(sketch, "E1346", {"start": v(-6.76, -105.17) * mm, "end": v(-6.7, -105.48) * mm});
            skLineSegment(sketch, "E1347", {"start": v(-6.7, -105.48) * mm, "end": v(-6.65, -105.8) * mm});
            skLineSegment(sketch, "E1348", {"start": v(-6.65, -105.8) * mm, "end": v(-6.6, -106.1) * mm});
            skLineSegment(sketch, "E1349", {"start": v(-6.6, -106.1) * mm, "end": v(-6.57, -106.4) * mm});
            skLineSegment(sketch, "E1350", {"start": v(-6.57, -106.4) * mm, "end": v(-6.54, -106.71) * mm});
            skLineSegment(sketch, "E1351", {"start": v(-6.54, -106.71) * mm, "end": v(-6.53, -107.02) * mm});
            skLineSegment(sketch, "E1352", {"start": v(-6.53, -107.02) * mm, "end": v(-6.5, -108.31) * mm});
            skLineSegment(sketch, "E1353", {"start": v(-6.5, -108.31) * mm, "end": v(-6.47, -109.61) * mm});
            skLineSegment(sketch, "E1354", {"start": v(-6.47, -109.61) * mm, "end": v(-6.46, -110.91) * mm});
            skLineSegment(sketch, "E1355", {"start": v(-6.46, -110.91) * mm, "end": v(-6.46, -112.21) * mm});
            skLineSegment(sketch, "E1356", {"start": v(-6.46, -112.21) * mm, "end": v(-6.46, -113.51) * mm});
            skLineSegment(sketch, "E1357", {"start": v(-6.46, -113.51) * mm, "end": v(-6.47, -114.81) * mm});
            skLineSegment(sketch, "E1358", {"start": v(-6.47, -114.81) * mm, "end": v(-6.5, -116.11) * mm});
            skLineSegment(sketch, "E1359", {"start": v(-6.5, -116.11) * mm, "end": v(-6.51, -117.41) * mm});
            skLineSegment(sketch, "E1360", {"start": v(-6.51, -117.41) * mm, "end": v(-6.53, -117.86) * mm});
            skLineSegment(sketch, "E1361", {"start": v(-6.53, -117.86) * mm, "end": v(-6.56, -118.3) * mm});
            skLineSegment(sketch, "E1362", {"start": v(-6.56, -118.3) * mm, "end": v(-6.6, -118.75) * mm});
            skLineSegment(sketch, "E1363", {"start": v(-6.6, -118.75) * mm, "end": v(-6.65, -119.2) * mm});
            skLineSegment(sketch, "E1364", {"start": v(-6.65, -119.2) * mm, "end": v(-6.72, -119.64) * mm});
            skLineSegment(sketch, "E1365", {"start": v(-6.72, -119.64) * mm, "end": v(-6.8, -120.08) * mm});
            skLineSegment(sketch, "E1366", {"start": v(-6.8, -120.08) * mm, "end": v(-6.9, -120.52) * mm});
            skLineSegment(sketch, "E1367", {"start": v(-6.9, -120.52) * mm, "end": v(-7.01, -120.95) * mm});
            skLineSegment(sketch, "E1368", {"start": v(-7.01, -120.95) * mm, "end": v(-7.66, -122.57) * mm});
            skLineSegment(sketch, "E1369", {"start": v(-7.66, -122.57) * mm, "end": v(-8.63, -123.94) * mm});
            skLineSegment(sketch, "E1370", {"start": v(-8.63, -123.94) * mm, "end": v(-9.85, -125.03) * mm});
            skLineSegment(sketch, "E1371", {"start": v(-9.85, -125.03) * mm, "end": v(-11.27, -125.82) * mm});
            skLineSegment(sketch, "E1372", {"start": v(-11.27, -125.82) * mm, "end": v(-12.82, -126.29) * mm});
            skLineSegment(sketch, "E1373", {"start": v(-12.82, -126.29) * mm, "end": v(-14.46, -126.4) * mm});
            skLineSegment(sketch, "E1374", {"start": v(-14.46, -126.4) * mm, "end": v(-16.1, -126.12) * mm});
            skLineSegment(sketch, "E1375", {"start": v(-16.1, -126.12) * mm, "end": v(-17.72, -125.44) * mm});
            skLineSegment(sketch, "E1376", {"start": v(-17.72, -125.44) * mm, "end": v(-18.2, -125.15) * mm});
            skLineSegment(sketch, "E1377", {"start": v(-18.2, -125.15) * mm, "end": v(-18.67, -124.83) * mm});
            skLineSegment(sketch, "E1378", {"start": v(-18.67, -124.83) * mm, "end": v(-19.12, -124.5) * mm});
            skLineSegment(sketch, "E1379", {"start": v(-19.12, -124.5) * mm, "end": v(-19.57, -124.14) * mm});
            skLineSegment(sketch, "E1380", {"start": v(-19.57, -124.14) * mm, "end": v(-20, -123.78) * mm});
            skLineSegment(sketch, "E1381", {"start": v(-20, -123.78) * mm, "end": v(-20.44, -123.4) * mm});
            skLineSegment(sketch, "E1382", {"start": v(-20.44, -123.4) * mm, "end": v(-20.87, -123.03) * mm});
            skLineSegment(sketch, "E1383", {"start": v(-20.87, -123.03) * mm, "end": v(-21.3, -122.66) * mm});
            skLineSegment(sketch, "E1384", {"start": v(-21.3, -122.66) * mm, "end": v(-21.5, -122.5) * mm});
            skLineSegment(sketch, "E1385", {"start": v(-21.5, -122.5) * mm, "end": v(-21.68, -122.33) * mm});
            skLineSegment(sketch, "E1386", {"start": v(-21.68, -122.33) * mm, "end": v(-21.87, -122.16) * mm});
            skLineSegment(sketch, "E1387", {"start": v(-21.87, -122.16) * mm, "end": v(-22.06, -122) * mm});
            skLineSegment(sketch, "E1388", {"start": v(-22.06, -122) * mm, "end": v(-22.24, -121.82) * mm});
            skLineSegment(sketch, "E1389", {"start": v(-22.24, -121.82) * mm, "end": v(-22.43, -121.64) * mm});
            skLineSegment(sketch, "E1390", {"start": v(-22.43, -121.64) * mm, "end": v(-22.62, -121.46) * mm});
            skLineSegment(sketch, "E1391", {"start": v(-22.62, -121.46) * mm, "end": v(-22.8, -121.28) * mm});
            skLineSegment(sketch, "E1392", {"start": v(-22.8, -121.28) * mm, "end": v(-23.02, -121.03) * mm});
            skLineSegment(sketch, "E1393", {"start": v(-23.02, -121.03) * mm, "end": v(-23.17, -120.75) * mm});
            skLineSegment(sketch, "E1394", {"start": v(-23.17, -120.75) * mm, "end": v(-23.27, -120.44) * mm});
            skLineSegment(sketch, "E1395", {"start": v(-23.27, -120.44) * mm, "end": v(-23.3, -120.13) * mm});
            skLineSegment(sketch, "E1396", {"start": v(-23.3, -120.13) * mm, "end": v(-23.28, -119.82) * mm});
            skLineSegment(sketch, "E1397", {"start": v(-23.28, -119.82) * mm, "end": v(-23.2, -119.51) * mm});
            skLineSegment(sketch, "E1398", {"start": v(-23.2, -119.51) * mm, "end": v(-23.06, -119.22) * mm});
            skLineSegment(sketch, "E1399", {"start": v(-23.06, -119.22) * mm, "end": v(-22.85, -118.96) * mm});
            skLineSegment(sketch, "E1400", {"start": v(100.46, -106.4) * mm, "end": v(100.5, -105.8) * mm});
            skLineSegment(sketch, "E1401", {"start": v(100.5, -105.8) * mm, "end": v(100.54, -105.24) * mm});
            skLineSegment(sketch, "E1402", {"start": v(100.54, -105.24) * mm, "end": v(100.56, -104.67) * mm});
            skLineSegment(sketch, "E1403", {"start": v(100.56, -104.67) * mm, "end": v(100.6, -104.11) * mm});
            skLineSegment(sketch, "E1404", {"start": v(100.6, -104.11) * mm, "end": v(100.64, -103.57) * mm});
            skLineSegment(sketch, "E1405", {"start": v(100.64, -103.57) * mm, "end": v(100.7, -103.03) * mm});
            skLineSegment(sketch, "E1406", {"start": v(100.7, -103.03) * mm, "end": v(100.79, -102.5) * mm});
            skLineSegment(sketch, "E1407", {"start": v(100.79, -102.5) * mm, "end": v(100.92, -102) * mm});
            skLineSegment(sketch, "E1408", {"start": v(100.92, -102) * mm, "end": v(101.27, -100.82) * mm});
            skLineSegment(sketch, "E1409", {"start": v(101.27, -100.82) * mm, "end": v(101.63, -99.65) * mm});
            skLineSegment(sketch, "E1410", {"start": v(101.63, -99.65) * mm, "end": v(102, -98.48) * mm});
            skLineSegment(sketch, "E1411", {"start": v(102, -98.48) * mm, "end": v(102.39, -97.32) * mm});
            skLineSegment(sketch, "E1412", {"start": v(102.39, -97.32) * mm, "end": v(102.79, -96.16) * mm});
            skLineSegment(sketch, "E1413", {"start": v(102.79, -96.16) * mm, "end": v(103.21, -95.01) * mm});
            skLineSegment(sketch, "E1414", {"start": v(103.21, -95.01) * mm, "end": v(103.67, -93.87) * mm});
            skLineSegment(sketch, "E1415", {"start": v(103.67, -93.87) * mm, "end": v(104.15, -92.75) * mm});
            skLineSegment(sketch, "E1416", {"start": v(104.15, -92.75) * mm, "end": v(104.83, -91.45) * mm});
            skLineSegment(sketch, "E1417", {"start": v(104.83, -91.45) * mm, "end": v(105.63, -90.3) * mm});
            skLineSegment(sketch, "E1418", {"start": v(105.63, -90.3) * mm, "end": v(106.55, -89.32) * mm});
            skLineSegment(sketch, "E1419", {"start": v(106.55, -89.32) * mm, "end": v(107.6, -88.5) * mm});
            skLineSegment(sketch, "E1420", {"start": v(107.6, -88.5) * mm, "end": v(108.75, -87.86) * mm});
            skLineSegment(sketch, "E1421", {"start": v(108.75, -87.86) * mm, "end": v(110.03, -87.38) * mm});
            skLineSegment(sketch, "E1422", {"start": v(110.03, -87.38) * mm, "end": v(111.42, -87.08) * mm});
            skLineSegment(sketch, "E1423", {"start": v(111.42, -87.08) * mm, "end": v(112.93, -86.96) * mm});
            skLineSegment(sketch, "E1424", {"start": v(112.93, -86.96) * mm, "end": v(113.32, -86.97) * mm});
            skLineSegment(sketch, "E1425", {"start": v(113.32, -86.97) * mm, "end": v(113.68, -87.02) * mm});
            skLineSegment(sketch, "E1426", {"start": v(113.68, -87.02) * mm, "end": v(114.02, -87.12) * mm});
            skLineSegment(sketch, "E1427", {"start": v(114.02, -87.12) * mm, "end": v(114.34, -87.25) * mm});
            skLineSegment(sketch, "E1428", {"start": v(114.34, -87.25) * mm, "end": v(114.63, -87.42) * mm});
            skLineSegment(sketch, "E1429", {"start": v(114.63, -87.42) * mm, "end": v(114.9, -87.64) * mm});
            skLineSegment(sketch, "E1430", {"start": v(114.9, -87.64) * mm, "end": v(115.15, -87.9) * mm});
            skLineSegment(sketch, "E1431", {"start": v(115.15, -87.9) * mm, "end": v(115.36, -88.2) * mm});
            skLineSegment(sketch, "E1432", {"start": v(115.36, -88.2) * mm, "end": v(115.85, -89.05) * mm});
            skLineSegment(sketch, "E1433", {"start": v(115.85, -89.05) * mm, "end": v(116.24, -89.9) * mm});
            skLineSegment(sketch, "E1434", {"start": v(116.24, -89.9) * mm, "end": v(116.54, -90.78) * mm});
            skLineSegment(sketch, "E1435", {"start": v(116.54, -90.78) * mm, "end": v(116.72, -91.67) * mm});
            skLineSegment(sketch, "E1436", {"start": v(116.72, -91.67) * mm, "end": v(116.78, -92.56) * mm});
            skLineSegment(sketch, "E1437", {"start": v(116.78, -92.56) * mm, "end": v(116.7, -93.46) * mm});
            skLineSegment(sketch, "E1438", {"start": v(116.7, -93.46) * mm, "end": v(116.48, -94.36) * mm});
            skLineSegment(sketch, "E1439", {"start": v(116.48, -94.36) * mm, "end": v(116.1, -95.26) * mm});
            skLineSegment(sketch, "E1440", {"start": v(116.1, -95.26) * mm, "end": v(114.9, -97.32) * mm});
            skLineSegment(sketch, "E1441", {"start": v(114.9, -97.32) * mm, "end": v(113.54, -99.2) * mm});
            skLineSegment(sketch, "E1442", {"start": v(113.54, -99.2) * mm, "end": v(112.04, -100.9) * mm});
            skLineSegment(sketch, "E1443", {"start": v(112.04, -100.9) * mm, "end": v(110.38, -102.4) * mm});
            skLineSegment(sketch, "E1444", {"start": v(110.38, -102.4) * mm, "end": v(108.56, -103.7) * mm});
            skLineSegment(sketch, "E1445", {"start": v(108.56, -103.7) * mm, "end": v(106.58, -104.79) * mm});
            skLineSegment(sketch, "E1446", {"start": v(106.58, -104.79) * mm, "end": v(104.42, -105.66) * mm});
            skLineSegment(sketch, "E1447", {"start": v(104.42, -105.66) * mm, "end": v(102.1, -106.32) * mm});
            skLineSegment(sketch, "E1448", {"start": v(102.1, -106.32) * mm, "end": v(102, -106.34) * mm});
            skLineSegment(sketch, "E1449", {"start": v(102, -106.34) * mm, "end": v(101.9, -106.36) * mm});
            skLineSegment(sketch, "E1450", {"start": v(101.9, -106.36) * mm, "end": v(101.79, -106.38) * mm});
            skLineSegment(sketch, "E1451", {"start": v(101.79, -106.38) * mm, "end": v(101.69, -106.4) * mm});
            skLineSegment(sketch, "E1452", {"start": v(101.69, -106.4) * mm, "end": v(101.58, -106.4) * mm});
            skLineSegment(sketch, "E1453", {"start": v(101.58, -106.4) * mm, "end": v(101.48, -106.42) * mm});
            skLineSegment(sketch, "E1454", {"start": v(101.48, -106.42) * mm, "end": v(101.37, -106.43) * mm});
            skLineSegment(sketch, "E1455", {"start": v(101.37, -106.43) * mm, "end": v(101.27, -106.44) * mm});
            skLineSegment(sketch, "E1456", {"start": v(101.27, -106.44) * mm, "end": v(101.2, -106.44) * mm});
            skLineSegment(sketch, "E1457", {"start": v(101.2, -106.44) * mm, "end": v(101.12, -106.44) * mm});
            skLineSegment(sketch, "E1458", {"start": v(101.12, -106.44) * mm, "end": v(101.04, -106.43) * mm});
            skLineSegment(sketch, "E1459", {"start": v(101.04, -106.43) * mm, "end": v(100.95, -106.43) * mm});
            skLineSegment(sketch, "E1460", {"start": v(100.95, -106.43) * mm, "end": v(100.85, -106.42) * mm});
            skLineSegment(sketch, "E1461", {"start": v(100.85, -106.42) * mm, "end": v(100.74, -106.41) * mm});
            skLineSegment(sketch, "E1462", {"start": v(100.74, -106.41) * mm, "end": v(100.6, -106.4) * mm});
            skLineSegment(sketch, "E1463", {"start": v(100.6, -106.4) * mm, "end": v(100.46, -106.4) * mm});
            skSolve(sketch);
        }
        {
            var Q0;
            Q0=makeQuery(id+"F0.imprint","IMPRINT",FACE,{"disambiguationData":[TD([[makeQuery(id+"F0.imprint","IMPRINT",EDGE,{"derivedFrom":sQuery(id+"F0.wireOp",EDGE,"E0")}),1.0]])]});
            extrude(context, id + "F1", {"entities" : qUnion([Q0]), "depth" : 25 * mm, "offsetDistance" : 25 * mm});
        }
        {
            var Q0;
            Q0=makeQuery(id+"F1.opExtrude","SWEPT_BODY",BODY,{"disambiguationData":[OSD([sQuery(id+"F0.wireOp",EDGE,"E0"),sQuery(id+"F0.wireOp",EDGE,"E1"),sQuery(id+"F0.wireOp",EDGE,"E2"),sQuery(id+"F0.wireOp",EDGE,"E3"),sQuery(id+"F0.wireOp",EDGE,"E4"),sQuery(id+"F0.wireOp",EDGE,"E5"),sQuery(id+"F0.wireOp",EDGE,"E6"),sQuery(id+"F0.wireOp",EDGE,"E7"),sQuery(id+"F0.wireOp",EDGE,"E8"),sQuery(id+"F0.wireOp",EDGE,"E9"),sQuery(id+"F0.wireOp",EDGE,"E10"),sQuery(id+"F0.wireOp",EDGE,"E11"),sQuery(id+"F0.wireOp",EDGE,"E12"),sQuery(id+"F0.wireOp",EDGE,"E13"),sQuery(id+"F0.wireOp",EDGE,"E14"),sQuery(id+"F0.wireOp",EDGE,"E15"),sQuery(id+"F0.wireOp",EDGE,"E16"),sQuery(id+"F0.wireOp",EDGE,"E17"),sQuery(id+"F0.wireOp",EDGE,"E18"),sQuery(id+"F0.wireOp",EDGE,"E19"),sQuery(id+"F0.wireOp",EDGE,"E20"),sQuery(id+"F0.wireOp",EDGE,"E21"),sQuery(id+"F0.wireOp",EDGE,"E22"),sQuery(id+"F0.wireOp",EDGE,"E23"),sQuery(id+"F0.wireOp",EDGE,"E24"),sQuery(id+"F0.wireOp",EDGE,"E25"),sQuery(id+"F0.wireOp",EDGE,"E26"),sQuery(id+"F0.wireOp",EDGE,"E27"),sQuery(id+"F0.wireOp",EDGE,"E28"),sQuery(id+"F0.wireOp",EDGE,"E29"),sQuery(id+"F0.wireOp",EDGE,"E30"),sQuery(id+"F0.wireOp",EDGE,"E31"),sQuery(id+"F0.wireOp",EDGE,"E32"),sQuery(id+"F0.wireOp",EDGE,"E33"),sQuery(id+"F0.wireOp",EDGE,"E34"),sQuery(id+"F0.wireOp",EDGE,"E35"),sQuery(id+"F0.wireOp",EDGE,"E36"),sQuery(id+"F0.wireOp",EDGE,"E37"),sQuery(id+"F0.wireOp",EDGE,"E38"),sQuery(id+"F0.wireOp",EDGE,"E39"),sQuery(id+"F0.wireOp",EDGE,"E40"),sQuery(id+"F0.wireOp",EDGE,"E41"),sQuery(id+"F0.wireOp",EDGE,"E42"),sQuery(id+"F0.wireOp",EDGE,"E43"),sQuery(id+"F0.wireOp",EDGE,"E44"),sQuery(id+"F0.wireOp",EDGE,"E45"),sQuery(id+"F0.wireOp",EDGE,"E46"),sQuery(id+"F0.wireOp",EDGE,"E47"),sQuery(id+"F0.wireOp",EDGE,"E48"),sQuery(id+"F0.wireOp",EDGE,"E49"),sQuery(id+"F0.wireOp",EDGE,"E50"),sQuery(id+"F0.wireOp",EDGE,"E51"),sQuery(id+"F0.wireOp",EDGE,"E52"),sQuery(id+"F0.wireOp",EDGE,"E53"),sQuery(id+"F0.wireOp",EDGE,"E54"),sQuery(id+"F0.wireOp",EDGE,"E55"),sQuery(id+"F0.wireOp",EDGE,"E56"),sQuery(id+"F0.wireOp",EDGE,"E57"),sQuery(id+"F0.wireOp",EDGE,"E58"),sQuery(id+"F0.wireOp",EDGE,"E59"),sQuery(id+"F0.wireOp",EDGE,"E60"),sQuery(id+"F0.wireOp",EDGE,"E61"),sQuery(id+"F0.wireOp",EDGE,"E62"),sQuery(id+"F0.wireOp",EDGE,"E63"),sQuery(id+"F0.wireOp",EDGE,"E64"),sQuery(id+"F0.wireOp",EDGE,"E65"),sQuery(id+"F0.wireOp",EDGE,"E66"),sQuery(id+"F0.wireOp",EDGE,"E67"),sQuery(id+"F0.wireOp",EDGE,"E68"),sQuery(id+"F0.wireOp",EDGE,"E69"),sQuery(id+"F0.wireOp",EDGE,"E70"),sQuery(id+"F0.wireOp",EDGE,"E71"),sQuery(id+"F0.wireOp",EDGE,"E72"),sQuery(id+"F0.wireOp",EDGE,"E73"),sQuery(id+"F0.wireOp",EDGE,"E74"),sQuery(id+"F0.wireOp",EDGE,"E75"),sQuery(id+"F0.wireOp",EDGE,"E76"),sQuery(id+"F0.wireOp",EDGE,"E77"),sQuery(id+"F0.wireOp",EDGE,"E78"),sQuery(id+"F0.wireOp",EDGE,"E79"),sQuery(id+"F0.wireOp",EDGE,"E80"),sQuery(id+"F0.wireOp",EDGE,"E81"),sQuery(id+"F0.wireOp",EDGE,"E82"),sQuery(id+"F0.wireOp",EDGE,"E83"),sQuery(id+"F0.wireOp",EDGE,"E84"),sQuery(id+"F0.wireOp",EDGE,"E85"),sQuery(id+"F0.wireOp",EDGE,"E86"),sQuery(id+"F0.wireOp",EDGE,"E87"),sQuery(id+"F0.wireOp",EDGE,"E88"),sQuery(id+"F0.wireOp",EDGE,"E89"),sQuery(id+"F0.wireOp",EDGE,"E90"),sQuery(id+"F0.wireOp",EDGE,"E91"),sQuery(id+"F0.wireOp",EDGE,"E92"),sQuery(id+"F0.wireOp",EDGE,"E93"),sQuery(id+"F0.wireOp",EDGE,"E94"),sQuery(id+"F0.wireOp",EDGE,"E95"),sQuery(id+"F0.wireOp",EDGE,"E96"),sQuery(id+"F0.wireOp",EDGE,"E97"),sQuery(id+"F0.wireOp",EDGE,"E98"),sQuery(id+"F0.wireOp",EDGE,"E99"),sQuery(id+"F0.wireOp",EDGE,"E100"),sQuery(id+"F0.wireOp",EDGE,"E101"),sQuery(id+"F0.wireOp",EDGE,"E102"),sQuery(id+"F0.wireOp",EDGE,"E103"),sQuery(id+"F0.wireOp",EDGE,"E104"),sQuery(id+"F0.wireOp",EDGE,"E105"),sQuery(id+"F0.wireOp",EDGE,"E106"),sQuery(id+"F0.wireOp",EDGE,"E107"),sQuery(id+"F0.wireOp",EDGE,"E108"),sQuery(id+"F0.wireOp",EDGE,"E109"),sQuery(id+"F0.wireOp",EDGE,"E110"),sQuery(id+"F0.wireOp",EDGE,"E111"),sQuery(id+"F0.wireOp",EDGE,"E112"),sQuery(id+"F0.wireOp",EDGE,"E113"),sQuery(id+"F0.wireOp",EDGE,"E114"),sQuery(id+"F0.wireOp",EDGE,"E115"),sQuery(id+"F0.wireOp",EDGE,"E116"),sQuery(id+"F0.wireOp",EDGE,"E117"),sQuery(id+"F0.wireOp",EDGE,"E118"),sQuery(id+"F0.wireOp",EDGE,"E119"),sQuery(id+"F0.wireOp",EDGE,"E120"),sQuery(id+"F0.wireOp",EDGE,"E121"),sQuery(id+"F0.wireOp",EDGE,"E122"),sQuery(id+"F0.wireOp",EDGE,"E123"),sQuery(id+"F0.wireOp",EDGE,"E124"),sQuery(id+"F0.wireOp",EDGE,"E125"),sQuery(id+"F0.wireOp",EDGE,"E126"),sQuery(id+"F0.wireOp",EDGE,"E127"),sQuery(id+"F0.wireOp",EDGE,"E128"),sQuery(id+"F0.wireOp",EDGE,"E129"),sQuery(id+"F0.wireOp",EDGE,"E130"),sQuery(id+"F0.wireOp",EDGE,"E131"),sQuery(id+"F0.wireOp",EDGE,"E132"),sQuery(id+"F0.wireOp",EDGE,"E133"),sQuery(id+"F0.wireOp",EDGE,"E134"),sQuery(id+"F0.wireOp",EDGE,"E135"),sQuery(id+"F0.wireOp",EDGE,"E136"),sQuery(id+"F0.wireOp",EDGE,"E137"),sQuery(id+"F0.wireOp",EDGE,"E138"),sQuery(id+"F0.wireOp",EDGE,"E139"),sQuery(id+"F0.wireOp",EDGE,"E140"),sQuery(id+"F0.wireOp",EDGE,"E141"),sQuery(id+"F0.wireOp",EDGE,"E142"),sQuery(id+"F0.wireOp",EDGE,"E143"),sQuery(id+"F0.wireOp",EDGE,"E144"),sQuery(id+"F0.wireOp",EDGE,"E145"),sQuery(id+"F0.wireOp",EDGE,"E146"),sQuery(id+"F0.wireOp",EDGE,"E147"),sQuery(id+"F0.wireOp",EDGE,"E148"),sQuery(id+"F0.wireOp",EDGE,"E149"),sQuery(id+"F0.wireOp",EDGE,"E150"),sQuery(id+"F0.wireOp",EDGE,"E151"),sQuery(id+"F0.wireOp",EDGE,"E152"),sQuery(id+"F0.wireOp",EDGE,"E153"),sQuery(id+"F0.wireOp",EDGE,"E154"),sQuery(id+"F0.wireOp",EDGE,"E155"),sQuery(id+"F0.wireOp",EDGE,"E156"),sQuery(id+"F0.wireOp",EDGE,"E157"),sQuery(id+"F0.wireOp",EDGE,"E158"),sQuery(id+"F0.wireOp",EDGE,"E159"),sQuery(id+"F0.wireOp",EDGE,"E160"),sQuery(id+"F0.wireOp",EDGE,"E161"),sQuery(id+"F0.wireOp",EDGE,"E162"),sQuery(id+"F0.wireOp",EDGE,"E163"),sQuery(id+"F0.wireOp",EDGE,"E164"),sQuery(id+"F0.wireOp",EDGE,"E165"),sQuery(id+"F0.wireOp",EDGE,"E166"),sQuery(id+"F0.wireOp",EDGE,"E167"),sQuery(id+"F0.wireOp",EDGE,"E168"),sQuery(id+"F0.wireOp",EDGE,"E169"),sQuery(id+"F0.wireOp",EDGE,"E170"),sQuery(id+"F0.wireOp",EDGE,"E171"),sQuery(id+"F0.wireOp",EDGE,"E172"),sQuery(id+"F0.wireOp",EDGE,"E173"),sQuery(id+"F0.wireOp",EDGE,"E174"),sQuery(id+"F0.wireOp",EDGE,"E175"),sQuery(id+"F0.wireOp",EDGE,"E176"),sQuery(id+"F0.wireOp",EDGE,"E177"),sQuery(id+"F0.wireOp",EDGE,"E178"),sQuery(id+"F0.wireOp",EDGE,"E179"),sQuery(id+"F0.wireOp",EDGE,"E180"),sQuery(id+"F0.wireOp",EDGE,"E181"),sQuery(id+"F0.wireOp",EDGE,"E182"),sQuery(id+"F0.wireOp",EDGE,"E183"),sQuery(id+"F0.wireOp",EDGE,"E184"),sQuery(id+"F0.wireOp",EDGE,"E185"),sQuery(id+"F0.wireOp",EDGE,"E186"),sQuery(id+"F0.wireOp",EDGE,"E187"),sQuery(id+"F0.wireOp",EDGE,"E188"),sQuery(id+"F0.wireOp",EDGE,"E189"),sQuery(id+"F0.wireOp",EDGE,"E190"),sQuery(id+"F0.wireOp",EDGE,"E191"),sQuery(id+"F0.wireOp",EDGE,"E192"),sQuery(id+"F0.wireOp",EDGE,"E193"),sQuery(id+"F0.wireOp",EDGE,"E194"),sQuery(id+"F0.wireOp",EDGE,"E195"),sQuery(id+"F0.wireOp",EDGE,"E196"),sQuery(id+"F0.wireOp",EDGE,"E197"),sQuery(id+"F0.wireOp",EDGE,"E198"),sQuery(id+"F0.wireOp",EDGE,"E199"),sQuery(id+"F0.wireOp",EDGE,"E200"),sQuery(id+"F0.wireOp",EDGE,"E201"),sQuery(id+"F0.wireOp",EDGE,"E202"),sQuery(id+"F0.wireOp",EDGE,"E203"),sQuery(id+"F0.wireOp",EDGE,"E204"),sQuery(id+"F0.wireOp",EDGE,"E205"),sQuery(id+"F0.wireOp",EDGE,"E206"),sQuery(id+"F0.wireOp",EDGE,"E207"),sQuery(id+"F0.wireOp",EDGE,"E208"),sQuery(id+"F0.wireOp",EDGE,"E209"),sQuery(id+"F0.wireOp",EDGE,"E210"),sQuery(id+"F0.wireOp",EDGE,"E211"),sQuery(id+"F0.wireOp",EDGE,"E212"),sQuery(id+"F0.wireOp",EDGE,"E213"),sQuery(id+"F0.wireOp",EDGE,"E214"),sQuery(id+"F0.wireOp",EDGE,"E215"),sQuery(id+"F0.wireOp",EDGE,"E216"),sQuery(id+"F0.wireOp",EDGE,"E217"),sQuery(id+"F0.wireOp",EDGE,"E218"),sQuery(id+"F0.wireOp",EDGE,"E219"),sQuery(id+"F0.wireOp",EDGE,"E220"),sQuery(id+"F0.wireOp",EDGE,"E221"),sQuery(id+"F0.wireOp",EDGE,"E222"),sQuery(id+"F0.wireOp",EDGE,"E223"),sQuery(id+"F0.wireOp",EDGE,"E224"),sQuery(id+"F0.wireOp",EDGE,"E225"),sQuery(id+"F0.wireOp",EDGE,"E226"),sQuery(id+"F0.wireOp",EDGE,"E227"),sQuery(id+"F0.wireOp",EDGE,"E228"),sQuery(id+"F0.wireOp",EDGE,"E229"),sQuery(id+"F0.wireOp",EDGE,"E230"),sQuery(id+"F0.wireOp",EDGE,"E231"),sQuery(id+"F0.wireOp",EDGE,"E232"),sQuery(id+"F0.wireOp",EDGE,"E233"),sQuery(id+"F0.wireOp",EDGE,"E234"),sQuery(id+"F0.wireOp",EDGE,"E235"),sQuery(id+"F0.wireOp",EDGE,"E236"),sQuery(id+"F0.wireOp",EDGE,"E237"),sQuery(id+"F0.wireOp",EDGE,"E238"),sQuery(id+"F0.wireOp",EDGE,"E239"),sQuery(id+"F0.wireOp",EDGE,"E240"),sQuery(id+"F0.wireOp",EDGE,"E241"),sQuery(id+"F0.wireOp",EDGE,"E242"),sQuery(id+"F0.wireOp",EDGE,"E243"),sQuery(id+"F0.wireOp",EDGE,"E244"),sQuery(id+"F0.wireOp",EDGE,"E245"),sQuery(id+"F0.wireOp",EDGE,"E246"),sQuery(id+"F0.wireOp",EDGE,"E247"),sQuery(id+"F0.wireOp",EDGE,"E248"),sQuery(id+"F0.wireOp",EDGE,"E249"),sQuery(id+"F0.wireOp",EDGE,"E250"),sQuery(id+"F0.wireOp",EDGE,"E251"),sQuery(id+"F0.wireOp",EDGE,"E252"),sQuery(id+"F0.wireOp",EDGE,"E253"),sQuery(id+"F0.wireOp",EDGE,"E254"),sQuery(id+"F0.wireOp",EDGE,"E255"),sQuery(id+"F0.wireOp",EDGE,"E256"),sQuery(id+"F0.wireOp",EDGE,"E257"),sQuery(id+"F0.wireOp",EDGE,"E258"),sQuery(id+"F0.wireOp",EDGE,"E259"),sQuery(id+"F0.wireOp",EDGE,"E260"),sQuery(id+"F0.wireOp",EDGE,"E261"),sQuery(id+"F0.wireOp",EDGE,"E262"),sQuery(id+"F0.wireOp",EDGE,"E263"),sQuery(id+"F0.wireOp",EDGE,"E264"),sQuery(id+"F0.wireOp",EDGE,"E265"),sQuery(id+"F0.wireOp",EDGE,"E266"),sQuery(id+"F0.wireOp",EDGE,"E267"),sQuery(id+"F0.wireOp",EDGE,"E268"),sQuery(id+"F0.wireOp",EDGE,"E269"),sQuery(id+"F0.wireOp",EDGE,"E270"),sQuery(id+"F0.wireOp",EDGE,"E271"),sQuery(id+"F0.wireOp",EDGE,"E272"),sQuery(id+"F0.wireOp",EDGE,"E273"),sQuery(id+"F0.wireOp",EDGE,"E274"),sQuery(id+"F0.wireOp",EDGE,"E275"),sQuery(id+"F0.wireOp",EDGE,"E276"),sQuery(id+"F0.wireOp",EDGE,"E277"),sQuery(id+"F0.wireOp",EDGE,"E278"),sQuery(id+"F0.wireOp",EDGE,"E279"),sQuery(id+"F0.wireOp",EDGE,"E280"),sQuery(id+"F0.wireOp",EDGE,"E281"),sQuery(id+"F0.wireOp",EDGE,"E282"),sQuery(id+"F0.wireOp",EDGE,"E283"),sQuery(id+"F0.wireOp",EDGE,"E284"),sQuery(id+"F0.wireOp",EDGE,"E285"),sQuery(id+"F0.wireOp",EDGE,"E286"),sQuery(id+"F0.wireOp",EDGE,"E287"),sQuery(id+"F0.wireOp",EDGE,"E288"),sQuery(id+"F0.wireOp",EDGE,"E289"),sQuery(id+"F0.wireOp",EDGE,"E290"),sQuery(id+"F0.wireOp",EDGE,"E291"),sQuery(id+"F0.wireOp",EDGE,"E292"),sQuery(id+"F0.wireOp",EDGE,"E293"),sQuery(id+"F0.wireOp",EDGE,"E294"),sQuery(id+"F0.wireOp",EDGE,"E295"),sQuery(id+"F0.wireOp",EDGE,"E296"),sQuery(id+"F0.wireOp",EDGE,"E297"),sQuery(id+"F0.wireOp",EDGE,"E298"),sQuery(id+"F0.wireOp",EDGE,"E299"),sQuery(id+"F0.wireOp",EDGE,"E300"),sQuery(id+"F0.wireOp",EDGE,"E301"),sQuery(id+"F0.wireOp",EDGE,"E302"),sQuery(id+"F0.wireOp",EDGE,"E303"),sQuery(id+"F0.wireOp",EDGE,"E304"),sQuery(id+"F0.wireOp",EDGE,"E305"),sQuery(id+"F0.wireOp",EDGE,"E306"),sQuery(id+"F0.wireOp",EDGE,"E307"),sQuery(id+"F0.wireOp",EDGE,"E308"),sQuery(id+"F0.wireOp",EDGE,"E309"),sQuery(id+"F0.wireOp",EDGE,"E310"),sQuery(id+"F0.wireOp",EDGE,"E311"),sQuery(id+"F0.wireOp",EDGE,"E312"),sQuery(id+"F0.wireOp",EDGE,"E313"),sQuery(id+"F0.wireOp",EDGE,"E314"),sQuery(id+"F0.wireOp",EDGE,"E315"),sQuery(id+"F0.wireOp",EDGE,"E316"),sQuery(id+"F0.wireOp",EDGE,"E317"),sQuery(id+"F0.wireOp",EDGE,"E318"),sQuery(id+"F0.wireOp",EDGE,"E319"),sQuery(id+"F0.wireOp",EDGE,"E320"),sQuery(id+"F0.wireOp",EDGE,"E321"),sQuery(id+"F0.wireOp",EDGE,"E322"),sQuery(id+"F0.wireOp",EDGE,"E323"),sQuery(id+"F0.wireOp",EDGE,"E324"),sQuery(id+"F0.wireOp",EDGE,"E325"),sQuery(id+"F0.wireOp",EDGE,"E326"),sQuery(id+"F0.wireOp",EDGE,"E327"),sQuery(id+"F0.wireOp",EDGE,"E328"),sQuery(id+"F0.wireOp",EDGE,"E329"),sQuery(id+"F0.wireOp",EDGE,"E330"),sQuery(id+"F0.wireOp",EDGE,"E331"),sQuery(id+"F0.wireOp",EDGE,"E332"),sQuery(id+"F0.wireOp",EDGE,"E333"),sQuery(id+"F0.wireOp",EDGE,"E334"),sQuery(id+"F0.wireOp",EDGE,"E335"),sQuery(id+"F0.wireOp",EDGE,"E336"),sQuery(id+"F0.wireOp",EDGE,"E337"),sQuery(id+"F0.wireOp",EDGE,"E338"),sQuery(id+"F0.wireOp",EDGE,"E339"),sQuery(id+"F0.wireOp",EDGE,"E340"),sQuery(id+"F0.wireOp",EDGE,"E341"),sQuery(id+"F0.wireOp",EDGE,"E342"),sQuery(id+"F0.wireOp",EDGE,"E343"),sQuery(id+"F0.wireOp",EDGE,"E344"),sQuery(id+"F0.wireOp",EDGE,"E345"),sQuery(id+"F0.wireOp",EDGE,"E346"),sQuery(id+"F0.wireOp",EDGE,"E347"),sQuery(id+"F0.wireOp",EDGE,"E348"),sQuery(id+"F0.wireOp",EDGE,"E349"),sQuery(id+"F0.wireOp",EDGE,"E350"),sQuery(id+"F0.wireOp",EDGE,"E351"),sQuery(id+"F0.wireOp",EDGE,"E352"),sQuery(id+"F0.wireOp",EDGE,"E353"),sQuery(id+"F0.wireOp",EDGE,"E354"),sQuery(id+"F0.wireOp",EDGE,"E355"),sQuery(id+"F0.wireOp",EDGE,"E356"),sQuery(id+"F0.wireOp",EDGE,"E357"),sQuery(id+"F0.wireOp",EDGE,"E358"),sQuery(id+"F0.wireOp",EDGE,"E359"),sQuery(id+"F0.wireOp",EDGE,"E360"),sQuery(id+"F0.wireOp",EDGE,"E361"),sQuery(id+"F0.wireOp",EDGE,"E362"),sQuery(id+"F0.wireOp",EDGE,"E363"),sQuery(id+"F0.wireOp",EDGE,"E364"),sQuery(id+"F0.wireOp",EDGE,"E365"),sQuery(id+"F0.wireOp",EDGE,"E366"),sQuery(id+"F0.wireOp",EDGE,"E367"),sQuery(id+"F0.wireOp",EDGE,"E368"),sQuery(id+"F0.wireOp",EDGE,"E369"),sQuery(id+"F0.wireOp",EDGE,"E370"),sQuery(id+"F0.wireOp",EDGE,"E371"),sQuery(id+"F0.wireOp",EDGE,"E372"),sQuery(id+"F0.wireOp",EDGE,"E373"),sQuery(id+"F0.wireOp",EDGE,"E374"),sQuery(id+"F0.wireOp",EDGE,"E375"),sQuery(id+"F0.wireOp",EDGE,"E376"),sQuery(id+"F0.wireOp",EDGE,"E377"),sQuery(id+"F0.wireOp",EDGE,"E378"),sQuery(id+"F0.wireOp",EDGE,"E379"),sQuery(id+"F0.wireOp",EDGE,"E380"),sQuery(id+"F0.wireOp",EDGE,"E381"),sQuery(id+"F0.wireOp",EDGE,"E382"),sQuery(id+"F0.wireOp",EDGE,"E383"),sQuery(id+"F0.wireOp",EDGE,"E384"),sQuery(id+"F0.wireOp",EDGE,"E385"),sQuery(id+"F0.wireOp",EDGE,"E386"),sQuery(id+"F0.wireOp",EDGE,"E387"),sQuery(id+"F0.wireOp",EDGE,"E388"),sQuery(id+"F0.wireOp",EDGE,"E389"),sQuery(id+"F0.wireOp",EDGE,"E390"),sQuery(id+"F0.wireOp",EDGE,"E391"),sQuery(id+"F0.wireOp",EDGE,"E392"),sQuery(id+"F0.wireOp",EDGE,"E393"),sQuery(id+"F0.wireOp",EDGE,"E394"),sQuery(id+"F0.wireOp",EDGE,"E395"),sQuery(id+"F0.wireOp",EDGE,"E396"),sQuery(id+"F0.wireOp",EDGE,"E397"),sQuery(id+"F0.wireOp",EDGE,"E398"),sQuery(id+"F0.wireOp",EDGE,"E399"),sQuery(id+"F0.wireOp",EDGE,"E400"),sQuery(id+"F0.wireOp",EDGE,"E401"),sQuery(id+"F0.wireOp",EDGE,"E402"),sQuery(id+"F0.wireOp",EDGE,"E403"),sQuery(id+"F0.wireOp",EDGE,"E404"),sQuery(id+"F0.wireOp",EDGE,"E405"),sQuery(id+"F0.wireOp",EDGE,"E406"),sQuery(id+"F0.wireOp",EDGE,"E407"),sQuery(id+"F0.wireOp",EDGE,"E408"),sQuery(id+"F0.wireOp",EDGE,"E409"),sQuery(id+"F0.wireOp",EDGE,"E410"),sQuery(id+"F0.wireOp",EDGE,"E411"),sQuery(id+"F0.wireOp",EDGE,"E412"),sQuery(id+"F0.wireOp",EDGE,"E413"),sQuery(id+"F0.wireOp",EDGE,"E414"),sQuery(id+"F0.wireOp",EDGE,"E415"),sQuery(id+"F0.wireOp",EDGE,"E416"),sQuery(id+"F0.wireOp",EDGE,"E417"),sQuery(id+"F0.wireOp",EDGE,"E418"),sQuery(id+"F0.wireOp",EDGE,"E419"),sQuery(id+"F0.wireOp",EDGE,"E420"),sQuery(id+"F0.wireOp",EDGE,"E421"),sQuery(id+"F0.wireOp",EDGE,"E422"),sQuery(id+"F0.wireOp",EDGE,"E423"),sQuery(id+"F0.wireOp",EDGE,"E424"),sQuery(id+"F0.wireOp",EDGE,"E425"),sQuery(id+"F0.wireOp",EDGE,"E426"),sQuery(id+"F0.wireOp",EDGE,"E427"),sQuery(id+"F0.wireOp",EDGE,"E428"),sQuery(id+"F0.wireOp",EDGE,"E429"),sQuery(id+"F0.wireOp",EDGE,"E430"),sQuery(id+"F0.wireOp",EDGE,"E431"),sQuery(id+"F0.wireOp",EDGE,"E432"),sQuery(id+"F0.wireOp",EDGE,"E433"),sQuery(id+"F0.wireOp",EDGE,"E434"),sQuery(id+"F0.wireOp",EDGE,"E435"),sQuery(id+"F0.wireOp",EDGE,"E436"),sQuery(id+"F0.wireOp",EDGE,"E437"),sQuery(id+"F0.wireOp",EDGE,"E438"),sQuery(id+"F0.wireOp",EDGE,"E439"),sQuery(id+"F0.wireOp",EDGE,"E440"),sQuery(id+"F0.wireOp",EDGE,"E441"),sQuery(id+"F0.wireOp",EDGE,"E442"),sQuery(id+"F0.wireOp",EDGE,"E443"),sQuery(id+"F0.wireOp",EDGE,"E444"),sQuery(id+"F0.wireOp",EDGE,"E445"),sQuery(id+"F0.wireOp",EDGE,"E446"),sQuery(id+"F0.wireOp",EDGE,"E447"),sQuery(id+"F0.wireOp",EDGE,"E448"),sQuery(id+"F0.wireOp",EDGE,"E449"),sQuery(id+"F0.wireOp",EDGE,"E450"),sQuery(id+"F0.wireOp",EDGE,"E451"),sQuery(id+"F0.wireOp",EDGE,"E452"),sQuery(id+"F0.wireOp",EDGE,"E453"),sQuery(id+"F0.wireOp",EDGE,"E454"),sQuery(id+"F0.wireOp",EDGE,"E455"),sQuery(id+"F0.wireOp",EDGE,"E456"),sQuery(id+"F0.wireOp",EDGE,"E457"),sQuery(id+"F0.wireOp",EDGE,"E458"),sQuery(id+"F0.wireOp",EDGE,"E459"),sQuery(id+"F0.wireOp",EDGE,"E460"),sQuery(id+"F0.wireOp",EDGE,"E461"),sQuery(id+"F0.wireOp",EDGE,"E462"),sQuery(id+"F0.wireOp",EDGE,"E463"),sQuery(id+"F0.wireOp",EDGE,"E464"),sQuery(id+"F0.wireOp",EDGE,"E465"),sQuery(id+"F0.wireOp",EDGE,"E466"),sQuery(id+"F0.wireOp",EDGE,"E467"),sQuery(id+"F0.wireOp",EDGE,"E468"),sQuery(id+"F0.wireOp",EDGE,"E469"),sQuery(id+"F0.wireOp",EDGE,"E470"),sQuery(id+"F0.wireOp",EDGE,"E471"),sQuery(id+"F0.wireOp",EDGE,"E472"),sQuery(id+"F0.wireOp",EDGE,"E473"),sQuery(id+"F0.wireOp",EDGE,"E474"),sQuery(id+"F0.wireOp",EDGE,"E475"),sQuery(id+"F0.wireOp",EDGE,"E476"),sQuery(id+"F0.wireOp",EDGE,"E477"),sQuery(id+"F0.wireOp",EDGE,"E478"),sQuery(id+"F0.wireOp",EDGE,"E479"),sQuery(id+"F0.wireOp",EDGE,"E480"),sQuery(id+"F0.wireOp",EDGE,"E481"),sQuery(id+"F0.wireOp",EDGE,"E482"),sQuery(id+"F0.wireOp",EDGE,"E483"),sQuery(id+"F0.wireOp",EDGE,"E484"),sQuery(id+"F0.wireOp",EDGE,"E485"),sQuery(id+"F0.wireOp",EDGE,"E486"),sQuery(id+"F0.wireOp",EDGE,"E487"),sQuery(id+"F0.wireOp",EDGE,"E488"),sQuery(id+"F0.wireOp",EDGE,"E489"),sQuery(id+"F0.wireOp",EDGE,"E490"),sQuery(id+"F0.wireOp",EDGE,"E491"),sQuery(id+"F0.wireOp",EDGE,"E492"),sQuery(id+"F0.wireOp",EDGE,"E493"),sQuery(id+"F0.wireOp",EDGE,"E494"),sQuery(id+"F0.wireOp",EDGE,"E495"),sQuery(id+"F0.wireOp",EDGE,"E496"),sQuery(id+"F0.wireOp",EDGE,"E497"),sQuery(id+"F0.wireOp",EDGE,"E498"),sQuery(id+"F0.wireOp",EDGE,"E499"),sQuery(id+"F0.wireOp",EDGE,"E500"),sQuery(id+"F0.wireOp",EDGE,"E501"),sQuery(id+"F0.wireOp",EDGE,"E502"),sQuery(id+"F0.wireOp",EDGE,"E503"),sQuery(id+"F0.wireOp",EDGE,"E504"),sQuery(id+"F0.wireOp",EDGE,"E505"),sQuery(id+"F0.wireOp",EDGE,"E506"),sQuery(id+"F0.wireOp",EDGE,"E507"),sQuery(id+"F0.wireOp",EDGE,"E508"),sQuery(id+"F0.wireOp",EDGE,"E509"),sQuery(id+"F0.wireOp",EDGE,"E510"),sQuery(id+"F0.wireOp",EDGE,"E511"),sQuery(id+"F0.wireOp",EDGE,"E512"),sQuery(id+"F0.wireOp",EDGE,"E513"),sQuery(id+"F0.wireOp",EDGE,"E514"),sQuery(id+"F0.wireOp",EDGE,"E515"),sQuery(id+"F0.wireOp",EDGE,"E516"),sQuery(id+"F0.wireOp",EDGE,"E517"),sQuery(id+"F0.wireOp",EDGE,"E518"),sQuery(id+"F0.wireOp",EDGE,"E519"),sQuery(id+"F0.wireOp",EDGE,"E520"),sQuery(id+"F0.wireOp",EDGE,"E521"),sQuery(id+"F0.wireOp",EDGE,"E522"),sQuery(id+"F0.wireOp",EDGE,"E523"),sQuery(id+"F0.wireOp",EDGE,"E524"),sQuery(id+"F0.wireOp",EDGE,"E525"),sQuery(id+"F0.wireOp",EDGE,"E526"),sQuery(id+"F0.wireOp",EDGE,"E527"),sQuery(id+"F0.wireOp",EDGE,"E528"),sQuery(id+"F0.wireOp",EDGE,"E529"),sQuery(id+"F0.wireOp",EDGE,"E530"),sQuery(id+"F0.wireOp",EDGE,"E531"),sQuery(id+"F0.wireOp",EDGE,"E532"),sQuery(id+"F0.wireOp",EDGE,"E533"),sQuery(id+"F0.wireOp",EDGE,"E534"),sQuery(id+"F0.wireOp",EDGE,"E535"),sQuery(id+"F0.wireOp",EDGE,"E536"),sQuery(id+"F0.wireOp",EDGE,"E537"),sQuery(id+"F0.wireOp",EDGE,"E538"),sQuery(id+"F0.wireOp",EDGE,"E539"),sQuery(id+"F0.wireOp",EDGE,"E540"),sQuery(id+"F0.wireOp",EDGE,"E541"),sQuery(id+"F0.wireOp",EDGE,"E542"),sQuery(id+"F0.wireOp",EDGE,"E543"),sQuery(id+"F0.wireOp",EDGE,"E544"),sQuery(id+"F0.wireOp",EDGE,"E545"),sQuery(id+"F0.wireOp",EDGE,"E546"),sQuery(id+"F0.wireOp",EDGE,"E547"),sQuery(id+"F0.wireOp",EDGE,"E548"),sQuery(id+"F0.wireOp",EDGE,"E549"),sQuery(id+"F0.wireOp",EDGE,"E550"),sQuery(id+"F0.wireOp",EDGE,"E551"),sQuery(id+"F0.wireOp",EDGE,"E552"),sQuery(id+"F0.wireOp",EDGE,"E553"),sQuery(id+"F0.wireOp",EDGE,"E554"),sQuery(id+"F0.wireOp",EDGE,"E555"),sQuery(id+"F0.wireOp",EDGE,"E556"),sQuery(id+"F0.wireOp",EDGE,"E557"),sQuery(id+"F0.wireOp",EDGE,"E558"),sQuery(id+"F0.wireOp",EDGE,"E559"),sQuery(id+"F0.wireOp",EDGE,"E560"),sQuery(id+"F0.wireOp",EDGE,"E561"),sQuery(id+"F0.wireOp",EDGE,"E562"),sQuery(id+"F0.wireOp",EDGE,"E563"),sQuery(id+"F0.wireOp",EDGE,"E564"),sQuery(id+"F0.wireOp",EDGE,"E565"),sQuery(id+"F0.wireOp",EDGE,"E566"),sQuery(id+"F0.wireOp",EDGE,"E567"),sQuery(id+"F0.wireOp",EDGE,"E568"),sQuery(id+"F0.wireOp",EDGE,"E569"),sQuery(id+"F0.wireOp",EDGE,"E570"),sQuery(id+"F0.wireOp",EDGE,"E571"),sQuery(id+"F0.wireOp",EDGE,"E572"),sQuery(id+"F0.wireOp",EDGE,"E573"),sQuery(id+"F0.wireOp",EDGE,"E574"),sQuery(id+"F0.wireOp",EDGE,"E575"),sQuery(id+"F0.wireOp",EDGE,"E576"),sQuery(id+"F0.wireOp",EDGE,"E577"),sQuery(id+"F0.wireOp",EDGE,"E578"),sQuery(id+"F0.wireOp",EDGE,"E579"),sQuery(id+"F0.wireOp",EDGE,"E580"),sQuery(id+"F0.wireOp",EDGE,"E581"),sQuery(id+"F0.wireOp",EDGE,"E582"),sQuery(id+"F0.wireOp",EDGE,"E583"),sQuery(id+"F0.wireOp",EDGE,"E584"),sQuery(id+"F0.wireOp",EDGE,"E585"),sQuery(id+"F0.wireOp",EDGE,"E586"),sQuery(id+"F0.wireOp",EDGE,"E587"),sQuery(id+"F0.wireOp",EDGE,"E588"),sQuery(id+"F0.wireOp",EDGE,"E589"),sQuery(id+"F0.wireOp",EDGE,"E590"),sQuery(id+"F0.wireOp",EDGE,"E591"),sQuery(id+"F0.wireOp",EDGE,"E592"),sQuery(id+"F0.wireOp",EDGE,"E593"),sQuery(id+"F0.wireOp",EDGE,"E594"),sQuery(id+"F0.wireOp",EDGE,"E595"),sQuery(id+"F0.wireOp",EDGE,"E596"),sQuery(id+"F0.wireOp",EDGE,"E597"),sQuery(id+"F0.wireOp",EDGE,"E598"),sQuery(id+"F0.wireOp",EDGE,"E599"),sQuery(id+"F0.wireOp",EDGE,"E600"),sQuery(id+"F0.wireOp",EDGE,"E601"),sQuery(id+"F0.wireOp",EDGE,"E602"),sQuery(id+"F0.wireOp",EDGE,"E603"),sQuery(id+"F0.wireOp",EDGE,"E604"),sQuery(id+"F0.wireOp",EDGE,"E605"),sQuery(id+"F0.wireOp",EDGE,"E606"),sQuery(id+"F0.wireOp",EDGE,"E607"),sQuery(id+"F0.wireOp",EDGE,"E608"),sQuery(id+"F0.wireOp",EDGE,"E609"),sQuery(id+"F0.wireOp",EDGE,"E610"),sQuery(id+"F0.wireOp",EDGE,"E611"),sQuery(id+"F0.wireOp",EDGE,"E612"),sQuery(id+"F0.wireOp",EDGE,"E613"),sQuery(id+"F0.wireOp",EDGE,"E614"),sQuery(id+"F0.wireOp",EDGE,"E615"),sQuery(id+"F0.wireOp",EDGE,"E616"),sQuery(id+"F0.wireOp",EDGE,"E617"),sQuery(id+"F0.wireOp",EDGE,"E618"),sQuery(id+"F0.wireOp",EDGE,"E619"),sQuery(id+"F0.wireOp",EDGE,"E620"),sQuery(id+"F0.wireOp",EDGE,"E621"),sQuery(id+"F0.wireOp",EDGE,"E622"),sQuery(id+"F0.wireOp",EDGE,"E623"),sQuery(id+"F0.wireOp",EDGE,"E624"),sQuery(id+"F0.wireOp",EDGE,"E625"),sQuery(id+"F0.wireOp",EDGE,"E626"),sQuery(id+"F0.wireOp",EDGE,"E627"),sQuery(id+"F0.wireOp",EDGE,"E628"),sQuery(id+"F0.wireOp",EDGE,"E629"),sQuery(id+"F0.wireOp",EDGE,"E630"),sQuery(id+"F0.wireOp",EDGE,"E631"),sQuery(id+"F0.wireOp",EDGE,"E632"),sQuery(id+"F0.wireOp",EDGE,"E633"),sQuery(id+"F0.wireOp",EDGE,"E634"),sQuery(id+"F0.wireOp",EDGE,"E635"),sQuery(id+"F0.wireOp",EDGE,"E636"),sQuery(id+"F0.wireOp",EDGE,"E637"),sQuery(id+"F0.wireOp",EDGE,"E638"),sQuery(id+"F0.wireOp",EDGE,"E639"),sQuery(id+"F0.wireOp",EDGE,"E640"),sQuery(id+"F0.wireOp",EDGE,"E641"),sQuery(id+"F0.wireOp",EDGE,"E642"),sQuery(id+"F0.wireOp",EDGE,"E643"),sQuery(id+"F0.wireOp",EDGE,"E644"),sQuery(id+"F0.wireOp",EDGE,"E645"),sQuery(id+"F0.wireOp",EDGE,"E646"),sQuery(id+"F0.wireOp",EDGE,"E647"),sQuery(id+"F0.wireOp",EDGE,"E648"),sQuery(id+"F0.wireOp",EDGE,"E649"),sQuery(id+"F0.wireOp",EDGE,"E650"),sQuery(id+"F0.wireOp",EDGE,"E651"),sQuery(id+"F0.wireOp",EDGE,"E652"),sQuery(id+"F0.wireOp",EDGE,"E653"),sQuery(id+"F0.wireOp",EDGE,"E654"),sQuery(id+"F0.wireOp",EDGE,"E655"),sQuery(id+"F0.wireOp",EDGE,"E656"),sQuery(id+"F0.wireOp",EDGE,"E657"),sQuery(id+"F0.wireOp",EDGE,"E658"),sQuery(id+"F0.wireOp",EDGE,"E659"),sQuery(id+"F0.wireOp",EDGE,"E660"),sQuery(id+"F0.wireOp",EDGE,"E661"),sQuery(id+"F0.wireOp",EDGE,"E662"),sQuery(id+"F0.wireOp",EDGE,"E663"),sQuery(id+"F0.wireOp",EDGE,"E664"),sQuery(id+"F0.wireOp",EDGE,"E665"),sQuery(id+"F0.wireOp",EDGE,"E666"),sQuery(id+"F0.wireOp",EDGE,"E667"),sQuery(id+"F0.wireOp",EDGE,"E668"),sQuery(id+"F0.wireOp",EDGE,"E669"),sQuery(id+"F0.wireOp",EDGE,"E670"),sQuery(id+"F0.wireOp",EDGE,"E671"),sQuery(id+"F0.wireOp",EDGE,"E672"),sQuery(id+"F0.wireOp",EDGE,"E673"),sQuery(id+"F0.wireOp",EDGE,"E674"),sQuery(id+"F0.wireOp",EDGE,"E675"),sQuery(id+"F0.wireOp",EDGE,"E676"),sQuery(id+"F0.wireOp",EDGE,"E677"),sQuery(id+"F0.wireOp",EDGE,"E678"),sQuery(id+"F0.wireOp",EDGE,"E679"),sQuery(id+"F0.wireOp",EDGE,"E680"),sQuery(id+"F0.wireOp",EDGE,"E681"),sQuery(id+"F0.wireOp",EDGE,"E682"),sQuery(id+"F0.wireOp",EDGE,"E683"),sQuery(id+"F0.wireOp",EDGE,"E684"),sQuery(id+"F0.wireOp",EDGE,"E685"),sQuery(id+"F0.wireOp",EDGE,"E686"),sQuery(id+"F0.wireOp",EDGE,"E687"),sQuery(id+"F0.wireOp",EDGE,"E688"),sQuery(id+"F0.wireOp",EDGE,"E689"),sQuery(id+"F0.wireOp",EDGE,"E690"),sQuery(id+"F0.wireOp",EDGE,"E691"),sQuery(id+"F0.wireOp",EDGE,"E692"),sQuery(id+"F0.wireOp",EDGE,"E693"),sQuery(id+"F0.wireOp",EDGE,"E694"),sQuery(id+"F0.wireOp",EDGE,"E695"),sQuery(id+"F0.wireOp",EDGE,"E696"),sQuery(id+"F0.wireOp",EDGE,"E697"),sQuery(id+"F0.wireOp",EDGE,"E698"),sQuery(id+"F0.wireOp",EDGE,"E699"),sQuery(id+"F0.wireOp",EDGE,"E700"),sQuery(id+"F0.wireOp",EDGE,"E701"),sQuery(id+"F0.wireOp",EDGE,"E702"),sQuery(id+"F0.wireOp",EDGE,"E703"),sQuery(id+"F0.wireOp",EDGE,"E704"),sQuery(id+"F0.wireOp",EDGE,"E705"),sQuery(id+"F0.wireOp",EDGE,"E706"),sQuery(id+"F0.wireOp",EDGE,"E707"),sQuery(id+"F0.wireOp",EDGE,"E708"),sQuery(id+"F0.wireOp",EDGE,"E709"),sQuery(id+"F0.wireOp",EDGE,"E710"),sQuery(id+"F0.wireOp",EDGE,"E711"),sQuery(id+"F0.wireOp",EDGE,"E712"),sQuery(id+"F0.wireOp",EDGE,"E713"),sQuery(id+"F0.wireOp",EDGE,"E714"),sQuery(id+"F0.wireOp",EDGE,"E715"),sQuery(id+"F0.wireOp",EDGE,"E716"),sQuery(id+"F0.wireOp",EDGE,"E717"),sQuery(id+"F0.wireOp",EDGE,"E718"),sQuery(id+"F0.wireOp",EDGE,"E719"),sQuery(id+"F0.wireOp",EDGE,"E720"),sQuery(id+"F0.wireOp",EDGE,"E721"),sQuery(id+"F0.wireOp",EDGE,"E722"),sQuery(id+"F0.wireOp",EDGE,"E723"),sQuery(id+"F0.wireOp",EDGE,"E724"),sQuery(id+"F0.wireOp",EDGE,"E725"),sQuery(id+"F0.wireOp",EDGE,"E726"),sQuery(id+"F0.wireOp",EDGE,"E727"),sQuery(id+"F0.wireOp",EDGE,"E728"),sQuery(id+"F0.wireOp",EDGE,"E729"),sQuery(id+"F0.wireOp",EDGE,"E730"),sQuery(id+"F0.wireOp",EDGE,"E731"),sQuery(id+"F0.wireOp",EDGE,"E732"),sQuery(id+"F0.wireOp",EDGE,"E733"),sQuery(id+"F0.wireOp",EDGE,"E734"),sQuery(id+"F0.wireOp",EDGE,"E735"),sQuery(id+"F0.wireOp",EDGE,"E736"),sQuery(id+"F0.wireOp",EDGE,"E737"),sQuery(id+"F0.wireOp",EDGE,"E738"),sQuery(id+"F0.wireOp",EDGE,"E739"),sQuery(id+"F0.wireOp",EDGE,"E740"),sQuery(id+"F0.wireOp",EDGE,"E741"),sQuery(id+"F0.wireOp",EDGE,"E742"),sQuery(id+"F0.wireOp",EDGE,"E743"),sQuery(id+"F0.wireOp",EDGE,"E744"),sQuery(id+"F0.wireOp",EDGE,"E745"),sQuery(id+"F0.wireOp",EDGE,"E746"),sQuery(id+"F0.wireOp",EDGE,"E747"),sQuery(id+"F0.wireOp",EDGE,"E748"),sQuery(id+"F0.wireOp",EDGE,"E749"),sQuery(id+"F0.wireOp",EDGE,"E750"),sQuery(id+"F0.wireOp",EDGE,"E751"),sQuery(id+"F0.wireOp",EDGE,"E752"),sQuery(id+"F0.wireOp",EDGE,"E753"),sQuery(id+"F0.wireOp",EDGE,"E754"),sQuery(id+"F0.wireOp",EDGE,"E755"),sQuery(id+"F0.wireOp",EDGE,"E756"),sQuery(id+"F0.wireOp",EDGE,"E757"),sQuery(id+"F0.wireOp",EDGE,"E758"),sQuery(id+"F0.wireOp",EDGE,"E759"),sQuery(id+"F0.wireOp",EDGE,"E760"),sQuery(id+"F0.wireOp",EDGE,"E761"),sQuery(id+"F0.wireOp",EDGE,"E762"),sQuery(id+"F0.wireOp",EDGE,"E763"),sQuery(id+"F0.wireOp",EDGE,"E764"),sQuery(id+"F0.wireOp",EDGE,"E765"),sQuery(id+"F0.wireOp",EDGE,"E766"),sQuery(id+"F0.wireOp",EDGE,"E767"),sQuery(id+"F0.wireOp",EDGE,"E768"),sQuery(id+"F0.wireOp",EDGE,"E769"),sQuery(id+"F0.wireOp",EDGE,"E770"),sQuery(id+"F0.wireOp",EDGE,"E771"),sQuery(id+"F0.wireOp",EDGE,"E772"),sQuery(id+"F0.wireOp",EDGE,"E773"),sQuery(id+"F0.wireOp",EDGE,"E774"),sQuery(id+"F0.wireOp",EDGE,"E775"),sQuery(id+"F0.wireOp",EDGE,"E776"),sQuery(id+"F0.wireOp",EDGE,"E777"),sQuery(id+"F0.wireOp",EDGE,"E778"),sQuery(id+"F0.wireOp",EDGE,"E779"),sQuery(id+"F0.wireOp",EDGE,"E780"),sQuery(id+"F0.wireOp",EDGE,"E781"),sQuery(id+"F0.wireOp",EDGE,"E782"),sQuery(id+"F0.wireOp",EDGE,"E783"),sQuery(id+"F0.wireOp",EDGE,"E784"),sQuery(id+"F0.wireOp",EDGE,"E785"),sQuery(id+"F0.wireOp",EDGE,"E786"),sQuery(id+"F0.wireOp",EDGE,"E787"),sQuery(id+"F0.wireOp",EDGE,"E788"),sQuery(id+"F0.wireOp",EDGE,"E789"),sQuery(id+"F0.wireOp",EDGE,"E790"),sQuery(id+"F0.wireOp",EDGE,"E791"),sQuery(id+"F0.wireOp",EDGE,"E792"),sQuery(id+"F0.wireOp",EDGE,"E793"),sQuery(id+"F0.wireOp",EDGE,"E794"),sQuery(id+"F0.wireOp",EDGE,"E795"),sQuery(id+"F0.wireOp",EDGE,"E796"),sQuery(id+"F0.wireOp",EDGE,"E797"),sQuery(id+"F0.wireOp",EDGE,"E798"),sQuery(id+"F0.wireOp",EDGE,"E799"),sQuery(id+"F0.wireOp",EDGE,"E800"),sQuery(id+"F0.wireOp",EDGE,"E801"),sQuery(id+"F0.wireOp",EDGE,"E802"),sQuery(id+"F0.wireOp",EDGE,"E803"),sQuery(id+"F0.wireOp",EDGE,"E804"),sQuery(id+"F0.wireOp",EDGE,"E805"),sQuery(id+"F0.wireOp",EDGE,"E806"),sQuery(id+"F0.wireOp",EDGE,"E807"),sQuery(id+"F0.wireOp",EDGE,"E808"),sQuery(id+"F0.wireOp",EDGE,"E809"),sQuery(id+"F0.wireOp",EDGE,"E810"),sQuery(id+"F0.wireOp",EDGE,"E811"),sQuery(id+"F0.wireOp",EDGE,"E812"),sQuery(id+"F0.wireOp",EDGE,"E813"),sQuery(id+"F0.wireOp",EDGE,"E814"),sQuery(id+"F0.wireOp",EDGE,"E815"),sQuery(id+"F0.wireOp",EDGE,"E816"),sQuery(id+"F0.wireOp",EDGE,"E817"),sQuery(id+"F0.wireOp",EDGE,"E818"),sQuery(id+"F0.wireOp",EDGE,"E819"),sQuery(id+"F0.wireOp",EDGE,"E820"),sQuery(id+"F0.wireOp",EDGE,"E821"),sQuery(id+"F0.wireOp",EDGE,"E822"),sQuery(id+"F0.wireOp",EDGE,"E823"),sQuery(id+"F0.wireOp",EDGE,"E824"),sQuery(id+"F0.wireOp",EDGE,"E825"),sQuery(id+"F0.wireOp",EDGE,"E826"),sQuery(id+"F0.wireOp",EDGE,"E827"),sQuery(id+"F0.wireOp",EDGE,"E828"),sQuery(id+"F0.wireOp",EDGE,"E829"),sQuery(id+"F0.wireOp",EDGE,"E830"),sQuery(id+"F0.wireOp",EDGE,"E831"),sQuery(id+"F0.wireOp",EDGE,"E832"),sQuery(id+"F0.wireOp",EDGE,"E833"),sQuery(id+"F0.wireOp",EDGE,"E834"),sQuery(id+"F0.wireOp",EDGE,"E835"),sQuery(id+"F0.wireOp",EDGE,"E836"),sQuery(id+"F0.wireOp",EDGE,"E837"),sQuery(id+"F0.wireOp",EDGE,"E838"),sQuery(id+"F0.wireOp",EDGE,"E839"),sQuery(id+"F0.wireOp",EDGE,"E840"),sQuery(id+"F0.wireOp",EDGE,"E841"),sQuery(id+"F0.wireOp",EDGE,"E842"),sQuery(id+"F0.wireOp",EDGE,"E843"),sQuery(id+"F0.wireOp",EDGE,"E844"),sQuery(id+"F0.wireOp",EDGE,"E845"),sQuery(id+"F0.wireOp",EDGE,"E846"),sQuery(id+"F0.wireOp",EDGE,"E847"),sQuery(id+"F0.wireOp",EDGE,"E848"),sQuery(id+"F0.wireOp",EDGE,"E849"),sQuery(id+"F0.wireOp",EDGE,"E850"),sQuery(id+"F0.wireOp",EDGE,"E851"),sQuery(id+"F0.wireOp",EDGE,"E852"),sQuery(id+"F0.wireOp",EDGE,"E853"),sQuery(id+"F0.wireOp",EDGE,"E854"),sQuery(id+"F0.wireOp",EDGE,"E855"),sQuery(id+"F0.wireOp",EDGE,"E856"),sQuery(id+"F0.wireOp",EDGE,"E857"),sQuery(id+"F0.wireOp",EDGE,"E858"),sQuery(id+"F0.wireOp",EDGE,"E859"),sQuery(id+"F0.wireOp",EDGE,"E860"),sQuery(id+"F0.wireOp",EDGE,"E861"),sQuery(id+"F0.wireOp",EDGE,"E862"),sQuery(id+"F0.wireOp",EDGE,"E863"),sQuery(id+"F0.wireOp",EDGE,"E864"),sQuery(id+"F0.wireOp",EDGE,"E865"),sQuery(id+"F0.wireOp",EDGE,"E866"),sQuery(id+"F0.wireOp",EDGE,"E867"),sQuery(id+"F0.wireOp",EDGE,"E868"),sQuery(id+"F0.wireOp",EDGE,"E869"),sQuery(id+"F0.wireOp",EDGE,"E870"),sQuery(id+"F0.wireOp",EDGE,"E871"),sQuery(id+"F0.wireOp",EDGE,"E872"),sQuery(id+"F0.wireOp",EDGE,"E873"),sQuery(id+"F0.wireOp",EDGE,"E874"),sQuery(id+"F0.wireOp",EDGE,"E875"),sQuery(id+"F0.wireOp",EDGE,"E876"),sQuery(id+"F0.wireOp",EDGE,"E877"),sQuery(id+"F0.wireOp",EDGE,"E878"),sQuery(id+"F0.wireOp",EDGE,"E879"),sQuery(id+"F0.wireOp",EDGE,"E880"),sQuery(id+"F0.wireOp",EDGE,"E881"),sQuery(id+"F0.wireOp",EDGE,"E882"),sQuery(id+"F0.wireOp",EDGE,"E883"),sQuery(id+"F0.wireOp",EDGE,"E884"),sQuery(id+"F0.wireOp",EDGE,"E885"),sQuery(id+"F0.wireOp",EDGE,"E886"),sQuery(id+"F0.wireOp",EDGE,"E887"),sQuery(id+"F0.wireOp",EDGE,"E888"),sQuery(id+"F0.wireOp",EDGE,"E889"),sQuery(id+"F0.wireOp",EDGE,"E890"),sQuery(id+"F0.wireOp",EDGE,"E891"),sQuery(id+"F0.wireOp",EDGE,"E892"),sQuery(id+"F0.wireOp",EDGE,"E893"),sQuery(id+"F0.wireOp",EDGE,"E894"),sQuery(id+"F0.wireOp",EDGE,"E895"),sQuery(id+"F0.wireOp",EDGE,"E896"),sQuery(id+"F0.wireOp",EDGE,"E897"),sQuery(id+"F0.wireOp",EDGE,"E898"),sQuery(id+"F0.wireOp",EDGE,"E899"),sQuery(id+"F0.wireOp",EDGE,"E900"),sQuery(id+"F0.wireOp",EDGE,"E901"),sQuery(id+"F0.wireOp",EDGE,"E902"),sQuery(id+"F0.wireOp",EDGE,"E903"),sQuery(id+"F0.wireOp",EDGE,"E904"),sQuery(id+"F0.wireOp",EDGE,"E905"),sQuery(id+"F0.wireOp",EDGE,"E906"),sQuery(id+"F0.wireOp",EDGE,"E907"),sQuery(id+"F0.wireOp",EDGE,"E908"),sQuery(id+"F0.wireOp",EDGE,"E909"),sQuery(id+"F0.wireOp",EDGE,"E910"),sQuery(id+"F0.wireOp",EDGE,"E911"),sQuery(id+"F0.wireOp",EDGE,"E912"),sQuery(id+"F0.wireOp",EDGE,"E913"),sQuery(id+"F0.wireOp",EDGE,"E914"),sQuery(id+"F0.wireOp",EDGE,"E915"),sQuery(id+"F0.wireOp",EDGE,"E916"),sQuery(id+"F0.wireOp",EDGE,"E917"),sQuery(id+"F0.wireOp",EDGE,"E918"),sQuery(id+"F0.wireOp",EDGE,"E919"),sQuery(id+"F0.wireOp",EDGE,"E920"),sQuery(id+"F0.wireOp",EDGE,"E921"),sQuery(id+"F0.wireOp",EDGE,"E922"),sQuery(id+"F0.wireOp",EDGE,"E923"),sQuery(id+"F0.wireOp",EDGE,"E924"),sQuery(id+"F0.wireOp",EDGE,"E925"),sQuery(id+"F0.wireOp",EDGE,"E926"),sQuery(id+"F0.wireOp",EDGE,"E927"),sQuery(id+"F0.wireOp",EDGE,"E928"),sQuery(id+"F0.wireOp",EDGE,"E929"),sQuery(id+"F0.wireOp",EDGE,"E930"),sQuery(id+"F0.wireOp",EDGE,"E931"),sQuery(id+"F0.wireOp",EDGE,"E932"),sQuery(id+"F0.wireOp",EDGE,"E933"),sQuery(id+"F0.wireOp",EDGE,"E934"),sQuery(id+"F0.wireOp",EDGE,"E935"),sQuery(id+"F0.wireOp",EDGE,"E936"),sQuery(id+"F0.wireOp",EDGE,"E937"),sQuery(id+"F0.wireOp",EDGE,"E938"),sQuery(id+"F0.wireOp",EDGE,"E939"),sQuery(id+"F0.wireOp",EDGE,"E940"),sQuery(id+"F0.wireOp",EDGE,"E941"),sQuery(id+"F0.wireOp",EDGE,"E942"),sQuery(id+"F0.wireOp",EDGE,"E943"),sQuery(id+"F0.wireOp",EDGE,"E944"),sQuery(id+"F0.wireOp",EDGE,"E945"),sQuery(id+"F0.wireOp",EDGE,"E946"),sQuery(id+"F0.wireOp",EDGE,"E947"),sQuery(id+"F0.wireOp",EDGE,"E948"),sQuery(id+"F0.wireOp",EDGE,"E949"),sQuery(id+"F0.wireOp",EDGE,"E950"),sQuery(id+"F0.wireOp",EDGE,"E951"),sQuery(id+"F0.wireOp",EDGE,"E952"),sQuery(id+"F0.wireOp",EDGE,"E953"),sQuery(id+"F0.wireOp",EDGE,"E954"),sQuery(id+"F0.wireOp",EDGE,"E955"),sQuery(id+"F0.wireOp",EDGE,"E956"),sQuery(id+"F0.wireOp",EDGE,"E957"),sQuery(id+"F0.wireOp",EDGE,"E958"),sQuery(id+"F0.wireOp",EDGE,"E959"),sQuery(id+"F0.wireOp",EDGE,"E960"),sQuery(id+"F0.wireOp",EDGE,"E961"),sQuery(id+"F0.wireOp",EDGE,"E962"),sQuery(id+"F0.wireOp",EDGE,"E963"),sQuery(id+"F0.wireOp",EDGE,"E964"),sQuery(id+"F0.wireOp",EDGE,"E965"),sQuery(id+"F0.wireOp",EDGE,"E966"),sQuery(id+"F0.wireOp",EDGE,"E967"),sQuery(id+"F0.wireOp",EDGE,"E968"),sQuery(id+"F0.wireOp",EDGE,"E969"),sQuery(id+"F0.wireOp",EDGE,"E970"),sQuery(id+"F0.wireOp",EDGE,"E971"),sQuery(id+"F0.wireOp",EDGE,"E972"),sQuery(id+"F0.wireOp",EDGE,"E973"),sQuery(id+"F0.wireOp",EDGE,"E974"),sQuery(id+"F0.wireOp",EDGE,"E975"),sQuery(id+"F0.wireOp",EDGE,"E976"),sQuery(id+"F0.wireOp",EDGE,"E977"),sQuery(id+"F0.wireOp",EDGE,"E978"),sQuery(id+"F0.wireOp",EDGE,"E979"),sQuery(id+"F0.wireOp",EDGE,"E980"),sQuery(id+"F0.wireOp",EDGE,"E981"),sQuery(id+"F0.wireOp",EDGE,"E982"),sQuery(id+"F0.wireOp",EDGE,"E983"),sQuery(id+"F0.wireOp",EDGE,"E984"),sQuery(id+"F0.wireOp",EDGE,"E985"),sQuery(id+"F0.wireOp",EDGE,"E986"),sQuery(id+"F0.wireOp",EDGE,"E987"),sQuery(id+"F0.wireOp",EDGE,"E988"),sQuery(id+"F0.wireOp",EDGE,"E989"),sQuery(id+"F0.wireOp",EDGE,"E990"),sQuery(id+"F0.wireOp",EDGE,"E991"),sQuery(id+"F0.wireOp",EDGE,"E992"),sQuery(id+"F0.wireOp",EDGE,"E993"),sQuery(id+"F0.wireOp",EDGE,"E994"),sQuery(id+"F0.wireOp",EDGE,"E995"),sQuery(id+"F0.wireOp",EDGE,"E996"),sQuery(id+"F0.wireOp",EDGE,"E997"),sQuery(id+"F0.wireOp",EDGE,"E998"),sQuery(id+"F0.wireOp",EDGE,"E999"),sQuery(id+"F0.wireOp",EDGE,"E1000"),sQuery(id+"F0.wireOp",EDGE,"E1001"),sQuery(id+"F0.wireOp",EDGE,"E1002"),sQuery(id+"F0.wireOp",EDGE,"E1003"),sQuery(id+"F0.wireOp",EDGE,"E1004"),sQuery(id+"F0.wireOp",EDGE,"E1005"),sQuery(id+"F0.wireOp",EDGE,"E1006"),sQuery(id+"F0.wireOp",EDGE,"E1007"),sQuery(id+"F0.wireOp",EDGE,"E1008"),sQuery(id+"F0.wireOp",EDGE,"E1009"),sQuery(id+"F0.wireOp",EDGE,"E1010"),sQuery(id+"F0.wireOp",EDGE,"E1011"),sQuery(id+"F0.wireOp",EDGE,"E1012"),sQuery(id+"F0.wireOp",EDGE,"E1013"),sQuery(id+"F0.wireOp",EDGE,"E1014"),sQuery(id+"F0.wireOp",EDGE,"E1015"),sQuery(id+"F0.wireOp",EDGE,"E1016"),sQuery(id+"F0.wireOp",EDGE,"E1017"),sQuery(id+"F0.wireOp",EDGE,"E1018"),sQuery(id+"F0.wireOp",EDGE,"E1019"),sQuery(id+"F0.wireOp",EDGE,"E1020"),sQuery(id+"F0.wireOp",EDGE,"E1021"),sQuery(id+"F0.wireOp",EDGE,"E1022"),sQuery(id+"F0.wireOp",EDGE,"E1023"),sQuery(id+"F0.wireOp",EDGE,"E1024"),sQuery(id+"F0.wireOp",EDGE,"E1025"),sQuery(id+"F0.wireOp",EDGE,"E1026"),sQuery(id+"F0.wireOp",EDGE,"E1027"),sQuery(id+"F0.wireOp",EDGE,"E1028"),sQuery(id+"F0.wireOp",EDGE,"E1029"),sQuery(id+"F0.wireOp",EDGE,"E1030"),sQuery(id+"F0.wireOp",EDGE,"E1031"),sQuery(id+"F0.wireOp",EDGE,"E1032"),sQuery(id+"F0.wireOp",EDGE,"E1033"),sQuery(id+"F0.wireOp",EDGE,"E1034"),sQuery(id+"F0.wireOp",EDGE,"E1035"),sQuery(id+"F0.wireOp",EDGE,"E1036"),sQuery(id+"F0.wireOp",EDGE,"E1037"),sQuery(id+"F0.wireOp",EDGE,"E1038"),sQuery(id+"F0.wireOp",EDGE,"E1039"),sQuery(id+"F0.wireOp",EDGE,"E1040"),sQuery(id+"F0.wireOp",EDGE,"E1041"),sQuery(id+"F0.wireOp",EDGE,"E1042"),sQuery(id+"F0.wireOp",EDGE,"E1043"),sQuery(id+"F0.wireOp",EDGE,"E1044"),sQuery(id+"F0.wireOp",EDGE,"E1045"),sQuery(id+"F0.wireOp",EDGE,"E1046"),sQuery(id+"F0.wireOp",EDGE,"E1047"),sQuery(id+"F0.wireOp",EDGE,"E1048"),sQuery(id+"F0.wireOp",EDGE,"E1049"),sQuery(id+"F0.wireOp",EDGE,"E1050"),sQuery(id+"F0.wireOp",EDGE,"E1051"),sQuery(id+"F0.wireOp",EDGE,"E1052"),sQuery(id+"F0.wireOp",EDGE,"E1053"),sQuery(id+"F0.wireOp",EDGE,"E1054"),sQuery(id+"F0.wireOp",EDGE,"E1055"),sQuery(id+"F0.wireOp",EDGE,"E1056"),sQuery(id+"F0.wireOp",EDGE,"E1057"),sQuery(id+"F0.wireOp",EDGE,"E1058"),sQuery(id+"F0.wireOp",EDGE,"E1059"),sQuery(id+"F0.wireOp",EDGE,"E1060"),sQuery(id+"F0.wireOp",EDGE,"E1061"),sQuery(id+"F0.wireOp",EDGE,"E1062"),sQuery(id+"F0.wireOp",EDGE,"E1063"),sQuery(id+"F0.wireOp",EDGE,"E1064"),sQuery(id+"F0.wireOp",EDGE,"E1065"),sQuery(id+"F0.wireOp",EDGE,"E1066"),sQuery(id+"F0.wireOp",EDGE,"E1067"),sQuery(id+"F0.wireOp",EDGE,"E1068"),sQuery(id+"F0.wireOp",EDGE,"E1069"),sQuery(id+"F0.wireOp",EDGE,"E1070"),sQuery(id+"F0.wireOp",EDGE,"E1071"),sQuery(id+"F0.wireOp",EDGE,"E1072"),sQuery(id+"F0.wireOp",EDGE,"E1073"),sQuery(id+"F0.wireOp",EDGE,"E1074"),sQuery(id+"F0.wireOp",EDGE,"E1075"),sQuery(id+"F0.wireOp",EDGE,"E1076"),sQuery(id+"F0.wireOp",EDGE,"E1077"),sQuery(id+"F0.wireOp",EDGE,"E1078"),sQuery(id+"F0.wireOp",EDGE,"E1079"),sQuery(id+"F0.wireOp",EDGE,"E1080"),sQuery(id+"F0.wireOp",EDGE,"E1081"),sQuery(id+"F0.wireOp",EDGE,"E1082"),sQuery(id+"F0.wireOp",EDGE,"E1083"),sQuery(id+"F0.wireOp",EDGE,"E1084"),sQuery(id+"F0.wireOp",EDGE,"E1085"),sQuery(id+"F0.wireOp",EDGE,"E1086"),sQuery(id+"F0.wireOp",EDGE,"E1087"),sQuery(id+"F0.wireOp",EDGE,"E1088"),sQuery(id+"F0.wireOp",EDGE,"E1089"),sQuery(id+"F0.wireOp",EDGE,"E1090"),sQuery(id+"F0.wireOp",EDGE,"E1091"),sQuery(id+"F0.wireOp",EDGE,"E1092"),sQuery(id+"F0.wireOp",EDGE,"E1093"),sQuery(id+"F0.wireOp",EDGE,"E1094"),sQuery(id+"F0.wireOp",EDGE,"E1095"),sQuery(id+"F0.wireOp",EDGE,"E1096"),sQuery(id+"F0.wireOp",EDGE,"E1097"),sQuery(id+"F0.wireOp",EDGE,"E1098"),sQuery(id+"F0.wireOp",EDGE,"E1099"),sQuery(id+"F0.wireOp",EDGE,"E1100"),sQuery(id+"F0.wireOp",EDGE,"E1101"),sQuery(id+"F0.wireOp",EDGE,"E1102"),sQuery(id+"F0.wireOp",EDGE,"E1103"),sQuery(id+"F0.wireOp",EDGE,"E1104"),sQuery(id+"F0.wireOp",EDGE,"E1105"),sQuery(id+"F0.wireOp",EDGE,"E1106"),sQuery(id+"F0.wireOp",EDGE,"E1107"),sQuery(id+"F0.wireOp",EDGE,"E1108"),sQuery(id+"F0.wireOp",EDGE,"E1109"),sQuery(id+"F0.wireOp",EDGE,"E1110"),sQuery(id+"F0.wireOp",EDGE,"E1111"),sQuery(id+"F0.wireOp",EDGE,"E1112"),sQuery(id+"F0.wireOp",EDGE,"E1113"),sQuery(id+"F0.wireOp",EDGE,"E1114"),sQuery(id+"F0.wireOp",EDGE,"E1115"),sQuery(id+"F0.wireOp",EDGE,"E1116"),sQuery(id+"F0.wireOp",EDGE,"E1117"),sQuery(id+"F0.wireOp",EDGE,"E1118"),sQuery(id+"F0.wireOp",EDGE,"E1119"),sQuery(id+"F0.wireOp",EDGE,"E1120"),sQuery(id+"F0.wireOp",EDGE,"E1121"),sQuery(id+"F0.wireOp",EDGE,"E1122"),sQuery(id+"F0.wireOp",EDGE,"E1123"),sQuery(id+"F0.wireOp",EDGE,"E1124"),sQuery(id+"F0.wireOp",EDGE,"E1125"),sQuery(id+"F0.wireOp",EDGE,"E1126"),sQuery(id+"F0.wireOp",EDGE,"E1127"),sQuery(id+"F0.wireOp",EDGE,"E1128"),sQuery(id+"F0.wireOp",EDGE,"E1129"),sQuery(id+"F0.wireOp",EDGE,"E1130"),sQuery(id+"F0.wireOp",EDGE,"E1131"),sQuery(id+"F0.wireOp",EDGE,"E1132"),sQuery(id+"F0.wireOp",EDGE,"E1133"),sQuery(id+"F0.wireOp",EDGE,"E1134"),sQuery(id+"F0.wireOp",EDGE,"E1135"),sQuery(id+"F0.wireOp",EDGE,"E1136"),sQuery(id+"F0.wireOp",EDGE,"E1137"),sQuery(id+"F0.wireOp",EDGE,"E1138"),sQuery(id+"F0.wireOp",EDGE,"E1139"),sQuery(id+"F0.wireOp",EDGE,"E1140"),sQuery(id+"F0.wireOp",EDGE,"E1141"),sQuery(id+"F0.wireOp",EDGE,"E1142"),sQuery(id+"F0.wireOp",EDGE,"E1143"),sQuery(id+"F0.wireOp",EDGE,"E1144"),sQuery(id+"F0.wireOp",EDGE,"E1145"),sQuery(id+"F0.wireOp",EDGE,"E1146"),sQuery(id+"F0.wireOp",EDGE,"E1147"),sQuery(id+"F0.wireOp",EDGE,"E1148"),sQuery(id+"F0.wireOp",EDGE,"E1149"),sQuery(id+"F0.wireOp",EDGE,"E1150"),sQuery(id+"F0.wireOp",EDGE,"E1151"),sQuery(id+"F0.wireOp",EDGE,"E1152"),sQuery(id+"F0.wireOp",EDGE,"E1153"),sQuery(id+"F0.wireOp",EDGE,"E1154"),sQuery(id+"F0.wireOp",EDGE,"E1155"),sQuery(id+"F0.wireOp",EDGE,"E1156"),sQuery(id+"F0.wireOp",EDGE,"E1157"),sQuery(id+"F0.wireOp",EDGE,"E1158"),sQuery(id+"F0.wireOp",EDGE,"E1159"),sQuery(id+"F0.wireOp",EDGE,"E1160"),sQuery(id+"F0.wireOp",EDGE,"E1161"),sQuery(id+"F0.wireOp",EDGE,"E1162"),sQuery(id+"F0.wireOp",EDGE,"E1163"),sQuery(id+"F0.wireOp",EDGE,"E1164"),sQuery(id+"F0.wireOp",EDGE,"E1165"),sQuery(id+"F0.wireOp",EDGE,"E1166"),sQuery(id+"F0.wireOp",EDGE,"E1167"),sQuery(id+"F0.wireOp",EDGE,"E1168"),sQuery(id+"F0.wireOp",EDGE,"E1169"),sQuery(id+"F0.wireOp",EDGE,"E1170"),sQuery(id+"F0.wireOp",EDGE,"E1171"),sQuery(id+"F0.wireOp",EDGE,"E1172"),sQuery(id+"F0.wireOp",EDGE,"E1173"),sQuery(id+"F0.wireOp",EDGE,"E1174"),sQuery(id+"F0.wireOp",EDGE,"E1175"),sQuery(id+"F0.wireOp",EDGE,"E1176"),sQuery(id+"F0.wireOp",EDGE,"E1177"),sQuery(id+"F0.wireOp",EDGE,"E1178"),sQuery(id+"F0.wireOp",EDGE,"E1179"),sQuery(id+"F0.wireOp",EDGE,"E1180"),sQuery(id+"F0.wireOp",EDGE,"E1181"),sQuery(id+"F0.wireOp",EDGE,"E1182"),sQuery(id+"F0.wireOp",EDGE,"E1183"),sQuery(id+"F0.wireOp",EDGE,"E1184"),sQuery(id+"F0.wireOp",EDGE,"E1185"),sQuery(id+"F0.wireOp",EDGE,"E1186"),sQuery(id+"F0.wireOp",EDGE,"E1187"),sQuery(id+"F0.wireOp",EDGE,"E1188"),sQuery(id+"F0.wireOp",EDGE,"E1189"),sQuery(id+"F0.wireOp",EDGE,"E1190"),sQuery(id+"F0.wireOp",EDGE,"E1191"),sQuery(id+"F0.wireOp",EDGE,"E1192"),sQuery(id+"F0.wireOp",EDGE,"E1193"),sQuery(id+"F0.wireOp",EDGE,"E1194"),sQuery(id+"F0.wireOp",EDGE,"E1195"),sQuery(id+"F0.wireOp",EDGE,"E1196"),sQuery(id+"F0.wireOp",EDGE,"E1197"),sQuery(id+"F0.wireOp",EDGE,"E1198"),sQuery(id+"F0.wireOp",EDGE,"E1199"),sQuery(id+"F0.wireOp",EDGE,"E1200"),sQuery(id+"F0.wireOp",EDGE,"E1201"),sQuery(id+"F0.wireOp",EDGE,"E1202"),sQuery(id+"F0.wireOp",EDGE,"E1203"),sQuery(id+"F0.wireOp",EDGE,"E1204"),sQuery(id+"F0.wireOp",EDGE,"E1205"),sQuery(id+"F0.wireOp",EDGE,"E1206"),sQuery(id+"F0.wireOp",EDGE,"E1207"),sQuery(id+"F0.wireOp",EDGE,"E1208"),sQuery(id+"F0.wireOp",EDGE,"E1209"),sQuery(id+"F0.wireOp",EDGE,"E1210"),sQuery(id+"F0.wireOp",EDGE,"E1211"),sQuery(id+"F0.wireOp",EDGE,"E1212"),sQuery(id+"F0.wireOp",EDGE,"E1213"),sQuery(id+"F0.wireOp",EDGE,"E1214"),sQuery(id+"F0.wireOp",EDGE,"E1215"),sQuery(id+"F0.wireOp",EDGE,"E1216"),sQuery(id+"F0.wireOp",EDGE,"E1217"),sQuery(id+"F0.wireOp",EDGE,"E1218"),sQuery(id+"F0.wireOp",EDGE,"E1219"),sQuery(id+"F0.wireOp",EDGE,"E1220"),sQuery(id+"F0.wireOp",EDGE,"E1221"),sQuery(id+"F0.wireOp",EDGE,"E1222"),sQuery(id+"F0.wireOp",EDGE,"E1223"),sQuery(id+"F0.wireOp",EDGE,"E1224"),sQuery(id+"F0.wireOp",EDGE,"E1225"),sQuery(id+"F0.wireOp",EDGE,"E1226"),sQuery(id+"F0.wireOp",EDGE,"E1227"),sQuery(id+"F0.wireOp",EDGE,"E1228"),sQuery(id+"F0.wireOp",EDGE,"E1229"),sQuery(id+"F0.wireOp",EDGE,"E1230"),sQuery(id+"F0.wireOp",EDGE,"E1231"),sQuery(id+"F0.wireOp",EDGE,"E1232"),sQuery(id+"F0.wireOp",EDGE,"E1233"),sQuery(id+"F0.wireOp",EDGE,"E1234"),sQuery(id+"F0.wireOp",EDGE,"E1235"),sQuery(id+"F0.wireOp",EDGE,"E1236"),sQuery(id+"F0.wireOp",EDGE,"E1237"),sQuery(id+"F0.wireOp",EDGE,"E1238"),sQuery(id+"F0.wireOp",EDGE,"E1239"),sQuery(id+"F0.wireOp",EDGE,"E1240"),sQuery(id+"F0.wireOp",EDGE,"E1241"),sQuery(id+"F0.wireOp",EDGE,"E1242"),sQuery(id+"F0.wireOp",EDGE,"E1243"),sQuery(id+"F0.wireOp",EDGE,"E1244"),sQuery(id+"F0.wireOp",EDGE,"E1245"),sQuery(id+"F0.wireOp",EDGE,"E1246"),sQuery(id+"F0.wireOp",EDGE,"E1247"),sQuery(id+"F0.wireOp",EDGE,"E1248"),sQuery(id+"F0.wireOp",EDGE,"E1249"),sQuery(id+"F0.wireOp",EDGE,"E1250"),sQuery(id+"F0.wireOp",EDGE,"E1251"),sQuery(id+"F0.wireOp",EDGE,"E1252"),sQuery(id+"F0.wireOp",EDGE,"E1253"),sQuery(id+"F0.wireOp",EDGE,"E1254"),sQuery(id+"F0.wireOp",EDGE,"E1255"),sQuery(id+"F0.wireOp",EDGE,"E1256"),sQuery(id+"F0.wireOp",EDGE,"E1257"),sQuery(id+"F0.wireOp",EDGE,"E1258"),sQuery(id+"F0.wireOp",EDGE,"E1259"),sQuery(id+"F0.wireOp",EDGE,"E1260"),sQuery(id+"F0.wireOp",EDGE,"E1261"),sQuery(id+"F0.wireOp",EDGE,"E1262"),sQuery(id+"F0.wireOp",EDGE,"E1263"),sQuery(id+"F0.wireOp",EDGE,"E1264"),sQuery(id+"F0.wireOp",EDGE,"E1265"),sQuery(id+"F0.wireOp",EDGE,"E1266"),sQuery(id+"F0.wireOp",EDGE,"E1267"),sQuery(id+"F0.wireOp",EDGE,"E1268"),sQuery(id+"F0.wireOp",EDGE,"E1269"),sQuery(id+"F0.wireOp",EDGE,"E1270"),sQuery(id+"F0.wireOp",EDGE,"E1271"),sQuery(id+"F0.wireOp",EDGE,"E1272"),sQuery(id+"F0.wireOp",EDGE,"E1273"),sQuery(id+"F0.wireOp",EDGE,"E1274"),sQuery(id+"F0.wireOp",EDGE,"E1275"),sQuery(id+"F0.wireOp",EDGE,"E1276"),sQuery(id+"F0.wireOp",EDGE,"E1277"),sQuery(id+"F0.wireOp",EDGE,"E1278"),sQuery(id+"F0.wireOp",EDGE,"E1279"),sQuery(id+"F0.wireOp",EDGE,"E1280"),sQuery(id+"F0.wireOp",EDGE,"E1281"),sQuery(id+"F0.wireOp",EDGE,"E1282"),sQuery(id+"F0.wireOp",EDGE,"E1283"),sQuery(id+"F0.wireOp",EDGE,"E1284"),sQuery(id+"F0.wireOp",EDGE,"E1285"),sQuery(id+"F0.wireOp",EDGE,"E1286"),sQuery(id+"F0.wireOp",EDGE,"E1287"),sQuery(id+"F0.wireOp",EDGE,"E1288"),sQuery(id+"F0.wireOp",EDGE,"E1289"),sQuery(id+"F0.wireOp",EDGE,"E1290"),sQuery(id+"F0.wireOp",EDGE,"E1291"),sQuery(id+"F0.wireOp",EDGE,"E1292"),sQuery(id+"F0.wireOp",EDGE,"E1293"),sQuery(id+"F0.wireOp",EDGE,"E1294"),sQuery(id+"F0.wireOp",EDGE,"E1295"),sQuery(id+"F0.wireOp",EDGE,"E1296"),sQuery(id+"F0.wireOp",EDGE,"E1297"),sQuery(id+"F0.wireOp",EDGE,"E1298"),sQuery(id+"F0.wireOp",EDGE,"E1299"),sQuery(id+"F0.wireOp",EDGE,"E1300"),sQuery(id+"F0.wireOp",EDGE,"E1301"),sQuery(id+"F0.wireOp",EDGE,"E1302"),sQuery(id+"F0.wireOp",EDGE,"E1303"),sQuery(id+"F0.wireOp",EDGE,"E1304"),sQuery(id+"F0.wireOp",EDGE,"E1305"),sQuery(id+"F0.wireOp",EDGE,"E1306"),sQuery(id+"F0.wireOp",EDGE,"E1307"),sQuery(id+"F0.wireOp",EDGE,"E1308"),sQuery(id+"F0.wireOp",EDGE,"E1309"),sQuery(id+"F0.wireOp",EDGE,"E1310"),sQuery(id+"F0.wireOp",EDGE,"E1311"),sQuery(id+"F0.wireOp",EDGE,"E1312"),sQuery(id+"F0.wireOp",EDGE,"E1313"),sQuery(id+"F0.wireOp",EDGE,"E1314"),sQuery(id+"F0.wireOp",EDGE,"E1315"),sQuery(id+"F0.wireOp",EDGE,"E1316"),sQuery(id+"F0.wireOp",EDGE,"E1317"),sQuery(id+"F0.wireOp",EDGE,"E1318"),sQuery(id+"F0.wireOp",EDGE,"E1319"),sQuery(id+"F0.wireOp",EDGE,"E1320"),sQuery(id+"F0.wireOp",EDGE,"E1321"),sQuery(id+"F0.wireOp",EDGE,"E1322"),sQuery(id+"F0.wireOp",EDGE,"E1323"),sQuery(id+"F0.wireOp",EDGE,"E1324"),sQuery(id+"F0.wireOp",EDGE,"E1325"),sQuery(id+"F0.wireOp",EDGE,"E1326"),sQuery(id+"F0.wireOp",EDGE,"E1327"),sQuery(id+"F0.wireOp",EDGE,"E1328"),sQuery(id+"F0.wireOp",EDGE,"E1329"),sQuery(id+"F0.wireOp",EDGE,"E1330"),sQuery(id+"F0.wireOp",EDGE,"E1331"),sQuery(id+"F0.wireOp",EDGE,"E1332"),sQuery(id+"F0.wireOp",EDGE,"E1333"),sQuery(id+"F0.wireOp",EDGE,"E1334"),sQuery(id+"F0.wireOp",EDGE,"E1335"),sQuery(id+"F0.wireOp",EDGE,"E1336"),sQuery(id+"F0.wireOp",EDGE,"E1337"),sQuery(id+"F0.wireOp",EDGE,"E1338"),sQuery(id+"F0.wireOp",EDGE,"E1339"),sQuery(id+"F0.wireOp",EDGE,"E1340"),sQuery(id+"F0.wireOp",EDGE,"E1341"),sQuery(id+"F0.wireOp",EDGE,"E1342"),sQuery(id+"F0.wireOp",EDGE,"E1343"),sQuery(id+"F0.wireOp",EDGE,"E1344"),sQuery(id+"F0.wireOp",EDGE,"E1345"),sQuery(id+"F0.wireOp",EDGE,"E1346"),sQuery(id+"F0.wireOp",EDGE,"E1347"),sQuery(id+"F0.wireOp",EDGE,"E1348"),sQuery(id+"F0.wireOp",EDGE,"E1349"),sQuery(id+"F0.wireOp",EDGE,"E1350"),sQuery(id+"F0.wireOp",EDGE,"E1351"),sQuery(id+"F0.wireOp",EDGE,"E1352"),sQuery(id+"F0.wireOp",EDGE,"E1353"),sQuery(id+"F0.wireOp",EDGE,"E1354"),sQuery(id+"F0.wireOp",EDGE,"E1355"),sQuery(id+"F0.wireOp",EDGE,"E1356"),sQuery(id+"F0.wireOp",EDGE,"E1357"),sQuery(id+"F0.wireOp",EDGE,"E1358"),sQuery(id+"F0.wireOp",EDGE,"E1359"),sQuery(id+"F0.wireOp",EDGE,"E1360"),sQuery(id+"F0.wireOp",EDGE,"E1361"),sQuery(id+"F0.wireOp",EDGE,"E1362"),sQuery(id+"F0.wireOp",EDGE,"E1363"),sQuery(id+"F0.wireOp",EDGE,"E1364"),sQuery(id+"F0.wireOp",EDGE,"E1365"),sQuery(id+"F0.wireOp",EDGE,"E1366"),sQuery(id+"F0.wireOp",EDGE,"E1367"),sQuery(id+"F0.wireOp",EDGE,"E1368"),sQuery(id+"F0.wireOp",EDGE,"E1369"),sQuery(id+"F0.wireOp",EDGE,"E1370"),sQuery(id+"F0.wireOp",EDGE,"E1371"),sQuery(id+"F0.wireOp",EDGE,"E1372"),sQuery(id+"F0.wireOp",EDGE,"E1373"),sQuery(id+"F0.wireOp",EDGE,"E1374"),sQuery(id+"F0.wireOp",EDGE,"E1375"),sQuery(id+"F0.wireOp",EDGE,"E1376"),sQuery(id+"F0.wireOp",EDGE,"E1377"),sQuery(id+"F0.wireOp",EDGE,"E1378"),sQuery(id+"F0.wireOp",EDGE,"E1379"),sQuery(id+"F0.wireOp",EDGE,"E1380"),sQuery(id+"F0.wireOp",EDGE,"E1381"),sQuery(id+"F0.wireOp",EDGE,"E1382"),sQuery(id+"F0.wireOp",EDGE,"E1383"),sQuery(id+"F0.wireOp",EDGE,"E1384"),sQuery(id+"F0.wireOp",EDGE,"E1385"),sQuery(id+"F0.wireOp",EDGE,"E1386"),sQuery(id+"F0.wireOp",EDGE,"E1387"),sQuery(id+"F0.wireOp",EDGE,"E1388"),sQuery(id+"F0.wireOp",EDGE,"E1389"),sQuery(id+"F0.wireOp",EDGE,"E1390"),sQuery(id+"F0.wireOp",EDGE,"E1391"),sQuery(id+"F0.wireOp",EDGE,"E1392"),sQuery(id+"F0.wireOp",EDGE,"E1393"),sQuery(id+"F0.wireOp",EDGE,"E1394"),sQuery(id+"F0.wireOp",EDGE,"E1395"),sQuery(id+"F0.wireOp",EDGE,"E1396"),sQuery(id+"F0.wireOp",EDGE,"E1397"),sQuery(id+"F0.wireOp",EDGE,"E1398"),sQuery(id+"F0.wireOp",EDGE,"E1399"),sQuery(id+"F0.wireOp",EDGE,"E1400"),sQuery(id+"F0.wireOp",EDGE,"E1401"),sQuery(id+"F0.wireOp",EDGE,"E1402"),sQuery(id+"F0.wireOp",EDGE,"E1403"),sQuery(id+"F0.wireOp",EDGE,"E1404"),sQuery(id+"F0.wireOp",EDGE,"E1405"),sQuery(id+"F0.wireOp",EDGE,"E1406"),sQuery(id+"F0.wireOp",EDGE,"E1407"),sQuery(id+"F0.wireOp",EDGE,"E1408"),sQuery(id+"F0.wireOp",EDGE,"E1409"),sQuery(id+"F0.wireOp",EDGE,"E1410"),sQuery(id+"F0.wireOp",EDGE,"E1411"),sQuery(id+"F0.wireOp",EDGE,"E1412"),sQuery(id+"F0.wireOp",EDGE,"E1413"),sQuery(id+"F0.wireOp",EDGE,"E1414"),sQuery(id+"F0.wireOp",EDGE,"E1415"),sQuery(id+"F0.wireOp",EDGE,"E1416"),sQuery(id+"F0.wireOp",EDGE,"E1417"),sQuery(id+"F0.wireOp",EDGE,"E1418"),sQuery(id+"F0.wireOp",EDGE,"E1419"),sQuery(id+"F0.wireOp",EDGE,"E1420"),sQuery(id+"F0.wireOp",EDGE,"E1421"),sQuery(id+"F0.wireOp",EDGE,"E1422"),sQuery(id+"F0.wireOp",EDGE,"E1423"),sQuery(id+"F0.wireOp",EDGE,"E1424"),sQuery(id+"F0.wireOp",EDGE,"E1425"),sQuery(id+"F0.wireOp",EDGE,"E1426"),sQuery(id+"F0.wireOp",EDGE,"E1427"),sQuery(id+"F0.wireOp",EDGE,"E1428"),sQuery(id+"F0.wireOp",EDGE,"E1429"),sQuery(id+"F0.wireOp",EDGE,"E1430"),sQuery(id+"F0.wireOp",EDGE,"E1431"),sQuery(id+"F0.wireOp",EDGE,"E1432"),sQuery(id+"F0.wireOp",EDGE,"E1433"),sQuery(id+"F0.wireOp",EDGE,"E1434"),sQuery(id+"F0.wireOp",EDGE,"E1435"),sQuery(id+"F0.wireOp",EDGE,"E1436"),sQuery(id+"F0.wireOp",EDGE,"E1437"),sQuery(id+"F0.wireOp",EDGE,"E1438"),sQuery(id+"F0.wireOp",EDGE,"E1439"),sQuery(id+"F0.wireOp",EDGE,"E1440"),sQuery(id+"F0.wireOp",EDGE,"E1441"),sQuery(id+"F0.wireOp",EDGE,"E1442"),sQuery(id+"F0.wireOp",EDGE,"E1443"),sQuery(id+"F0.wireOp",EDGE,"E1444"),sQuery(id+"F0.wireOp",EDGE,"E1445"),sQuery(id+"F0.wireOp",EDGE,"E1446"),sQuery(id+"F0.wireOp",EDGE,"E1447"),sQuery(id+"F0.wireOp",EDGE,"E1448"),sQuery(id+"F0.wireOp",EDGE,"E1449"),sQuery(id+"F0.wireOp",EDGE,"E1450"),sQuery(id+"F0.wireOp",EDGE,"E1451"),sQuery(id+"F0.wireOp",EDGE,"E1452"),sQuery(id+"F0.wireOp",EDGE,"E1453"),sQuery(id+"F0.wireOp",EDGE,"E1454"),sQuery(id+"F0.wireOp",EDGE,"E1455"),sQuery(id+"F0.wireOp",EDGE,"E1456"),sQuery(id+"F0.wireOp",EDGE,"E1457"),sQuery(id+"F0.wireOp",EDGE,"E1458"),sQuery(id+"F0.wireOp",EDGE,"E1459"),sQuery(id+"F0.wireOp",EDGE,"E1460"),sQuery(id+"F0.wireOp",EDGE,"E1461"),sQuery(id+"F0.wireOp",EDGE,"E1462"),sQuery(id+"F0.wireOp",EDGE,"E1463")])]});
            var Q1;
            Q1=qCreatedBy(makeId("Origin.pointOp"),VERTEX);
            transform(context, id + "F2", {"entities" : qUnion([Q0]), "transformType" : TransformType.SCALE_UNIFORMLY, "scale" : 0.12, "scalePoint" : qUnion([Q1]), "makeCopy" : false});
        }
    });
